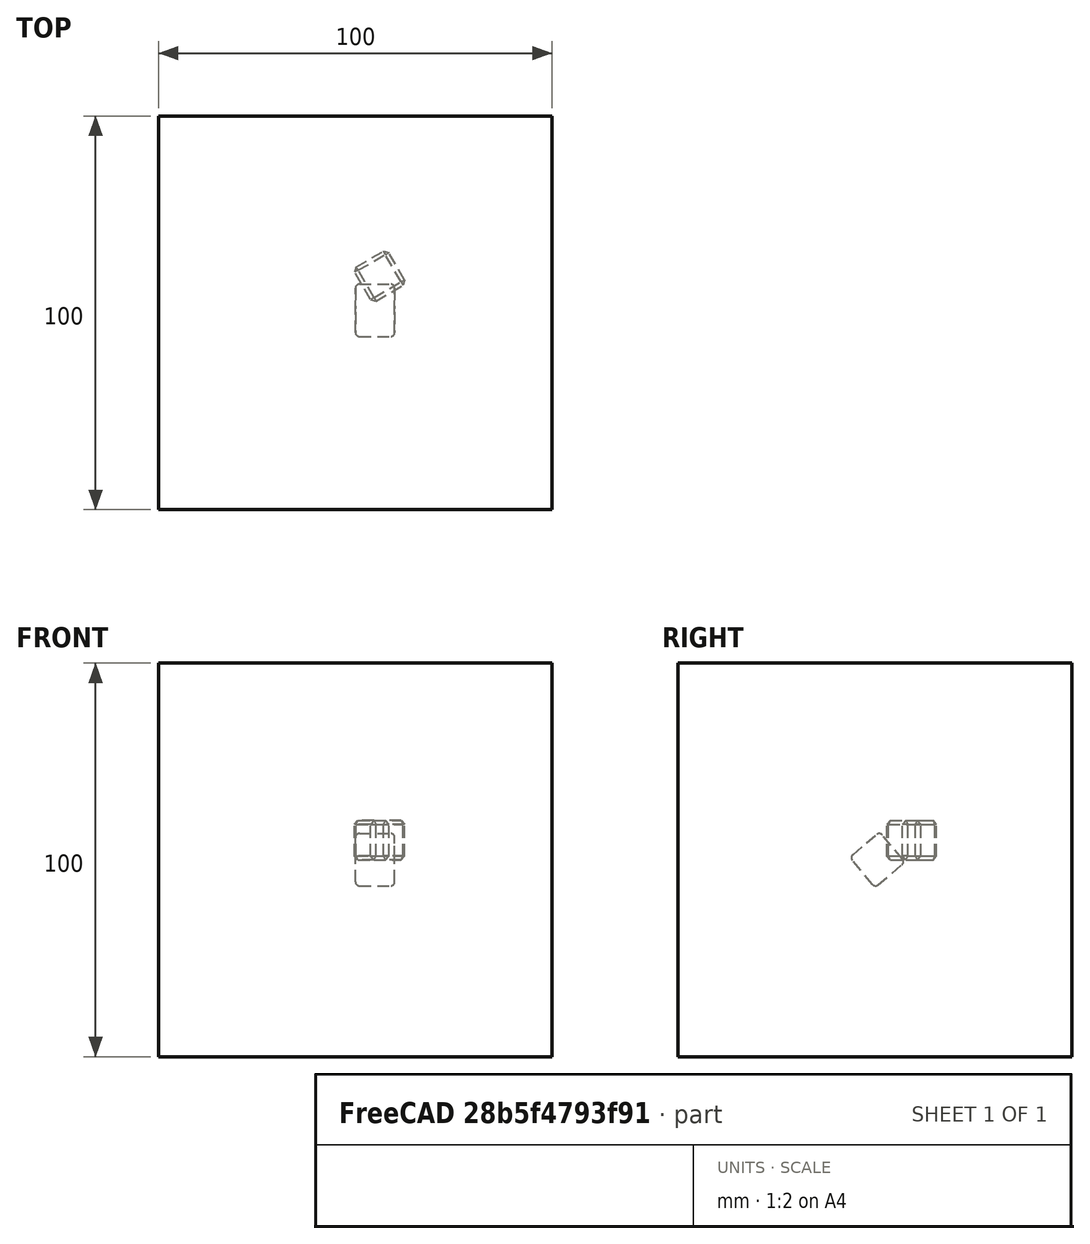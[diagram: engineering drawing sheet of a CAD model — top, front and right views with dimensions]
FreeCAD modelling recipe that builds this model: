
FCSTD DOCUMENT  (FreeCAD 1.0R39109 (Git))
Label: Chamfer_and_fillet
License: All rights reserved
objects: App::DocumentObjectGroupPython×1251, App::Part×3, Part::Box×2, Part::FeaturePython×1, Part::Chamfer×1, Part::Fillet×1
note: 5 computed .brp shape members not serialized (recipe doc carries the construction recipe); baked Part::Feature solids carry a one-line shape summary decoded from their .brp

FEATURE [App::DocumentObjectGroupPython] HALFPI  # scripted group (container) (typed FeaturePython)
  name = HALFPI
  value = pi/2.
FEATURE [App::DocumentObjectGroupPython] PI  # scripted group (container) (typed FeaturePython)
  name = PI
  value = 1.*pi
FEATURE [App::DocumentObjectGroupPython] TWOPI  # scripted group (container) (typed FeaturePython)
  name = TWOPI
  value = 2.*pi
FEATURE [App::DocumentObjectGroupPython] Constants  # scripted group (container) (typed FeaturePython)
  Group = -> [HALFPI,PI,TWOPI]
FEATURE [App::DocumentObjectGroupPython] Variables  # scripted group (container) (typed FeaturePython)
FEATURE [App::DocumentObjectGroupPython] Quantities  # scripted group (container) (typed FeaturePython)
FEATURE [App::DocumentObjectGroupPython] Isotopes  # scripted group (container) (typed FeaturePython)
FEATURE [App::DocumentObjectGroupPython] Elements  # scripted group (container) (typed FeaturePython)
FEATURE [App::DocumentObjectGroupPython] Matrix  # scripted group (container) (typed FeaturePython)
FEATURE [App::DocumentObjectGroupPython] Surfaces  # scripted group (container) (typed FeaturePython)
FEATURE [App::DocumentObjectGroupPython] Opticals  # scripted group (container) (typed FeaturePython)
  Group = -> [Matrix,Surfaces]
FEATURE [App::DocumentObjectGroupPython] G4Isotopes  # scripted group (container) (typed FeaturePython)
FEATURE [App::DocumentObjectGroupPython] H_element  # scripted group (container) (typed FeaturePython)
  Z = 1
  atom_value = 1.008
  formula = H
  name = H_element
FEATURE [App::DocumentObjectGroupPython] He_element  # scripted group (container) (typed FeaturePython)
  Z = 2
  atom_value = 4.0026
  formula = He
  name = He_element
FEATURE [App::DocumentObjectGroupPython] Li_element  # scripted group (container) (typed FeaturePython)
  Z = 3
  atom_value = 6.94
  formula = Li
  name = Li_element
FEATURE [App::DocumentObjectGroupPython] Be_element  # scripted group (container) (typed FeaturePython)
  Z = 4
  atom_value = 9.01218
  formula = Be
  name = Be_element
FEATURE [App::DocumentObjectGroupPython] B_element  # scripted group (container) (typed FeaturePython)
  Z = 5
  atom_value = 10.81
  formula = B
  name = B_element
FEATURE [App::DocumentObjectGroupPython] C_element  # scripted group (container) (typed FeaturePython)
  Z = 6
  atom_value = 12.011
  formula = C
  name = C_element
FEATURE [App::DocumentObjectGroupPython] N_element  # scripted group (container) (typed FeaturePython)
  Z = 7
  atom_value = 14.007
  formula = N
  name = N_element
FEATURE [App::DocumentObjectGroupPython] O_element  # scripted group (container) (typed FeaturePython)
  Z = 8
  atom_value = 15.999
  formula = O
  name = O_element
FEATURE [App::DocumentObjectGroupPython] F_element  # scripted group (container) (typed FeaturePython)
  Z = 9
  atom_value = 18.9984
  formula = F
  name = F_element
FEATURE [App::DocumentObjectGroupPython] Ne_element  # scripted group (container) (typed FeaturePython)
  Z = 10
  atom_value = 20.1797
  formula = Ne
  name = Ne_element
FEATURE [App::DocumentObjectGroupPython] Na_element  # scripted group (container) (typed FeaturePython)
  Z = 11
  atom_value = 22.9898
  formula = Na
  name = Na_element
FEATURE [App::DocumentObjectGroupPython] Mg_element  # scripted group (container) (typed FeaturePython)
  Z = 12
  atom_value = 24.305
  formula = Mg
  name = Mg_element
FEATURE [App::DocumentObjectGroupPython] Al_element  # scripted group (container) (typed FeaturePython)
  Z = 13
  atom_value = 26.9815
  formula = Al
  name = Al_element
FEATURE [App::DocumentObjectGroupPython] Si_element  # scripted group (container) (typed FeaturePython)
  Z = 14
  atom_value = 28.085
  formula = Si
  name = Si_element
FEATURE [App::DocumentObjectGroupPython] P_element  # scripted group (container) (typed FeaturePython)
  Z = 15
  atom_value = 30.9738
  formula = P
  name = P_element
FEATURE [App::DocumentObjectGroupPython] S_element  # scripted group (container) (typed FeaturePython)
  Z = 16
  atom_value = 32.06
  formula = S
  name = S_element
FEATURE [App::DocumentObjectGroupPython] Cl_element  # scripted group (container) (typed FeaturePython)
  Z = 17
  atom_value = 35.45
  formula = Cl
  name = Cl_element
FEATURE [App::DocumentObjectGroupPython] Ar_element  # scripted group (container) (typed FeaturePython)
  Z = 18
  atom_value = 39.95
  formula = Ar
  name = Ar_element
FEATURE [App::DocumentObjectGroupPython] K_element  # scripted group (container) (typed FeaturePython)
  Z = 19
  atom_value = 39.0983
  formula = K
  name = K_element
FEATURE [App::DocumentObjectGroupPython] Ca_element  # scripted group (container) (typed FeaturePython)
  Z = 20
  atom_value = 40.078
  formula = Ca
  name = Ca_element
FEATURE [App::DocumentObjectGroupPython] Sc_element  # scripted group (container) (typed FeaturePython)
  Z = 21
  atom_value = 44.9559
  formula = Sc
  name = Sc_element
FEATURE [App::DocumentObjectGroupPython] Ti_element  # scripted group (container) (typed FeaturePython)
  Z = 22
  atom_value = 47.867
  formula = Ti
  name = Ti_element
FEATURE [App::DocumentObjectGroupPython] V_element  # scripted group (container) (typed FeaturePython)
  Z = 23
  atom_value = 50.9415
  formula = V
  name = V_element
FEATURE [App::DocumentObjectGroupPython] Cr_element  # scripted group (container) (typed FeaturePython)
  Z = 24
  atom_value = 51.9961
  formula = Cr
  name = Cr_element
FEATURE [App::DocumentObjectGroupPython] Mn_element  # scripted group (container) (typed FeaturePython)
  Z = 25
  atom_value = 54.938
  formula = Mn
  name = Mn_element
FEATURE [App::DocumentObjectGroupPython] Fe_element  # scripted group (container) (typed FeaturePython)
  Z = 26
  atom_value = 55.845
  formula = Fe
  name = Fe_element
FEATURE [App::DocumentObjectGroupPython] Co_element  # scripted group (container) (typed FeaturePython)
  Z = 27
  atom_value = 58.9332
  formula = Co
  name = Co_element
FEATURE [App::DocumentObjectGroupPython] Ni_element  # scripted group (container) (typed FeaturePython)
  Z = 28
  atom_value = 58.6934
  formula = Ni
  name = Ni_element
FEATURE [App::DocumentObjectGroupPython] Cu_element  # scripted group (container) (typed FeaturePython)
  Z = 29
  atom_value = 63.546
  formula = Cu
  name = Cu_element
FEATURE [App::DocumentObjectGroupPython] Zn_element  # scripted group (container) (typed FeaturePython)
  Z = 30
  atom_value = 65.38
  formula = Zn
  name = Zn_element
FEATURE [App::DocumentObjectGroupPython] Ga_element  # scripted group (container) (typed FeaturePython)
  Z = 31
  atom_value = 69.723
  formula = Ga
  name = Ga_element
FEATURE [App::DocumentObjectGroupPython] Ge_element  # scripted group (container) (typed FeaturePython)
  Z = 32
  atom_value = 72.63
  formula = Ge
  name = Ge_element
FEATURE [App::DocumentObjectGroupPython] As_element  # scripted group (container) (typed FeaturePython)
  Z = 33
  atom_value = 74.9216
  formula = As
  name = As_element
FEATURE [App::DocumentObjectGroupPython] Se_element  # scripted group (container) (typed FeaturePython)
  Z = 34
  atom_value = 78.971
  formula = Se
  name = Se_element
FEATURE [App::DocumentObjectGroupPython] Br_element  # scripted group (container) (typed FeaturePython)
  Z = 35
  atom_value = 79.904
  formula = Br
  name = Br_element
FEATURE [App::DocumentObjectGroupPython] Kr_element  # scripted group (container) (typed FeaturePython)
  Z = 36
  atom_value = 83.798
  formula = Kr
  name = Kr_element
FEATURE [App::DocumentObjectGroupPython] Rb_element  # scripted group (container) (typed FeaturePython)
  Z = 37
  atom_value = 85.4678
  formula = Rb
  name = Rb_element
FEATURE [App::DocumentObjectGroupPython] Sr_element  # scripted group (container) (typed FeaturePython)
  Z = 38
  atom_value = 87.62
  formula = Sr
  name = Sr_element
FEATURE [App::DocumentObjectGroupPython] Y_element  # scripted group (container) (typed FeaturePython)
  Z = 39
  atom_value = 88.9058
  formula = Y
  name = Y_element
FEATURE [App::DocumentObjectGroupPython] Zr_element  # scripted group (container) (typed FeaturePython)
  Z = 40
  atom_value = 91.224
  formula = Zr
  name = Zr_element
FEATURE [App::DocumentObjectGroupPython] Nb_element  # scripted group (container) (typed FeaturePython)
  Z = 41
  atom_value = 92.9064
  formula = Nb
  name = Nb_element
FEATURE [App::DocumentObjectGroupPython] Mo_element  # scripted group (container) (typed FeaturePython)
  Z = 42
  atom_value = 95.95
  formula = Mo
  name = Mo_element
FEATURE [App::DocumentObjectGroupPython] Tc_element  # scripted group (container) (typed FeaturePython)
  Z = 43
  atom_value = 97
  formula = Tc
  name = Tc_element
FEATURE [App::DocumentObjectGroupPython] Ru_element  # scripted group (container) (typed FeaturePython)
  Z = 44
  atom_value = 101.07
  formula = Ru
  name = Ru_element
FEATURE [App::DocumentObjectGroupPython] Rh_element  # scripted group (container) (typed FeaturePython)
  Z = 45
  atom_value = 102.905
  formula = Rh
  name = Rh_element
FEATURE [App::DocumentObjectGroupPython] Pd_element  # scripted group (container) (typed FeaturePython)
  Z = 46
  atom_value = 106.42
  formula = Pd
  name = Pd_element
FEATURE [App::DocumentObjectGroupPython] Ag_element  # scripted group (container) (typed FeaturePython)
  Z = 47
  atom_value = 107.868
  formula = Ag
  name = Ag_element
FEATURE [App::DocumentObjectGroupPython] Cd_element  # scripted group (container) (typed FeaturePython)
  Z = 48
  atom_value = 112.414
  formula = Cd
  name = Cd_element
FEATURE [App::DocumentObjectGroupPython] In_element  # scripted group (container) (typed FeaturePython)
  Z = 49
  atom_value = 114.818
  formula = In
  name = In_element
FEATURE [App::DocumentObjectGroupPython] Sn_element  # scripted group (container) (typed FeaturePython)
  Z = 50
  atom_value = 118.71
  formula = Sn
  name = Sn_element
FEATURE [App::DocumentObjectGroupPython] Sb_element  # scripted group (container) (typed FeaturePython)
  Z = 51
  atom_value = 121.76
  formula = Sb
  name = Sb_element
FEATURE [App::DocumentObjectGroupPython] Te_element  # scripted group (container) (typed FeaturePython)
  Z = 52
  atom_value = 127.6
  formula = Te
  name = Te_element
FEATURE [App::DocumentObjectGroupPython] I_element  # scripted group (container) (typed FeaturePython)
  Z = 53
  atom_value = 126.904
  formula = I
  name = I_element
FEATURE [App::DocumentObjectGroupPython] Xe_element  # scripted group (container) (typed FeaturePython)
  Z = 54
  atom_value = 131.293
  formula = Xe
  name = Xe_element
FEATURE [App::DocumentObjectGroupPython] Cs_element  # scripted group (container) (typed FeaturePython)
  Z = 55
  atom_value = 132.905
  formula = Cs
  name = Cs_element
FEATURE [App::DocumentObjectGroupPython] Ba_element  # scripted group (container) (typed FeaturePython)
  Z = 56
  atom_value = 137.327
  formula = Ba
  name = Ba_element
FEATURE [App::DocumentObjectGroupPython] La_element  # scripted group (container) (typed FeaturePython)
  Z = 57
  atom_value = 138.905
  formula = La
  name = La_element
FEATURE [App::DocumentObjectGroupPython] Ce_element  # scripted group (container) (typed FeaturePython)
  Z = 58
  atom_value = 140.116
  formula = Ce
  name = Ce_element
FEATURE [App::DocumentObjectGroupPython] Pr_element  # scripted group (container) (typed FeaturePython)
  Z = 59
  atom_value = 140.908
  formula = Pr
  name = Pr_element
FEATURE [App::DocumentObjectGroupPython] Nd_element  # scripted group (container) (typed FeaturePython)
  Z = 60
  atom_value = 144.242
  formula = Nd
  name = Nd_element
FEATURE [App::DocumentObjectGroupPython] Pm_element  # scripted group (container) (typed FeaturePython)
  Z = 61
  atom_value = 145
  formula = Pm
  name = Pm_element
FEATURE [App::DocumentObjectGroupPython] Sm_element  # scripted group (container) (typed FeaturePython)
  Z = 62
  atom_value = 150.36
  formula = Sm
  name = Sm_element
FEATURE [App::DocumentObjectGroupPython] Eu_element  # scripted group (container) (typed FeaturePython)
  Z = 63
  atom_value = 151.964
  formula = Eu
  name = Eu_element
FEATURE [App::DocumentObjectGroupPython] Gd_element  # scripted group (container) (typed FeaturePython)
  Z = 64
  atom_value = 157.25
  formula = Gd
  name = Gd_element
FEATURE [App::DocumentObjectGroupPython] Tb_element  # scripted group (container) (typed FeaturePython)
  Z = 65
  atom_value = 158.925
  formula = Tb
  name = Tb_element
FEATURE [App::DocumentObjectGroupPython] Dy_element  # scripted group (container) (typed FeaturePython)
  Z = 66
  atom_value = 162.5
  formula = Dy
  name = Dy_element
FEATURE [App::DocumentObjectGroupPython] Ho_element  # scripted group (container) (typed FeaturePython)
  Z = 67
  atom_value = 164.93
  formula = Ho
  name = Ho_element
FEATURE [App::DocumentObjectGroupPython] Er_element  # scripted group (container) (typed FeaturePython)
  Z = 68
  atom_value = 167.259
  formula = Er
  name = Er_element
FEATURE [App::DocumentObjectGroupPython] Tm_element  # scripted group (container) (typed FeaturePython)
  Z = 69
  atom_value = 168.934
  formula = Tm
  name = Tm_element
FEATURE [App::DocumentObjectGroupPython] Yb_element  # scripted group (container) (typed FeaturePython)
  Z = 70
  atom_value = 173.045
  formula = Yb
  name = Yb_element
FEATURE [App::DocumentObjectGroupPython] Lu_element  # scripted group (container) (typed FeaturePython)
  Z = 71
  atom_value = 174.967
  formula = Lu
  name = Lu_element
FEATURE [App::DocumentObjectGroupPython] Hf_element  # scripted group (container) (typed FeaturePython)
  Z = 72
  atom_value = 178.49
  formula = Hf
  name = Hf_element
FEATURE [App::DocumentObjectGroupPython] Ta_element  # scripted group (container) (typed FeaturePython)
  Z = 73
  atom_value = 180.948
  formula = Ta
  name = Ta_element
FEATURE [App::DocumentObjectGroupPython] W_element  # scripted group (container) (typed FeaturePython)
  Z = 74
  atom_value = 183.84
  formula = W
  name = W_element
FEATURE [App::DocumentObjectGroupPython] Re_element  # scripted group (container) (typed FeaturePython)
  Z = 75
  atom_value = 186.207
  formula = Re
  name = Re_element
FEATURE [App::DocumentObjectGroupPython] Os_element  # scripted group (container) (typed FeaturePython)
  Z = 76
  atom_value = 190.23
  formula = Os
  name = Os_element
FEATURE [App::DocumentObjectGroupPython] Ir_element  # scripted group (container) (typed FeaturePython)
  Z = 77
  atom_value = 192.217
  formula = Ir
  name = Ir_element
FEATURE [App::DocumentObjectGroupPython] Pt_element  # scripted group (container) (typed FeaturePython)
  Z = 78
  atom_value = 195.084
  formula = Pt
  name = Pt_element
FEATURE [App::DocumentObjectGroupPython] Au_element  # scripted group (container) (typed FeaturePython)
  Z = 79
  atom_value = 196.967
  formula = Au
  name = Au_element
FEATURE [App::DocumentObjectGroupPython] Hg_element  # scripted group (container) (typed FeaturePython)
  Z = 80
  atom_value = 200.592
  formula = Hg
  name = Hg_element
FEATURE [App::DocumentObjectGroupPython] Tl_element  # scripted group (container) (typed FeaturePython)
  Z = 81
  atom_value = 204.38
  formula = Tl
  name = Tl_element
FEATURE [App::DocumentObjectGroupPython] Pb_element  # scripted group (container) (typed FeaturePython)
  Z = 82
  atom_value = 207.2
  formula = Pb
  name = Pb_element
FEATURE [App::DocumentObjectGroupPython] Bi_element  # scripted group (container) (typed FeaturePython)
  Z = 83
  atom_value = 208.98
  formula = Bi
  name = Bi_element
FEATURE [App::DocumentObjectGroupPython] Po_element  # scripted group (container) (typed FeaturePython)
  Z = 84
  atom_value = 209
  formula = Po
  name = Po_element
FEATURE [App::DocumentObjectGroupPython] At_element  # scripted group (container) (typed FeaturePython)
  Z = 85
  atom_value = 210
  formula = At
  name = At_element
FEATURE [App::DocumentObjectGroupPython] Rn_element  # scripted group (container) (typed FeaturePython)
  Z = 86
  atom_value = 222
  formula = Rn
  name = Rn_element
FEATURE [App::DocumentObjectGroupPython] Fr_element  # scripted group (container) (typed FeaturePython)
  Z = 87
  atom_value = 223
  formula = Fr
  name = Fr_element
FEATURE [App::DocumentObjectGroupPython] Ra_element  # scripted group (container) (typed FeaturePython)
  Z = 88
  atom_value = 226
  formula = Ra
  name = Ra_element
FEATURE [App::DocumentObjectGroupPython] Ac_element  # scripted group (container) (typed FeaturePython)
  Z = 89
  atom_value = 227
  formula = Ac
  name = Ac_element
FEATURE [App::DocumentObjectGroupPython] Th_element  # scripted group (container) (typed FeaturePython)
  Z = 90
  atom_value = 232.038
  formula = Th
  name = Th_element
FEATURE [App::DocumentObjectGroupPython] Pa_element  # scripted group (container) (typed FeaturePython)
  Z = 91
  atom_value = 231.036
  formula = Pa
  name = Pa_element
FEATURE [App::DocumentObjectGroupPython] U_element  # scripted group (container) (typed FeaturePython)
  Z = 92
  atom_value = 238.029
  formula = U
  name = U_element
FEATURE [App::DocumentObjectGroupPython] Np_element  # scripted group (container) (typed FeaturePython)
  Z = 93
  atom_value = 237
  formula = Np
  name = Np_element
FEATURE [App::DocumentObjectGroupPython] Pu_element  # scripted group (container) (typed FeaturePython)
  Z = 94
  atom_value = 244
  formula = Pu
  name = Pu_element
FEATURE [App::DocumentObjectGroupPython] Am_element  # scripted group (container) (typed FeaturePython)
  Z = 95
  atom_value = 243
  formula = Am
  name = Am_element
FEATURE [App::DocumentObjectGroupPython] Cm_element  # scripted group (container) (typed FeaturePython)
  Z = 96
  atom_value = 247
  formula = Cm
  name = Cm_element
FEATURE [App::DocumentObjectGroupPython] Bk_element  # scripted group (container) (typed FeaturePython)
  Z = 97
  atom_value = 247
  formula = Bk
  name = Bk_element
FEATURE [App::DocumentObjectGroupPython] Cf_element  # scripted group (container) (typed FeaturePython)
  Z = 98
  atom_value = 251
  formula = Cf
  name = Cf_element
FEATURE [App::DocumentObjectGroupPython] G4Elements  # scripted group (container) (typed FeaturePython)
  Group = -> [H_element,He_element,Li_element,Be_element,B_element,C_element,N_element,O_element,F_element,Ne_element,Na_element,Mg_element,Al_element,Si_element,P_element,S_element,Cl_element,Ar_element,K_element,Ca_element,Sc_element,Ti_element,V_element,Cr_element,Mn_element,Fe_element,Co_element,Ni_element,Cu_element,Zn_element,Ga_element,Ge_element,As_element,Se_element,Br_element,Kr_element,Rb_element,+61 more]
FEATURE [App::DocumentObjectGroupPython] H_element001  label="H_element : 0.101"  # scripted group (container) (typed FeaturePython)
  n = 0.101327
FEATURE [App::DocumentObjectGroupPython] C_element001  label="C_element : 0.775"  # scripted group (container) (typed FeaturePython)
  n = 0.7755
FEATURE [App::DocumentObjectGroupPython] N_element001  label="N_element : 0.035"  # scripted group (container) (typed FeaturePython)
  n = 0.035057
FEATURE [App::DocumentObjectGroupPython] O_element001  label="O_element : 0.052"  # scripted group (container) (typed FeaturePython)
  n = 0.0523159
FEATURE [App::DocumentObjectGroupPython] F_element001  label="F_element : 0.017"  # scripted group (container) (typed FeaturePython)
  n = 0.017422
FEATURE [App::DocumentObjectGroupPython] Ca_element001  label="Ca_element : 0.018"  # scripted group (container) (typed FeaturePython)
  n = 0.018378
FEATURE [App::DocumentObjectGroupPython] G4_A_150_TISSUE  label="G4_A-150_TISSUE"  # scripted group (container) (typed FeaturePython)
  Dunit = g/cm3
  Dvalue = 1.127
  Group = -> [H_element001,C_element001,N_element001,O_element001,F_element001,Ca_element001]
  conduct = 2
  density = 1
  expand = 3
  formula = G4_A-150_TISSUE
  name = G4_A-150_TISSUE
  specific = 4
FEATURE [App::DocumentObjectGroupPython] C_element002  label="C_element : 3"  # scripted group (container) (typed FeaturePython)
  n = 3
  ref = C_element
FEATURE [App::DocumentObjectGroupPython] H_element002  label="H_element : 6"  # scripted group (container) (typed FeaturePython)
  n = 6
  ref = H_element
FEATURE [App::DocumentObjectGroupPython] O_element002  label="O_element : 1"  # scripted group (container) (typed FeaturePython)
  n = 1
  ref = O_element
FEATURE [App::DocumentObjectGroupPython] G4_ACETONE  # scripted group (container) (typed FeaturePython)
  Dunit = g/cm3
  Dvalue = 0.7899
  Group = -> [C_element002,H_element002,O_element002]
  conduct = 2
  density = 1
  expand = 3
  formula = G4_ACETONE
  name = G4_ACETONE
  specific = 4
FEATURE [App::DocumentObjectGroupPython] C_element003  label="C_element : 2"  # scripted group (container) (typed FeaturePython)
  n = 2
  ref = C_element
FEATURE [App::DocumentObjectGroupPython] H_element003  label="H_element : 2"  # scripted group (container) (typed FeaturePython)
  n = 2
  ref = H_element
FEATURE [App::DocumentObjectGroupPython] G4_ACETYLENE  # scripted group (container) (typed FeaturePython)
  Dunit = g/cm3
  Dvalue = 0.0010967
  Group = -> [C_element003,H_element003]
  conduct = 2
  density = 1
  expand = 3
  formula = G4_ACETYLENE
  name = G4_ACETYLENE
  specific = 4
FEATURE [App::DocumentObjectGroupPython] C_element004  label="C_element : 5"  # scripted group (container) (typed FeaturePython)
  n = 5
  ref = C_element
FEATURE [App::DocumentObjectGroupPython] H_element004  label="H_element : 5"  # scripted group (container) (typed FeaturePython)
  n = 5
  ref = H_element
FEATURE [App::DocumentObjectGroupPython] N_element002  label="N_element : 5"  # scripted group (container) (typed FeaturePython)
  n = 5
  ref = N_element
FEATURE [App::DocumentObjectGroupPython] G4_ADENINE  # scripted group (container) (typed FeaturePython)
  Dunit = g/cm3
  Dvalue = 1.6
  Group = -> [C_element004,H_element004,N_element002]
  conduct = 2
  density = 1
  expand = 3
  formula = G4_ADENINE
  name = G4_ADENINE
  specific = 4
FEATURE [App::DocumentObjectGroupPython] H_element005  label="H_element : 0.114"  # scripted group (container) (typed FeaturePython)
  n = 0.114
FEATURE [App::DocumentObjectGroupPython] C_element005  label="C_element : 0.598"  # scripted group (container) (typed FeaturePython)
  n = 0.598
FEATURE [App::DocumentObjectGroupPython] N_element003  label="N_element : 0.007"  # scripted group (container) (typed FeaturePython)
  n = 0.007
FEATURE [App::DocumentObjectGroupPython] O_element003  label="O_element : 0.278"  # scripted group (container) (typed FeaturePython)
  n = 0.278
FEATURE [App::DocumentObjectGroupPython] Na_element001  label="Na_element : 0.001"  # scripted group (container) (typed FeaturePython)
  n = 0.001
FEATURE [App::DocumentObjectGroupPython] S_element001  label="S_element : 0.001"  # scripted group (container) (typed FeaturePython)
  n = 0.001
FEATURE [App::DocumentObjectGroupPython] Cl_element001  label="Cl_element : 0.001"  # scripted group (container) (typed FeaturePython)
  n = 0.001
FEATURE [App::DocumentObjectGroupPython] G4_ADIPOSE_TISSUE_ICRP  # scripted group (container) (typed FeaturePython)
  Dunit = g/cm3
  Dvalue = 0.95
  Group = -> [H_element005,C_element005,N_element003,O_element003,Na_element001,S_element001,Cl_element001]
  conduct = 2
  density = 1
  expand = 3
  formula = G4_ADIPOSE_TISSUE_ICRP
  name = G4_ADIPOSE_TISSUE_ICRP
  specific = 4
FEATURE [App::DocumentObjectGroupPython] C_element006  label="C_element : 0.000"  # scripted group (container) (typed FeaturePython)
  n = 0.000124
FEATURE [App::DocumentObjectGroupPython] N_element004  label="N_element : 0.755"  # scripted group (container) (typed FeaturePython)
  n = 0.755268
FEATURE [App::DocumentObjectGroupPython] O_element004  label="O_element : 0.232"  # scripted group (container) (typed FeaturePython)
  n = 0.231781
FEATURE [App::DocumentObjectGroupPython] Ar_element001  label="Ar_element : 0.013"  # scripted group (container) (typed FeaturePython)
  n = 0.012827
FEATURE [App::DocumentObjectGroupPython] G4_AIR  # scripted group (container) (typed FeaturePython)
  Dunit = g/cm3
  Dvalue = 0.00120479
  Group = -> [C_element006,N_element004,O_element004,Ar_element001]
  conduct = 2
  density = 1
  expand = 3
  formula = G4_AIR
  name = G4_AIR
  specific = 4
FEATURE [App::DocumentObjectGroupPython] C_element007  label="C_element : 006"  # scripted group (container) (typed FeaturePython)
  n = 3
  ref = C_element
FEATURE [App::DocumentObjectGroupPython] H_element006  label="H_element : 7"  # scripted group (container) (typed FeaturePython)
  n = 7
  ref = H_element
FEATURE [App::DocumentObjectGroupPython] N_element005  label="N_element : 1"  # scripted group (container) (typed FeaturePython)
  n = 1
  ref = N_element
FEATURE [App::DocumentObjectGroupPython] O_element005  label="O_element : 2"  # scripted group (container) (typed FeaturePython)
  n = 2
  ref = O_element
FEATURE [App::DocumentObjectGroupPython] G4_ALANINE  # scripted group (container) (typed FeaturePython)
  Dunit = g/cm3
  Dvalue = 1.42
  Group = -> [C_element007,H_element006,N_element005,O_element005]
  conduct = 2
  density = 1
  expand = 3
  formula = G4_ALANINE
  name = G4_ALANINE
  specific = 4
FEATURE [App::DocumentObjectGroupPython] Al_element001  label="Al_element : 2"  # scripted group (container) (typed FeaturePython)
  n = 2
  ref = Al_element
FEATURE [App::DocumentObjectGroupPython] O_element006  label="O_element : 3"  # scripted group (container) (typed FeaturePython)
  n = 3
  ref = O_element
FEATURE [App::DocumentObjectGroupPython] G4_ALUMINUM_OXIDE  # scripted group (container) (typed FeaturePython)
  Dunit = g/cm3
  Dvalue = 3.97
  Group = -> [Al_element001,O_element006]
  conduct = 2
  density = 1
  expand = 3
  formula = G4_ALUMINUM_OXIDE
  name = G4_ALUMINUM_OXIDE
  specific = 4
FEATURE [App::DocumentObjectGroupPython] H_element007  label="H_element : 0.106"  # scripted group (container) (typed FeaturePython)
  n = 0.10593
FEATURE [App::DocumentObjectGroupPython] C_element008  label="C_element : 0.789"  # scripted group (container) (typed FeaturePython)
  n = 0.788974
FEATURE [App::DocumentObjectGroupPython] O_element007  label="O_element : 0.105"  # scripted group (container) (typed FeaturePython)
  n = 0.105096
FEATURE [App::DocumentObjectGroupPython] G4_AMBER  # scripted group (container) (typed FeaturePython)
  Dunit = g/cm3
  Dvalue = 1.1
  Group = -> [H_element007,C_element008,O_element007]
  conduct = 2
  density = 1
  expand = 3
  formula = G4_AMBER
  name = G4_AMBER
  specific = 4
FEATURE [App::DocumentObjectGroupPython] N_element006  label="N_element : 006"  # scripted group (container) (typed FeaturePython)
  n = 1
  ref = N_element
FEATURE [App::DocumentObjectGroupPython] H_element008  label="H_element : 3"  # scripted group (container) (typed FeaturePython)
  n = 3
  ref = H_element
FEATURE [App::DocumentObjectGroupPython] G4_AMMONIA  # scripted group (container) (typed FeaturePython)
  Dunit = g/cm3
  Dvalue = 0.000826019
  Group = -> [N_element006,H_element008]
  conduct = 2
  density = 1
  expand = 3
  formula = G4_AMMONIA
  name = G4_AMMONIA
  specific = 4
FEATURE [App::DocumentObjectGroupPython] C_element009  label="C_element : 6"  # scripted group (container) (typed FeaturePython)
  n = 6
  ref = C_element
FEATURE [App::DocumentObjectGroupPython] H_element009  label="H_element : 008"  # scripted group (container) (typed FeaturePython)
  n = 7
  ref = H_element
FEATURE [App::DocumentObjectGroupPython] N_element007  label="N_element : 007"  # scripted group (container) (typed FeaturePython)
  n = 1
  ref = N_element
FEATURE [App::DocumentObjectGroupPython] G4_ANILINE  # scripted group (container) (typed FeaturePython)
  Dunit = g/cm3
  Dvalue = 1.0235
  Group = -> [C_element009,H_element009,N_element007]
  conduct = 2
  density = 1
  expand = 3
  formula = G4_ANILINE
  name = G4_ANILINE
  specific = 4
FEATURE [App::DocumentObjectGroupPython] C_element010  label="C_element : 14"  # scripted group (container) (typed FeaturePython)
  n = 14
  ref = C_element
FEATURE [App::DocumentObjectGroupPython] H_element010  label="H_element : 10"  # scripted group (container) (typed FeaturePython)
  n = 10
  ref = H_element
FEATURE [App::DocumentObjectGroupPython] G4_ANTHRACENE  # scripted group (container) (typed FeaturePython)
  Dunit = g/cm3
  Dvalue = 1.283
  Group = -> [C_element010,H_element010]
  conduct = 2
  density = 1
  expand = 3
  formula = G4_ANTHRACENE
  name = G4_ANTHRACENE
  specific = 4
FEATURE [App::DocumentObjectGroupPython] H_element011  label="H_element : 0.065"  # scripted group (container) (typed FeaturePython)
  n = 0.0654709
FEATURE [App::DocumentObjectGroupPython] C_element011  label="C_element : 0.537"  # scripted group (container) (typed FeaturePython)
  n = 0.536944
FEATURE [App::DocumentObjectGroupPython] N_element008  label="N_element : 0.021"  # scripted group (container) (typed FeaturePython)
  n = 0.0215
FEATURE [App::DocumentObjectGroupPython] O_element008  label="O_element : 0.032"  # scripted group (container) (typed FeaturePython)
  n = 0.032085
FEATURE [App::DocumentObjectGroupPython] F_element002  label="F_element : 0.167"  # scripted group (container) (typed FeaturePython)
  n = 0.167411
FEATURE [App::DocumentObjectGroupPython] Ca_element002  label="Ca_element : 0.177"  # scripted group (container) (typed FeaturePython)
  n = 0.176589
FEATURE [App::DocumentObjectGroupPython] G4_B_100_BONE  label="G4_B-100_BONE"  # scripted group (container) (typed FeaturePython)
  Dunit = g/cm3
  Dvalue = 1.45
  Group = -> [H_element011,C_element011,N_element008,O_element008,F_element002,Ca_element002]
  conduct = 2
  density = 1
  expand = 3
  formula = G4_B-100_BONE
  name = G4_B-100_BONE
  specific = 4
FEATURE [App::DocumentObjectGroupPython] H_element012  label="H_element : 0.057"  # scripted group (container) (typed FeaturePython)
  n = 0.057441
FEATURE [App::DocumentObjectGroupPython] C_element012  label="C_element : 0.790"  # scripted group (container) (typed FeaturePython)
  n = 0.774591
FEATURE [App::DocumentObjectGroupPython] O_element009  label="O_element : 0.168"  # scripted group (container) (typed FeaturePython)
  n = 0.167968
FEATURE [App::DocumentObjectGroupPython] G4_BAKELITE  # scripted group (container) (typed FeaturePython)
  Dunit = g/cm3
  Dvalue = 1.25
  Group = -> [H_element012,C_element012,O_element009]
  conduct = 2
  density = 1
  expand = 3
  formula = G4_BAKELITE
  name = G4_BAKELITE
  specific = 4
FEATURE [App::DocumentObjectGroupPython] Ba_element001  label="Ba_element : 1"  # scripted group (container) (typed FeaturePython)
  n = 1
  ref = Ba_element
FEATURE [App::DocumentObjectGroupPython] F_element003  label="F_element : 2"  # scripted group (container) (typed FeaturePython)
  n = 2
  ref = F_element
FEATURE [App::DocumentObjectGroupPython] G4_BARIUM_FLUORIDE  # scripted group (container) (typed FeaturePython)
  Dunit = g/cm3
  Dvalue = 4.89
  Group = -> [Ba_element001,F_element003]
  conduct = 2
  density = 1
  expand = 3
  formula = G4_BARIUM_FLUORIDE
  name = G4_BARIUM_FLUORIDE
  specific = 4
FEATURE [App::DocumentObjectGroupPython] Ba_element002  label="Ba_element : 002"  # scripted group (container) (typed FeaturePython)
  n = 1
  ref = Ba_element
FEATURE [App::DocumentObjectGroupPython] S_element002  label="S_element : 1"  # scripted group (container) (typed FeaturePython)
  n = 1
  ref = S_element
FEATURE [App::DocumentObjectGroupPython] O_element010  label="O_element : 4"  # scripted group (container) (typed FeaturePython)
  n = 4
  ref = O_element
FEATURE [App::DocumentObjectGroupPython] G4_BARIUM_SULFATE  # scripted group (container) (typed FeaturePython)
  Dunit = g/cm3
  Dvalue = 4.5
  Group = -> [Ba_element002,S_element002,O_element010]
  conduct = 2
  density = 1
  expand = 3
  formula = G4_BARIUM_SULFATE
  name = G4_BARIUM_SULFATE
  specific = 4
FEATURE [App::DocumentObjectGroupPython] C_element013  label="C_element : 007"  # scripted group (container) (typed FeaturePython)
  n = 6
  ref = C_element
FEATURE [App::DocumentObjectGroupPython] H_element013  label="H_element : 009"  # scripted group (container) (typed FeaturePython)
  n = 6
  ref = H_element
FEATURE [App::DocumentObjectGroupPython] G4_BENZENE  # scripted group (container) (typed FeaturePython)
  Dunit = g/cm3
  Dvalue = 0.87865
  Group = -> [C_element013,H_element013]
  conduct = 2
  density = 1
  expand = 3
  formula = G4_BENZENE
  name = G4_BENZENE
  specific = 4
FEATURE [App::DocumentObjectGroupPython] Be_element001  label="Be_element : 1"  # scripted group (container) (typed FeaturePython)
  n = 1
  ref = Be_element
FEATURE [App::DocumentObjectGroupPython] O_element011  label="O_element : 005"  # scripted group (container) (typed FeaturePython)
  n = 1
  ref = O_element
FEATURE [App::DocumentObjectGroupPython] G4_BERYLLIUM_OXIDE  # scripted group (container) (typed FeaturePython)
  Dunit = g/cm3
  Dvalue = 3.01
  Group = -> [Be_element001,O_element011]
  conduct = 2
  density = 1
  expand = 3
  formula = G4_BERYLLIUM_OXIDE
  name = G4_BERYLLIUM_OXIDE
  specific = 4
FEATURE [App::DocumentObjectGroupPython] Bi_element001  label="Bi_element : 4"  # scripted group (container) (typed FeaturePython)
  n = 4
  ref = Bi_element
FEATURE [App::DocumentObjectGroupPython] Ge_element001  label="Ge_element : 3"  # scripted group (container) (typed FeaturePython)
  n = 3
  ref = Ge_element
FEATURE [App::DocumentObjectGroupPython] O_element012  label="O_element : 12"  # scripted group (container) (typed FeaturePython)
  n = 12
  ref = O_element
FEATURE [App::DocumentObjectGroupPython] G4_BGO  # scripted group (container) (typed FeaturePython)
  Dunit = g/cm3
  Dvalue = 7.13
  Group = -> [Bi_element001,Ge_element001,O_element012]
  conduct = 2
  density = 1
  expand = 3
  formula = G4_BGO
  name = G4_BGO
  specific = 4
FEATURE [App::DocumentObjectGroupPython] H_element014  label="H_element : 0.102"  # scripted group (container) (typed FeaturePython)
  n = 0.102
FEATURE [App::DocumentObjectGroupPython] C_element014  label="C_element : 0.110"  # scripted group (container) (typed FeaturePython)
  n = 0.11
FEATURE [App::DocumentObjectGroupPython] N_element009  label="N_element : 0.033"  # scripted group (container) (typed FeaturePython)
  n = 0.033
FEATURE [App::DocumentObjectGroupPython] O_element013  label="O_element : 0.745"  # scripted group (container) (typed FeaturePython)
  n = 0.745
FEATURE [App::DocumentObjectGroupPython] Na_element002  label="Na_element : 0.002"  # scripted group (container) (typed FeaturePython)
  n = 0.001
FEATURE [App::DocumentObjectGroupPython] P_element001  label="P_element : 0.001"  # scripted group (container) (typed FeaturePython)
  n = 0.001
FEATURE [App::DocumentObjectGroupPython] S_element003  label="S_element : 0.002"  # scripted group (container) (typed FeaturePython)
  n = 0.002
FEATURE [App::DocumentObjectGroupPython] Cl_element002  label="Cl_element : 0.003"  # scripted group (container) (typed FeaturePython)
  n = 0.003
FEATURE [App::DocumentObjectGroupPython] K_element001  label="K_element : 0.002"  # scripted group (container) (typed FeaturePython)
  n = 0.002
FEATURE [App::DocumentObjectGroupPython] Fe_element001  label="Fe_element : 0.001"  # scripted group (container) (typed FeaturePython)
  n = 0.001
FEATURE [App::DocumentObjectGroupPython] G4_BLOOD_ICRP  # scripted group (container) (typed FeaturePython)
  Dunit = g/cm3
  Dvalue = 1.06
  Group = -> [H_element014,C_element014,N_element009,O_element013,Na_element002,P_element001,S_element003,Cl_element002,K_element001,Fe_element001]
  conduct = 2
  density = 1
  expand = 3
  formula = G4_BLOOD_ICRP
  name = G4_BLOOD_ICRP
  specific = 4
FEATURE [App::DocumentObjectGroupPython] H_element015  label="H_element : 0.064"  # scripted group (container) (typed FeaturePython)
  n = 0.064
FEATURE [App::DocumentObjectGroupPython] C_element015  label="C_element : 0.278"  # scripted group (container) (typed FeaturePython)
  n = 0.278
FEATURE [App::DocumentObjectGroupPython] N_element010  label="N_element : 0.027"  # scripted group (container) (typed FeaturePython)
  n = 0.027
FEATURE [App::DocumentObjectGroupPython] O_element014  label="O_element : 0.410"  # scripted group (container) (typed FeaturePython)
  n = 0.41
FEATURE [App::DocumentObjectGroupPython] Mg_element001  label="Mg_element : 0.002"  # scripted group (container) (typed FeaturePython)
  n = 0.002
FEATURE [App::DocumentObjectGroupPython] P_element002  label="P_element : 0.070"  # scripted group (container) (typed FeaturePython)
  n = 0.07
FEATURE [App::DocumentObjectGroupPython] S_element004  label="S_element : 0.003"  # scripted group (container) (typed FeaturePython)
  n = 0.002
FEATURE [App::DocumentObjectGroupPython] Ca_element003  label="Ca_element : 0.147"  # scripted group (container) (typed FeaturePython)
  n = 0.147
FEATURE [App::DocumentObjectGroupPython] G4_BONE_COMPACT_ICRU  # scripted group (container) (typed FeaturePython)
  Dunit = g/cm3
  Dvalue = 1.85
  Group = -> [H_element015,C_element015,N_element010,O_element014,Mg_element001,P_element002,S_element004,Ca_element003]
  conduct = 2
  density = 1
  expand = 3
  formula = G4_BONE_COMPACT_ICRU
  name = G4_BONE_COMPACT_ICRU
  specific = 4
FEATURE [App::DocumentObjectGroupPython] H_element016  label="H_element : 0.034"  # scripted group (container) (typed FeaturePython)
  n = 0.034
FEATURE [App::DocumentObjectGroupPython] C_element016  label="C_element : 0.155"  # scripted group (container) (typed FeaturePython)
  n = 0.155
FEATURE [App::DocumentObjectGroupPython] N_element011  label="N_element : 0.042"  # scripted group (container) (typed FeaturePython)
  n = 0.042
FEATURE [App::DocumentObjectGroupPython] O_element015  label="O_element : 0.435"  # scripted group (container) (typed FeaturePython)
  n = 0.435
FEATURE [App::DocumentObjectGroupPython] Na_element003  label="Na_element : 0.003"  # scripted group (container) (typed FeaturePython)
  n = 0.001
FEATURE [App::DocumentObjectGroupPython] Mg_element002  label="Mg_element : 0.003"  # scripted group (container) (typed FeaturePython)
  n = 0.002
FEATURE [App::DocumentObjectGroupPython] P_element003  label="P_element : 0.103"  # scripted group (container) (typed FeaturePython)
  n = 0.103
FEATURE [App::DocumentObjectGroupPython] S_element005  label="S_element : 0.004"  # scripted group (container) (typed FeaturePython)
  n = 0.003
FEATURE [App::DocumentObjectGroupPython] Ca_element004  label="Ca_element : 0.225"  # scripted group (container) (typed FeaturePython)
  n = 0.225
FEATURE [App::DocumentObjectGroupPython] G4_BONE_CORTICAL_ICRP  # scripted group (container) (typed FeaturePython)
  Dunit = g/cm3
  Dvalue = 1.92
  Group = -> [H_element016,C_element016,N_element011,O_element015,Na_element003,Mg_element002,P_element003,S_element005,Ca_element004]
  conduct = 2
  density = 1
  expand = 3
  formula = G4_BONE_CORTICAL_ICRP
  name = G4_BONE_CORTICAL_ICRP
  specific = 4
FEATURE [App::DocumentObjectGroupPython] B_element001  label="B_element : 4"  # scripted group (container) (typed FeaturePython)
  n = 4
  ref = B_element
FEATURE [App::DocumentObjectGroupPython] C_element017  label="C_element : 1"  # scripted group (container) (typed FeaturePython)
  n = 1
  ref = C_element
FEATURE [App::DocumentObjectGroupPython] G4_BORON_CARBIDE  # scripted group (container) (typed FeaturePython)
  Dunit = g/cm3
  Dvalue = 2.52
  Group = -> [B_element001,C_element017]
  conduct = 2
  density = 1
  expand = 3
  formula = G4_BORON_CARBIDE
  name = G4_BORON_CARBIDE
  specific = 4
FEATURE [App::DocumentObjectGroupPython] B_element002  label="B_element : 2"  # scripted group (container) (typed FeaturePython)
  n = 2
  ref = B_element
FEATURE [App::DocumentObjectGroupPython] O_element016  label="O_element : 006"  # scripted group (container) (typed FeaturePython)
  n = 3
  ref = O_element
FEATURE [App::DocumentObjectGroupPython] G4_BORON_OXIDE  # scripted group (container) (typed FeaturePython)
  Dunit = g/cm3
  Dvalue = 1.812
  Group = -> [B_element002,O_element016]
  conduct = 2
  density = 1
  expand = 3
  formula = G4_BORON_OXIDE
  name = G4_BORON_OXIDE
  specific = 4
FEATURE [App::DocumentObjectGroupPython] H_element017  label="H_element : 0.107"  # scripted group (container) (typed FeaturePython)
  n = 0.107
FEATURE [App::DocumentObjectGroupPython] C_element018  label="C_element : 0.145"  # scripted group (container) (typed FeaturePython)
  n = 0.145
FEATURE [App::DocumentObjectGroupPython] N_element012  label="N_element : 0.022"  # scripted group (container) (typed FeaturePython)
  n = 0.022
FEATURE [App::DocumentObjectGroupPython] O_element017  label="O_element : 0.712"  # scripted group (container) (typed FeaturePython)
  n = 0.712
FEATURE [App::DocumentObjectGroupPython] Na_element004  label="Na_element : 0.004"  # scripted group (container) (typed FeaturePython)
  n = 0.002
FEATURE [App::DocumentObjectGroupPython] P_element004  label="P_element : 0.004"  # scripted group (container) (typed FeaturePython)
  n = 0.004
FEATURE [App::DocumentObjectGroupPython] S_element006  label="S_element : 0.005"  # scripted group (container) (typed FeaturePython)
  n = 0.002
FEATURE [App::DocumentObjectGroupPython] Cl_element003  label="Cl_element : 0.004"  # scripted group (container) (typed FeaturePython)
  n = 0.003
FEATURE [App::DocumentObjectGroupPython] K_element002  label="K_element : 0.003"  # scripted group (container) (typed FeaturePython)
  n = 0.003
FEATURE [App::DocumentObjectGroupPython] G4_BRAIN_ICRP  # scripted group (container) (typed FeaturePython)
  Dunit = g/cm3
  Dvalue = 1.04
  Group = -> [H_element017,C_element018,N_element012,O_element017,Na_element004,P_element004,S_element006,Cl_element003,K_element002]
  conduct = 2
  density = 1
  expand = 3
  formula = G4_BRAIN_ICRP
  name = G4_BRAIN_ICRP
  specific = 4
FEATURE [App::DocumentObjectGroupPython] C_element019  label="C_element : 4"  # scripted group (container) (typed FeaturePython)
  n = 4
  ref = C_element
FEATURE [App::DocumentObjectGroupPython] H_element018  label="H_element : 010"  # scripted group (container) (typed FeaturePython)
  n = 10
  ref = H_element
FEATURE [App::DocumentObjectGroupPython] G4_BUTANE  # scripted group (container) (typed FeaturePython)
  Dunit = g/cm3
  Dvalue = 0.00249343
  Group = -> [C_element019,H_element018]
  conduct = 2
  density = 1
  expand = 3
  formula = G4_BUTANE
  name = G4_BUTANE
  specific = 4
FEATURE [App::DocumentObjectGroupPython] C_element020  label="C_element : 008"  # scripted group (container) (typed FeaturePython)
  n = 4
  ref = C_element
FEATURE [App::DocumentObjectGroupPython] H_element019  label="H_element : 011"  # scripted group (container) (typed FeaturePython)
  n = 10
  ref = H_element
FEATURE [App::DocumentObjectGroupPython] O_element018  label="O_element : 007"  # scripted group (container) (typed FeaturePython)
  n = 1
  ref = O_element
FEATURE [App::DocumentObjectGroupPython] G4_N_BUTYL_ALCOHOL  label="G4_N-BUTYL_ALCOHOL"  # scripted group (container) (typed FeaturePython)
  Dunit = g/cm3
  Dvalue = 0.8098
  Group = -> [C_element020,H_element019,O_element018]
  conduct = 2
  density = 1
  expand = 3
  formula = G4_N-BUTYL_ALCOHOL
  name = G4_N-BUTYL_ALCOHOL
  specific = 4
FEATURE [App::DocumentObjectGroupPython] H_element020  label="H_element : 0.025"  # scripted group (container) (typed FeaturePython)
  n = 0.02468
FEATURE [App::DocumentObjectGroupPython] C_element021  label="C_element : 0.502"  # scripted group (container) (typed FeaturePython)
  n = 0.501611
FEATURE [App::DocumentObjectGroupPython] O_element019  label="O_element : 0.005"  # scripted group (container) (typed FeaturePython)
  n = 0.004527
FEATURE [App::DocumentObjectGroupPython] F_element004  label="F_element : 0.465"  # scripted group (container) (typed FeaturePython)
  n = 0.465209
FEATURE [App::DocumentObjectGroupPython] Si_element001  label="Si_element : 0.004"  # scripted group (container) (typed FeaturePython)
  n = 0.003973
FEATURE [App::DocumentObjectGroupPython] G4_C_552  label="G4_C-552"  # scripted group (container) (typed FeaturePython)
  Dunit = g/cm3
  Dvalue = 1.76
  Group = -> [H_element020,C_element021,O_element019,F_element004,Si_element001]
  conduct = 2
  density = 1
  expand = 3
  formula = G4_C-552
  name = G4_C-552
  specific = 4
FEATURE [App::DocumentObjectGroupPython] Cd_element001  label="Cd_element : 1"  # scripted group (container) (typed FeaturePython)
  n = 1
  ref = Cd_element
FEATURE [App::DocumentObjectGroupPython] Te_element001  label="Te_element : 1"  # scripted group (container) (typed FeaturePython)
  n = 1
  ref = Te_element
FEATURE [App::DocumentObjectGroupPython] G4_CADMIUM_TELLURIDE  # scripted group (container) (typed FeaturePython)
  Dunit = g/cm3
  Dvalue = 6.2
  Group = -> [Cd_element001,Te_element001]
  conduct = 2
  density = 1
  expand = 3
  formula = G4_CADMIUM_TELLURIDE
  name = G4_CADMIUM_TELLURIDE
  specific = 4
FEATURE [App::DocumentObjectGroupPython] Cd_element002  label="Cd_element : 002"  # scripted group (container) (typed FeaturePython)
  n = 1
  ref = Cd_element
FEATURE [App::DocumentObjectGroupPython] W_element001  label="W_element : 1"  # scripted group (container) (typed FeaturePython)
  n = 1
  ref = W_element
FEATURE [App::DocumentObjectGroupPython] O_element020  label="O_element : 008"  # scripted group (container) (typed FeaturePython)
  n = 4
  ref = O_element
FEATURE [App::DocumentObjectGroupPython] G4_CADMIUM_TUNGSTATE  # scripted group (container) (typed FeaturePython)
  Dunit = g/cm3
  Dvalue = 7.9
  Group = -> [Cd_element002,W_element001,O_element020]
  conduct = 2
  density = 1
  expand = 3
  formula = G4_CADMIUM_TUNGSTATE
  name = G4_CADMIUM_TUNGSTATE
  specific = 4
FEATURE [App::DocumentObjectGroupPython] Ca_element005  label="Ca_element : 1"  # scripted group (container) (typed FeaturePython)
  n = 1
  ref = Ca_element
FEATURE [App::DocumentObjectGroupPython] C_element022  label="C_element : 009"  # scripted group (container) (typed FeaturePython)
  n = 1
  ref = C_element
FEATURE [App::DocumentObjectGroupPython] O_element021  label="O_element : 009"  # scripted group (container) (typed FeaturePython)
  n = 3
  ref = O_element
FEATURE [App::DocumentObjectGroupPython] G4_CALCIUM_CARBONATE  # scripted group (container) (typed FeaturePython)
  Dunit = g/cm3
  Dvalue = 2.8
  Group = -> [Ca_element005,C_element022,O_element021]
  conduct = 2
  density = 1
  expand = 3
  formula = G4_CALCIUM_CARBONATE
  name = G4_CALCIUM_CARBONATE
  specific = 4
FEATURE [App::DocumentObjectGroupPython] Ca_element006  label="Ca_element : 002"  # scripted group (container) (typed FeaturePython)
  n = 1
  ref = Ca_element
FEATURE [App::DocumentObjectGroupPython] F_element005  label="F_element : 003"  # scripted group (container) (typed FeaturePython)
  n = 2
  ref = F_element
FEATURE [App::DocumentObjectGroupPython] G4_CALCIUM_FLUORIDE  # scripted group (container) (typed FeaturePython)
  Dunit = g/cm3
  Dvalue = 3.18
  Group = -> [Ca_element006,F_element005]
  conduct = 2
  density = 1
  expand = 3
  formula = G4_CALCIUM_FLUORIDE
  name = G4_CALCIUM_FLUORIDE
  specific = 4
FEATURE [App::DocumentObjectGroupPython] Ca_element007  label="Ca_element : 003"  # scripted group (container) (typed FeaturePython)
  n = 1
  ref = Ca_element
FEATURE [App::DocumentObjectGroupPython] O_element022  label="O_element : 010"  # scripted group (container) (typed FeaturePython)
  n = 1
  ref = O_element
FEATURE [App::DocumentObjectGroupPython] G4_CALCIUM_OXIDE  # scripted group (container) (typed FeaturePython)
  Dunit = g/cm3
  Dvalue = 3.3
  Group = -> [Ca_element007,O_element022]
  conduct = 2
  density = 1
  expand = 3
  formula = G4_CALCIUM_OXIDE
  name = G4_CALCIUM_OXIDE
  specific = 4
FEATURE [App::DocumentObjectGroupPython] Ca_element008  label="Ca_element : 004"  # scripted group (container) (typed FeaturePython)
  n = 1
  ref = Ca_element
FEATURE [App::DocumentObjectGroupPython] S_element007  label="S_element : 002"  # scripted group (container) (typed FeaturePython)
  n = 1
  ref = S_element
FEATURE [App::DocumentObjectGroupPython] O_element023  label="O_element : 011"  # scripted group (container) (typed FeaturePython)
  n = 4
  ref = O_element
FEATURE [App::DocumentObjectGroupPython] G4_CALCIUM_SULFATE  # scripted group (container) (typed FeaturePython)
  Dunit = g/cm3
  Dvalue = 2.96
  Group = -> [Ca_element008,S_element007,O_element023]
  conduct = 2
  density = 1
  expand = 3
  formula = G4_CALCIUM_SULFATE
  name = G4_CALCIUM_SULFATE
  specific = 4
FEATURE [App::DocumentObjectGroupPython] Ca_element009  label="Ca_element : 005"  # scripted group (container) (typed FeaturePython)
  n = 1
  ref = Ca_element
FEATURE [App::DocumentObjectGroupPython] W_element002  label="W_element : 002"  # scripted group (container) (typed FeaturePython)
  n = 1
  ref = W_element
FEATURE [App::DocumentObjectGroupPython] O_element024  label="O_element : 012"  # scripted group (container) (typed FeaturePython)
  n = 4
  ref = O_element
FEATURE [App::DocumentObjectGroupPython] G4_CALCIUM_TUNGSTATE  # scripted group (container) (typed FeaturePython)
  Dunit = g/cm3
  Dvalue = 6.062
  Group = -> [Ca_element009,W_element002,O_element024]
  conduct = 2
  density = 1
  expand = 3
  formula = G4_CALCIUM_TUNGSTATE
  name = G4_CALCIUM_TUNGSTATE
  specific = 4
FEATURE [App::DocumentObjectGroupPython] C_element023  label="C_element : 010"  # scripted group (container) (typed FeaturePython)
  n = 1
  ref = C_element
FEATURE [App::DocumentObjectGroupPython] O_element025  label="O_element : 013"  # scripted group (container) (typed FeaturePython)
  n = 2
  ref = O_element
FEATURE [App::DocumentObjectGroupPython] G4_CARBON_DIOXIDE  # scripted group (container) (typed FeaturePython)
  Dunit = g/cm3
  Dvalue = 0.00184212
  Group = -> [C_element023,O_element025]
  conduct = 2
  density = 1
  expand = 3
  formula = G4_CARBON_DIOXIDE
  name = G4_CARBON_DIOXIDE
  specific = 4
FEATURE [App::DocumentObjectGroupPython] C_element024  label="C_element : 011"  # scripted group (container) (typed FeaturePython)
  n = 1
  ref = C_element
FEATURE [App::DocumentObjectGroupPython] Cl_element004  label="Cl_element : 4"  # scripted group (container) (typed FeaturePython)
  n = 4
  ref = Cl_element
FEATURE [App::DocumentObjectGroupPython] G4_CARBON_TETRACHLORIDE  # scripted group (container) (typed FeaturePython)
  Dunit = g/cm3
  Dvalue = 1.594
  Group = -> [C_element024,Cl_element004]
  conduct = 2
  density = 1
  expand = 3
  formula = G4_CARBON_TETRACHLORIDE
  name = G4_CARBON_TETRACHLORIDE
  specific = 4
FEATURE [App::DocumentObjectGroupPython] C_element025  label="C_element : 012"  # scripted group (container) (typed FeaturePython)
  n = 6
  ref = C_element
FEATURE [App::DocumentObjectGroupPython] H_element021  label="H_element : 012"  # scripted group (container) (typed FeaturePython)
  n = 10
  ref = H_element
FEATURE [App::DocumentObjectGroupPython] O_element026  label="O_element : 5"  # scripted group (container) (typed FeaturePython)
  n = 5
  ref = O_element
FEATURE [App::DocumentObjectGroupPython] G4_CELLULOSE_CELLOPHANE  # scripted group (container) (typed FeaturePython)
  Dunit = g/cm3
  Dvalue = 1.42
  Group = -> [C_element025,H_element021,O_element026]
  conduct = 2
  density = 1
  expand = 3
  formula = G4_CELLULOSE_CELLOPHANE
  name = G4_CELLULOSE_CELLOPHANE
  specific = 4
FEATURE [App::DocumentObjectGroupPython] H_element022  label="H_element : 0.067"  # scripted group (container) (typed FeaturePython)
  n = 0.067125
FEATURE [App::DocumentObjectGroupPython] C_element026  label="C_element : 0.545"  # scripted group (container) (typed FeaturePython)
  n = 0.545403
FEATURE [App::DocumentObjectGroupPython] O_element027  label="O_element : 0.387"  # scripted group (container) (typed FeaturePython)
  n = 0.387472
FEATURE [App::DocumentObjectGroupPython] G4_CELLULOSE_BUTYRATE  # scripted group (container) (typed FeaturePython)
  Dunit = g/cm3
  Dvalue = 1.2
  Group = -> [H_element022,C_element026,O_element027]
  conduct = 2
  density = 1
  expand = 3
  formula = G4_CELLULOSE_BUTYRATE
  name = G4_CELLULOSE_BUTYRATE
  specific = 4
FEATURE [App::DocumentObjectGroupPython] H_element023  label="H_element : 0.029"  # scripted group (container) (typed FeaturePython)
  n = 0.029216
FEATURE [App::DocumentObjectGroupPython] C_element027  label="C_element : 0.271"  # scripted group (container) (typed FeaturePython)
  n = 0.271296
FEATURE [App::DocumentObjectGroupPython] N_element013  label="N_element : 0.121"  # scripted group (container) (typed FeaturePython)
  n = 0.121276
FEATURE [App::DocumentObjectGroupPython] O_element028  label="O_element : 0.578"  # scripted group (container) (typed FeaturePython)
  n = 0.578212
FEATURE [App::DocumentObjectGroupPython] G4_CELLULOSE_NITRATE  # scripted group (container) (typed FeaturePython)
  Dunit = g/cm3
  Dvalue = 1.49
  Group = -> [H_element023,C_element027,N_element013,O_element028]
  conduct = 2
  density = 1
  expand = 3
  formula = G4_CELLULOSE_NITRATE
  name = G4_CELLULOSE_NITRATE
  specific = 4
FEATURE [App::DocumentObjectGroupPython] H_element024  label="H_element : 0.108"  # scripted group (container) (typed FeaturePython)
  n = 0.107596
FEATURE [App::DocumentObjectGroupPython] N_element014  label="N_element : 0.001"  # scripted group (container) (typed FeaturePython)
  n = 0.0008
FEATURE [App::DocumentObjectGroupPython] O_element029  label="O_element : 0.875"  # scripted group (container) (typed FeaturePython)
  n = 0.874976
FEATURE [App::DocumentObjectGroupPython] S_element008  label="S_element : 0.015"  # scripted group (container) (typed FeaturePython)
  n = 0.014627
FEATURE [App::DocumentObjectGroupPython] Ce_element001  label="Ce_element : 0.002"  # scripted group (container) (typed FeaturePython)
  n = 0.002001
FEATURE [App::DocumentObjectGroupPython] G4_CERIC_SULFATE  # scripted group (container) (typed FeaturePython)
  Dunit = g/cm3
  Dvalue = 1.03
  Group = -> [H_element024,N_element014,O_element029,S_element008,Ce_element001]
  conduct = 2
  density = 1
  expand = 3
  formula = G4_CERIC_SULFATE
  name = G4_CERIC_SULFATE
  specific = 4
FEATURE [App::DocumentObjectGroupPython] Cs_element001  label="Cs_element : 1"  # scripted group (container) (typed FeaturePython)
  n = 1
  ref = Cs_element
FEATURE [App::DocumentObjectGroupPython] F_element006  label="F_element : 1"  # scripted group (container) (typed FeaturePython)
  n = 1
  ref = F_element
FEATURE [App::DocumentObjectGroupPython] G4_CESIUM_FLUORIDE  # scripted group (container) (typed FeaturePython)
  Dunit = g/cm3
  Dvalue = 4.115
  Group = -> [Cs_element001,F_element006]
  conduct = 2
  density = 1
  expand = 3
  formula = G4_CESIUM_FLUORIDE
  name = G4_CESIUM_FLUORIDE
  specific = 4
FEATURE [App::DocumentObjectGroupPython] Cs_element002  label="Cs_element : 002"  # scripted group (container) (typed FeaturePython)
  n = 1
  ref = Cs_element
FEATURE [App::DocumentObjectGroupPython] I_element001  label="I_element : 1"  # scripted group (container) (typed FeaturePython)
  n = 1
  ref = I_element
FEATURE [App::DocumentObjectGroupPython] G4_CESIUM_IODIDE  # scripted group (container) (typed FeaturePython)
  Dunit = g/cm3
  Dvalue = 4.51
  Group = -> [Cs_element002,I_element001]
  conduct = 2
  density = 1
  expand = 3
  formula = G4_CESIUM_IODIDE
  name = G4_CESIUM_IODIDE
  specific = 4
FEATURE [App::DocumentObjectGroupPython] C_element028  label="C_element : 013"  # scripted group (container) (typed FeaturePython)
  n = 6
  ref = C_element
FEATURE [App::DocumentObjectGroupPython] H_element025  label="H_element : 013"  # scripted group (container) (typed FeaturePython)
  n = 5
  ref = H_element
FEATURE [App::DocumentObjectGroupPython] Cl_element005  label="Cl_element : 1"  # scripted group (container) (typed FeaturePython)
  n = 1
  ref = Cl_element
FEATURE [App::DocumentObjectGroupPython] G4_CHLOROBENZENE  # scripted group (container) (typed FeaturePython)
  Dunit = g/cm3
  Dvalue = 1.1058
  Group = -> [C_element028,H_element025,Cl_element005]
  conduct = 2
  density = 1
  expand = 3
  formula = G4_CHLOROBENZENE
  name = G4_CHLOROBENZENE
  specific = 4
FEATURE [App::DocumentObjectGroupPython] C_element029  label="C_element : 014"  # scripted group (container) (typed FeaturePython)
  n = 1
  ref = C_element
FEATURE [App::DocumentObjectGroupPython] H_element026  label="H_element : 1"  # scripted group (container) (typed FeaturePython)
  n = 1
  ref = H_element
FEATURE [App::DocumentObjectGroupPython] Cl_element006  label="Cl_element : 3"  # scripted group (container) (typed FeaturePython)
  n = 3
  ref = Cl_element
FEATURE [App::DocumentObjectGroupPython] G4_CHLOROFORM  # scripted group (container) (typed FeaturePython)
  Dunit = g/cm3
  Dvalue = 1.4832
  Group = -> [C_element029,H_element026,Cl_element006]
  conduct = 2
  density = 1
  expand = 3
  formula = G4_CHLOROFORM
  name = G4_CHLOROFORM
  specific = 4
FEATURE [App::DocumentObjectGroupPython] H_element027  label="H_element : 0.010"  # scripted group (container) (typed FeaturePython)
  n = 0.01
FEATURE [App::DocumentObjectGroupPython] C_element030  label="C_element : 0.001"  # scripted group (container) (typed FeaturePython)
  n = 0.001
FEATURE [App::DocumentObjectGroupPython] O_element030  label="O_element : 0.529"  # scripted group (container) (typed FeaturePython)
  n = 0.529107
FEATURE [App::DocumentObjectGroupPython] Na_element005  label="Na_element : 0.016"  # scripted group (container) (typed FeaturePython)
  n = 0.016
FEATURE [App::DocumentObjectGroupPython] Mg_element003  label="Mg_element : 0.004"  # scripted group (container) (typed FeaturePython)
  n = 0.002
FEATURE [App::DocumentObjectGroupPython] Al_element002  label="Al_element : 0.034"  # scripted group (container) (typed FeaturePython)
  n = 0.033872
FEATURE [App::DocumentObjectGroupPython] Si_element002  label="Si_element : 0.337"  # scripted group (container) (typed FeaturePython)
  n = 0.337021
FEATURE [App::DocumentObjectGroupPython] K_element003  label="K_element : 0.013"  # scripted group (container) (typed FeaturePython)
  n = 0.013
FEATURE [App::DocumentObjectGroupPython] Ca_element010  label="Ca_element : 0.044"  # scripted group (container) (typed FeaturePython)
  n = 0.044
FEATURE [App::DocumentObjectGroupPython] Fe_element002  label="Fe_element : 0.014"  # scripted group (container) (typed FeaturePython)
  n = 0.014
FEATURE [App::DocumentObjectGroupPython] G4_CONCRETE  # scripted group (container) (typed FeaturePython)
  Dunit = g/cm3
  Dvalue = 2.3
  Group = -> [H_element027,C_element030,O_element030,Na_element005,Mg_element003,Al_element002,Si_element002,K_element003,Ca_element010,Fe_element002]
  conduct = 2
  density = 1
  expand = 3
  formula = G4_CONCRETE
  name = G4_CONCRETE
  specific = 4
FEATURE [App::DocumentObjectGroupPython] C_element031  label="C_element : 015"  # scripted group (container) (typed FeaturePython)
  n = 6
  ref = C_element
FEATURE [App::DocumentObjectGroupPython] H_element028  label="H_element : 12"  # scripted group (container) (typed FeaturePython)
  n = 12
  ref = H_element
FEATURE [App::DocumentObjectGroupPython] G4_CYCLOHEXANE  # scripted group (container) (typed FeaturePython)
  Dunit = g/cm3
  Dvalue = 0.779
  Group = -> [C_element031,H_element028]
  conduct = 2
  density = 1
  expand = 3
  formula = G4_CYCLOHEXANE
  name = G4_CYCLOHEXANE
  specific = 4
FEATURE [App::DocumentObjectGroupPython] C_element032  label="C_element : 016"  # scripted group (container) (typed FeaturePython)
  n = 6
  ref = C_element
FEATURE [App::DocumentObjectGroupPython] H_element029  label="H_element : 4"  # scripted group (container) (typed FeaturePython)
  n = 4
  ref = H_element
FEATURE [App::DocumentObjectGroupPython] Cl_element007  label="Cl_element : 2"  # scripted group (container) (typed FeaturePython)
  n = 2
  ref = Cl_element
FEATURE [App::DocumentObjectGroupPython] G4_1_2_DICHLOROBENZENE  label="G4_1.2-DICHLOROBENZENE"  # scripted group (container) (typed FeaturePython)
  Dunit = g/cm3
  Dvalue = 1.3048
  Group = -> [C_element032,H_element029,Cl_element007]
  conduct = 2
  density = 1
  expand = 3
  formula = G4_1.2-DICHLOROBENZENE
  name = G4_1.2-DICHLOROBENZENE
  specific = 4
FEATURE [App::DocumentObjectGroupPython] C_element033  label="C_element : 017"  # scripted group (container) (typed FeaturePython)
  n = 4
  ref = C_element
FEATURE [App::DocumentObjectGroupPython] H_element030  label="H_element : 8"  # scripted group (container) (typed FeaturePython)
  n = 8
  ref = H_element
FEATURE [App::DocumentObjectGroupPython] O_element031  label="O_element : 014"  # scripted group (container) (typed FeaturePython)
  n = 1
  ref = O_element
FEATURE [App::DocumentObjectGroupPython] Cl_element008  label="Cl_element : 005"  # scripted group (container) (typed FeaturePython)
  n = 2
  ref = Cl_element
FEATURE [App::DocumentObjectGroupPython] G4_DICHLORODIETHYL_ETHER  # scripted group (container) (typed FeaturePython)
  Dunit = g/cm3
  Dvalue = 1.2199
  Group = -> [C_element033,H_element030,O_element031,Cl_element008]
  conduct = 2
  density = 1
  expand = 3
  formula = G4_DICHLORODIETHYL_ETHER
  name = G4_DICHLORODIETHYL_ETHER
  specific = 4
FEATURE [App::DocumentObjectGroupPython] C_element034  label="C_element : 018"  # scripted group (container) (typed FeaturePython)
  n = 2
  ref = C_element
FEATURE [App::DocumentObjectGroupPython] H_element031  label="H_element : 014"  # scripted group (container) (typed FeaturePython)
  n = 4
  ref = H_element
FEATURE [App::DocumentObjectGroupPython] Cl_element009  label="Cl_element : 006"  # scripted group (container) (typed FeaturePython)
  n = 2
  ref = Cl_element
FEATURE [App::DocumentObjectGroupPython] G4_1_2_DICHLOROETHANE  label="G4_1.2-DICHLOROETHANE"  # scripted group (container) (typed FeaturePython)
  Dunit = g/cm3
  Dvalue = 1.2351
  Group = -> [C_element034,H_element031,Cl_element009]
  conduct = 2
  density = 1
  expand = 3
  formula = G4_1.2-DICHLOROETHANE
  name = G4_1.2-DICHLOROETHANE
  specific = 4
FEATURE [App::DocumentObjectGroupPython] C_element035  label="C_element : 019"  # scripted group (container) (typed FeaturePython)
  n = 4
  ref = C_element
FEATURE [App::DocumentObjectGroupPython] H_element032  label="H_element : 015"  # scripted group (container) (typed FeaturePython)
  n = 10
  ref = H_element
FEATURE [App::DocumentObjectGroupPython] O_element032  label="O_element : 015"  # scripted group (container) (typed FeaturePython)
  n = 1
  ref = O_element
FEATURE [App::DocumentObjectGroupPython] G4_DIETHYL_ETHER  # scripted group (container) (typed FeaturePython)
  Dunit = g/cm3
  Dvalue = 0.71378
  Group = -> [C_element035,H_element032,O_element032]
  conduct = 2
  density = 1
  expand = 3
  formula = G4_DIETHYL_ETHER
  name = G4_DIETHYL_ETHER
  specific = 4
FEATURE [App::DocumentObjectGroupPython] C_element036  label="C_element : 020"  # scripted group (container) (typed FeaturePython)
  n = 3
  ref = C_element
FEATURE [App::DocumentObjectGroupPython] H_element033  label="H_element : 016"  # scripted group (container) (typed FeaturePython)
  n = 7
  ref = H_element
FEATURE [App::DocumentObjectGroupPython] N_element015  label="N_element : 008"  # scripted group (container) (typed FeaturePython)
  n = 1
  ref = N_element
FEATURE [App::DocumentObjectGroupPython] O_element033  label="O_element : 016"  # scripted group (container) (typed FeaturePython)
  n = 1
  ref = O_element
FEATURE [App::DocumentObjectGroupPython] G4_N_N_DIMETHYL_FORMAMIDE  label="G4_N.N-DIMETHYL_FORMAMIDE"  # scripted group (container) (typed FeaturePython)
  Dunit = g/cm3
  Dvalue = 0.9487
  Group = -> [C_element036,H_element033,N_element015,O_element033]
  conduct = 2
  density = 1
  expand = 3
  formula = G4_N.N-DIMETHYL_FORMAMIDE
  name = G4_N.N-DIMETHYL_FORMAMIDE
  specific = 4
FEATURE [App::DocumentObjectGroupPython] C_element037  label="C_element : 021"  # scripted group (container) (typed FeaturePython)
  n = 2
  ref = C_element
FEATURE [App::DocumentObjectGroupPython] H_element034  label="H_element : 017"  # scripted group (container) (typed FeaturePython)
  n = 6
  ref = H_element
FEATURE [App::DocumentObjectGroupPython] O_element034  label="O_element : 017"  # scripted group (container) (typed FeaturePython)
  n = 1
  ref = O_element
FEATURE [App::DocumentObjectGroupPython] S_element009  label="S_element : 003"  # scripted group (container) (typed FeaturePython)
  n = 1
  ref = S_element
FEATURE [App::DocumentObjectGroupPython] G4_DIMETHYL_SULFOXIDE  # scripted group (container) (typed FeaturePython)
  Dunit = g/cm3
  Dvalue = 1.1014
  Group = -> [C_element037,H_element034,O_element034,S_element009]
  conduct = 2
  density = 1
  expand = 3
  formula = G4_DIMETHYL_SULFOXIDE
  name = G4_DIMETHYL_SULFOXIDE
  specific = 4
FEATURE [App::DocumentObjectGroupPython] C_element038  label="C_element : 022"  # scripted group (container) (typed FeaturePython)
  n = 2
  ref = C_element
FEATURE [App::DocumentObjectGroupPython] H_element035  label="H_element : 018"  # scripted group (container) (typed FeaturePython)
  n = 6
  ref = H_element
FEATURE [App::DocumentObjectGroupPython] G4_ETHANE  # scripted group (container) (typed FeaturePython)
  Dunit = g/cm3
  Dvalue = 0.00125324
  Group = -> [C_element038,H_element035]
  conduct = 2
  density = 1
  expand = 3
  formula = G4_ETHANE
  name = G4_ETHANE
  specific = 4
FEATURE [App::DocumentObjectGroupPython] C_element039  label="C_element : 023"  # scripted group (container) (typed FeaturePython)
  n = 2
  ref = C_element
FEATURE [App::DocumentObjectGroupPython] H_element036  label="H_element : 019"  # scripted group (container) (typed FeaturePython)
  n = 6
  ref = H_element
FEATURE [App::DocumentObjectGroupPython] O_element035  label="O_element : 018"  # scripted group (container) (typed FeaturePython)
  n = 1
  ref = O_element
FEATURE [App::DocumentObjectGroupPython] G4_ETHYL_ALCOHOL  # scripted group (container) (typed FeaturePython)
  Dunit = g/cm3
  Dvalue = 0.7893
  Group = -> [C_element039,H_element036,O_element035]
  conduct = 2
  density = 1
  expand = 3
  formula = G4_ETHYL_ALCOHOL
  name = G4_ETHYL_ALCOHOL
  specific = 4
FEATURE [App::DocumentObjectGroupPython] H_element037  label="H_element : 0.090"  # scripted group (container) (typed FeaturePython)
  n = 0.090027
FEATURE [App::DocumentObjectGroupPython] C_element040  label="C_element : 0.585"  # scripted group (container) (typed FeaturePython)
  n = 0.585182
FEATURE [App::DocumentObjectGroupPython] O_element036  label="O_element : 0.325"  # scripted group (container) (typed FeaturePython)
  n = 0.324791
FEATURE [App::DocumentObjectGroupPython] G4_ETHYL_CELLULOSE  # scripted group (container) (typed FeaturePython)
  Dunit = g/cm3
  Dvalue = 1.13
  Group = -> [H_element037,C_element040,O_element036]
  conduct = 2
  density = 1
  expand = 3
  formula = G4_ETHYL_CELLULOSE
  name = G4_ETHYL_CELLULOSE
  specific = 4
FEATURE [App::DocumentObjectGroupPython] C_element041  label="C_element : 024"  # scripted group (container) (typed FeaturePython)
  n = 2
  ref = C_element
FEATURE [App::DocumentObjectGroupPython] H_element038  label="H_element : 020"  # scripted group (container) (typed FeaturePython)
  n = 4
  ref = H_element
FEATURE [App::DocumentObjectGroupPython] G4_ETHYLENE  # scripted group (container) (typed FeaturePython)
  Dunit = g/cm3
  Dvalue = 0.00117497
  Group = -> [C_element041,H_element038]
  conduct = 2
  density = 1
  expand = 3
  formula = G4_ETHYLENE
  name = G4_ETHYLENE
  specific = 4
FEATURE [App::DocumentObjectGroupPython] H_element039  label="H_element : 0.096"  # scripted group (container) (typed FeaturePython)
  n = 0.096
FEATURE [App::DocumentObjectGroupPython] C_element042  label="C_element : 0.195"  # scripted group (container) (typed FeaturePython)
  n = 0.195
FEATURE [App::DocumentObjectGroupPython] N_element016  label="N_element : 0.057"  # scripted group (container) (typed FeaturePython)
  n = 0.057
FEATURE [App::DocumentObjectGroupPython] O_element037  label="O_element : 0.646"  # scripted group (container) (typed FeaturePython)
  n = 0.646
FEATURE [App::DocumentObjectGroupPython] Na_element006  label="Na_element : 0.017"  # scripted group (container) (typed FeaturePython)
  n = 0.001
FEATURE [App::DocumentObjectGroupPython] P_element005  label="P_element : 0.104"  # scripted group (container) (typed FeaturePython)
  n = 0.001
FEATURE [App::DocumentObjectGroupPython] S_element010  label="S_element : 0.016"  # scripted group (container) (typed FeaturePython)
  n = 0.003
FEATURE [App::DocumentObjectGroupPython] Cl_element010  label="Cl_element : 0.005"  # scripted group (container) (typed FeaturePython)
  n = 0.001
FEATURE [App::DocumentObjectGroupPython] G4_EYE_LENS_ICRP  # scripted group (container) (typed FeaturePython)
  Dunit = g/cm3
  Dvalue = 1.07
  Group = -> [H_element039,C_element042,N_element016,O_element037,Na_element006,P_element005,S_element010,Cl_element010]
  conduct = 2
  density = 1
  expand = 3
  formula = G4_EYE_LENS_ICRP
  name = G4_EYE_LENS_ICRP
  specific = 4
FEATURE [App::DocumentObjectGroupPython] Fe_element003  label="Fe_element : 2"  # scripted group (container) (typed FeaturePython)
  n = 2
  ref = Fe_element
FEATURE [App::DocumentObjectGroupPython] O_element038  label="O_element : 019"  # scripted group (container) (typed FeaturePython)
  n = 3
  ref = O_element
FEATURE [App::DocumentObjectGroupPython] G4_FERRIC_OXIDE  # scripted group (container) (typed FeaturePython)
  Dunit = g/cm3
  Dvalue = 5.2
  Group = -> [Fe_element003,O_element038]
  conduct = 2
  density = 1
  expand = 3
  formula = G4_FERRIC_OXIDE
  name = G4_FERRIC_OXIDE
  specific = 4
FEATURE [App::DocumentObjectGroupPython] Fe_element004  label="Fe_element : 1"  # scripted group (container) (typed FeaturePython)
  n = 1
  ref = Fe_element
FEATURE [App::DocumentObjectGroupPython] B_element003  label="B_element : 1"  # scripted group (container) (typed FeaturePython)
  n = 1
  ref = B_element
FEATURE [App::DocumentObjectGroupPython] G4_FERROBORIDE  # scripted group (container) (typed FeaturePython)
  Dunit = g/cm3
  Dvalue = 7.15
  Group = -> [Fe_element004,B_element003]
  conduct = 2
  density = 1
  expand = 3
  formula = G4_FERROBORIDE
  name = G4_FERROBORIDE
  specific = 4
FEATURE [App::DocumentObjectGroupPython] Fe_element005  label="Fe_element : 003"  # scripted group (container) (typed FeaturePython)
  n = 1
  ref = Fe_element
FEATURE [App::DocumentObjectGroupPython] O_element039  label="O_element : 020"  # scripted group (container) (typed FeaturePython)
  n = 1
  ref = O_element
FEATURE [App::DocumentObjectGroupPython] G4_FERROUS_OXIDE  # scripted group (container) (typed FeaturePython)
  Dunit = g/cm3
  Dvalue = 5.7
  Group = -> [Fe_element005,O_element039]
  conduct = 2
  density = 1
  expand = 3
  formula = G4_FERROUS_OXIDE
  name = G4_FERROUS_OXIDE
  specific = 4
FEATURE [App::DocumentObjectGroupPython] H_element040  label="H_element : 0.115"  # scripted group (container) (typed FeaturePython)
  n = 0.108259
FEATURE [App::DocumentObjectGroupPython] N_element017  label="N_element : 0.000"  # scripted group (container) (typed FeaturePython)
  n = 2.7e-05
FEATURE [App::DocumentObjectGroupPython] O_element040  label="O_element : 0.879"  # scripted group (container) (typed FeaturePython)
  n = 0.878636
FEATURE [App::DocumentObjectGroupPython] Na_element007  label="Na_element : 0.000"  # scripted group (container) (typed FeaturePython)
  n = 2.2e-05
FEATURE [App::DocumentObjectGroupPython] S_element011  label="S_element : 0.013"  # scripted group (container) (typed FeaturePython)
  n = 0.012968
FEATURE [App::DocumentObjectGroupPython] Cl_element011  label="Cl_element : 0.000"  # scripted group (container) (typed FeaturePython)
  n = 3.4e-05
FEATURE [App::DocumentObjectGroupPython] Fe_element006  label="Fe_element : 0.000"  # scripted group (container) (typed FeaturePython)
  n = 5.4e-05
FEATURE [App::DocumentObjectGroupPython] G4_FERROUS_SULFATE  # scripted group (container) (typed FeaturePython)
  Dunit = g/cm3
  Dvalue = 1.024
  Group = -> [H_element040,N_element017,O_element040,Na_element007,S_element011,Cl_element011,Fe_element006]
  conduct = 2
  density = 1
  expand = 3
  formula = G4_FERROUS_SULFATE
  name = G4_FERROUS_SULFATE
  specific = 4
FEATURE [App::DocumentObjectGroupPython] C_element043  label="C_element : 0.099"  # scripted group (container) (typed FeaturePython)
  n = 0.099335
FEATURE [App::DocumentObjectGroupPython] F_element007  label="F_element : 0.314"  # scripted group (container) (typed FeaturePython)
  n = 0.314247
FEATURE [App::DocumentObjectGroupPython] Cl_element012  label="Cl_element : 0.586"  # scripted group (container) (typed FeaturePython)
  n = 0.586418
FEATURE [App::DocumentObjectGroupPython] G4_FREON_12  label="G4_FREON-12"  # scripted group (container) (typed FeaturePython)
  Dunit = g/cm3
  Dvalue = 1.12
  Group = -> [C_element043,F_element007,Cl_element012]
  conduct = 2
  density = 1
  expand = 3
  formula = G4_FREON-12
  name = G4_FREON-12
  specific = 4
FEATURE [App::DocumentObjectGroupPython] C_element044  label="C_element : 0.057"  # scripted group (container) (typed FeaturePython)
  n = 0.057245
FEATURE [App::DocumentObjectGroupPython] F_element008  label="F_element : 0.181"  # scripted group (container) (typed FeaturePython)
  n = 0.181096
FEATURE [App::DocumentObjectGroupPython] Br_element001  label="Br_element : 0.762"  # scripted group (container) (typed FeaturePython)
  n = 0.761659
FEATURE [App::DocumentObjectGroupPython] G4_FREON_12B2  label="G4_FREON-12B2"  # scripted group (container) (typed FeaturePython)
  Dunit = g/cm3
  Dvalue = 1.8
  Group = -> [C_element044,F_element008,Br_element001]
  conduct = 2
  density = 1
  expand = 3
  formula = G4_FREON-12B2
  name = G4_FREON-12B2
  specific = 4
FEATURE [App::DocumentObjectGroupPython] C_element045  label="C_element : 0.115"  # scripted group (container) (typed FeaturePython)
  n = 0.114983
FEATURE [App::DocumentObjectGroupPython] F_element009  label="F_element : 0.546"  # scripted group (container) (typed FeaturePython)
  n = 0.545621
FEATURE [App::DocumentObjectGroupPython] Cl_element013  label="Cl_element : 0.339"  # scripted group (container) (typed FeaturePython)
  n = 0.339396
FEATURE [App::DocumentObjectGroupPython] G4_FREON_13  label="G4_FREON-13"  # scripted group (container) (typed FeaturePython)
  Dunit = g/cm3
  Dvalue = 0.95
  Group = -> [C_element045,F_element009,Cl_element013]
  conduct = 2
  density = 1
  expand = 3
  formula = G4_FREON-13
  name = G4_FREON-13
  specific = 4
FEATURE [App::DocumentObjectGroupPython] C_element046  label="C_element : 025"  # scripted group (container) (typed FeaturePython)
  n = 1
  ref = C_element
FEATURE [App::DocumentObjectGroupPython] F_element010  label="F_element : 3"  # scripted group (container) (typed FeaturePython)
  n = 3
  ref = F_element
FEATURE [App::DocumentObjectGroupPython] Br_element002  label="Br_element : 1"  # scripted group (container) (typed FeaturePython)
  n = 1
  ref = Br_element
FEATURE [App::DocumentObjectGroupPython] G4_FREON_13B1  label="G4_FREON-13B1"  # scripted group (container) (typed FeaturePython)
  Dunit = g/cm3
  Dvalue = 1.5
  Group = -> [C_element046,F_element010,Br_element002]
  conduct = 2
  density = 1
  expand = 3
  formula = G4_FREON-13B1
  name = G4_FREON-13B1
  specific = 4
FEATURE [App::DocumentObjectGroupPython] C_element047  label="C_element : 0.061"  # scripted group (container) (typed FeaturePython)
  n = 0.061309
FEATURE [App::DocumentObjectGroupPython] F_element011  label="F_element : 0.291"  # scripted group (container) (typed FeaturePython)
  n = 0.290924
FEATURE [App::DocumentObjectGroupPython] I_element002  label="I_element : 0.648"  # scripted group (container) (typed FeaturePython)
  n = 0.647767
FEATURE [App::DocumentObjectGroupPython] G4_FREON_13I1  label="G4_FREON-13I1"  # scripted group (container) (typed FeaturePython)
  Dunit = g/cm3
  Dvalue = 1.8
  Group = -> [C_element047,F_element011,I_element002]
  conduct = 2
  density = 1
  expand = 3
  formula = G4_FREON-13I1
  name = G4_FREON-13I1
  specific = 4
FEATURE [App::DocumentObjectGroupPython] Gd_element001  label="Gd_element : 2"  # scripted group (container) (typed FeaturePython)
  n = 2
  ref = Gd_element
FEATURE [App::DocumentObjectGroupPython] O_element041  label="O_element : 021"  # scripted group (container) (typed FeaturePython)
  n = 2
  ref = O_element
FEATURE [App::DocumentObjectGroupPython] S_element012  label="S_element : 004"  # scripted group (container) (typed FeaturePython)
  n = 1
  ref = S_element
FEATURE [App::DocumentObjectGroupPython] G4_GADOLINIUM_OXYSULFIDE  # scripted group (container) (typed FeaturePython)
  Dunit = g/cm3
  Dvalue = 7.44
  Group = -> [Gd_element001,O_element041,S_element012]
  conduct = 2
  density = 1
  expand = 3
  formula = G4_GADOLINIUM_OXYSULFIDE
  name = G4_GADOLINIUM_OXYSULFIDE
  specific = 4
FEATURE [App::DocumentObjectGroupPython] Ga_element001  label="Ga_element : 1"  # scripted group (container) (typed FeaturePython)
  n = 1
  ref = Ga_element
FEATURE [App::DocumentObjectGroupPython] As_element001  label="As_element : 1"  # scripted group (container) (typed FeaturePython)
  n = 1
  ref = As_element
FEATURE [App::DocumentObjectGroupPython] G4_GALLIUM_ARSENIDE  # scripted group (container) (typed FeaturePython)
  Dunit = g/cm3
  Dvalue = 5.31
  Group = -> [Ga_element001,As_element001]
  conduct = 2
  density = 1
  expand = 3
  formula = G4_GALLIUM_ARSENIDE
  name = G4_GALLIUM_ARSENIDE
  specific = 4
FEATURE [App::DocumentObjectGroupPython] H_element041  label="H_element : 0.081"  # scripted group (container) (typed FeaturePython)
  n = 0.08118
FEATURE [App::DocumentObjectGroupPython] C_element048  label="C_element : 0.416"  # scripted group (container) (typed FeaturePython)
  n = 0.41606
FEATURE [App::DocumentObjectGroupPython] N_element018  label="N_element : 0.111"  # scripted group (container) (typed FeaturePython)
  n = 0.11124
FEATURE [App::DocumentObjectGroupPython] O_element042  label="O_element : 0.381"  # scripted group (container) (typed FeaturePython)
  n = 0.38064
FEATURE [App::DocumentObjectGroupPython] S_element013  label="S_element : 0.011"  # scripted group (container) (typed FeaturePython)
  n = 0.01088
FEATURE [App::DocumentObjectGroupPython] G4_GEL_PHOTO_EMULSION  # scripted group (container) (typed FeaturePython)
  Dunit = g/cm3
  Dvalue = 1.2914
  Group = -> [H_element041,C_element048,N_element018,O_element042,S_element013]
  conduct = 2
  density = 1
  expand = 3
  formula = G4_GEL_PHOTO_EMULSION
  name = G4_GEL_PHOTO_EMULSION
  specific = 4
FEATURE [App::DocumentObjectGroupPython] B_element004  label="B_element : 0.040"  # scripted group (container) (typed FeaturePython)
  n = 0.0400639
FEATURE [App::DocumentObjectGroupPython] O_element043  label="O_element : 0.540"  # scripted group (container) (typed FeaturePython)
  n = 0.539561
FEATURE [App::DocumentObjectGroupPython] Na_element008  label="Na_element : 0.028"  # scripted group (container) (typed FeaturePython)
  n = 0.0281909
FEATURE [App::DocumentObjectGroupPython] Al_element003  label="Al_element : 0.012"  # scripted group (container) (typed FeaturePython)
  n = 0.011644
FEATURE [App::DocumentObjectGroupPython] Si_element003  label="Si_element : 0.377"  # scripted group (container) (typed FeaturePython)
  n = 0.377219
FEATURE [App::DocumentObjectGroupPython] K_element004  label="K_element : 0.014"  # scripted group (container) (typed FeaturePython)
  n = 0.00332099
FEATURE [App::DocumentObjectGroupPython] G4_Pyrex_Glass  # scripted group (container) (typed FeaturePython)
  Dunit = g/cm3
  Dvalue = 2.23
  Group = -> [B_element004,O_element043,Na_element008,Al_element003,Si_element003,K_element004]
  conduct = 2
  density = 1
  expand = 3
  formula = G4_Pyrex_Glass
  name = G4_Pyrex_Glass
  specific = 4
FEATURE [App::DocumentObjectGroupPython] O_element044  label="O_element : 0.156"  # scripted group (container) (typed FeaturePython)
  n = 0.156453
FEATURE [App::DocumentObjectGroupPython] Si_element004  label="Si_element : 0.081"  # scripted group (container) (typed FeaturePython)
  n = 0.080866
FEATURE [App::DocumentObjectGroupPython] Ti_element001  label="Ti_element : 0.008"  # scripted group (container) (typed FeaturePython)
  n = 0.008092
FEATURE [App::DocumentObjectGroupPython] As_element002  label="As_element : 0.003"  # scripted group (container) (typed FeaturePython)
  n = 0.002651
FEATURE [App::DocumentObjectGroupPython] Pb_element001  label="Pb_element : 0.752"  # scripted group (container) (typed FeaturePython)
  n = 0.751938
FEATURE [App::DocumentObjectGroupPython] G4_GLASS_LEAD  # scripted group (container) (typed FeaturePython)
  Dunit = g/cm3
  Dvalue = 6.22
  Group = -> [O_element044,Si_element004,Ti_element001,As_element002,Pb_element001]
  conduct = 2
  density = 1
  expand = 3
  formula = G4_GLASS_LEAD
  name = G4_GLASS_LEAD
  specific = 4
FEATURE [App::DocumentObjectGroupPython] O_element045  label="O_element : 0.460"  # scripted group (container) (typed FeaturePython)
  n = 0.4598
FEATURE [App::DocumentObjectGroupPython] Na_element009  label="Na_element : 0.096"  # scripted group (container) (typed FeaturePython)
  n = 0.0964411
FEATURE [App::DocumentObjectGroupPython] Si_element005  label="Si_element : 0.378"  # scripted group (container) (typed FeaturePython)
  n = 0.336553
FEATURE [App::DocumentObjectGroupPython] Ca_element011  label="Ca_element : 0.107"  # scripted group (container) (typed FeaturePython)
  n = 0.107205
FEATURE [App::DocumentObjectGroupPython] G4_GLASS_PLATE  # scripted group (container) (typed FeaturePython)
  Dunit = g/cm3
  Dvalue = 2.4
  Group = -> [O_element045,Na_element009,Si_element005,Ca_element011]
  conduct = 2
  density = 1
  expand = 3
  formula = G4_GLASS_PLATE
  name = G4_GLASS_PLATE
  specific = 4
FEATURE [App::DocumentObjectGroupPython] C_element049  label="C_element : 026"  # scripted group (container) (typed FeaturePython)
  n = 5
  ref = C_element
FEATURE [App::DocumentObjectGroupPython] H_element042  label="H_element : 021"  # scripted group (container) (typed FeaturePython)
  n = 10
  ref = H_element
FEATURE [App::DocumentObjectGroupPython] N_element019  label="N_element : 2"  # scripted group (container) (typed FeaturePython)
  n = 2
  ref = N_element
FEATURE [App::DocumentObjectGroupPython] O_element046  label="O_element : 022"  # scripted group (container) (typed FeaturePython)
  n = 3
  ref = O_element
FEATURE [App::DocumentObjectGroupPython] G4_GLUTAMINE  # scripted group (container) (typed FeaturePython)
  Dunit = g/cm3
  Dvalue = 1.46
  Group = -> [C_element049,H_element042,N_element019,O_element046]
  conduct = 2
  density = 1
  expand = 3
  formula = G4_GLUTAMINE
  name = G4_GLUTAMINE
  specific = 4
FEATURE [App::DocumentObjectGroupPython] C_element050  label="C_element : 027"  # scripted group (container) (typed FeaturePython)
  n = 3
  ref = C_element
FEATURE [App::DocumentObjectGroupPython] H_element043  label="H_element : 022"  # scripted group (container) (typed FeaturePython)
  n = 8
  ref = H_element
FEATURE [App::DocumentObjectGroupPython] O_element047  label="O_element : 023"  # scripted group (container) (typed FeaturePython)
  n = 3
  ref = O_element
FEATURE [App::DocumentObjectGroupPython] G4_GLYCEROL  # scripted group (container) (typed FeaturePython)
  Dunit = g/cm3
  Dvalue = 1.2613
  Group = -> [C_element050,H_element043,O_element047]
  conduct = 2
  density = 1
  expand = 3
  formula = G4_GLYCEROL
  name = G4_GLYCEROL
  specific = 4
FEATURE [App::DocumentObjectGroupPython] C_element051  label="C_element : 028"  # scripted group (container) (typed FeaturePython)
  n = 5
  ref = C_element
FEATURE [App::DocumentObjectGroupPython] H_element044  label="H_element : 023"  # scripted group (container) (typed FeaturePython)
  n = 5
  ref = H_element
FEATURE [App::DocumentObjectGroupPython] N_element020  label="N_element : 009"  # scripted group (container) (typed FeaturePython)
  n = 5
  ref = N_element
FEATURE [App::DocumentObjectGroupPython] O_element048  label="O_element : 024"  # scripted group (container) (typed FeaturePython)
  n = 1
  ref = O_element
FEATURE [App::DocumentObjectGroupPython] G4_GUANINE  # scripted group (container) (typed FeaturePython)
  Dunit = g/cm3
  Dvalue = 2.2
  Group = -> [C_element051,H_element044,N_element020,O_element048]
  conduct = 2
  density = 1
  expand = 3
  formula = G4_GUANINE
  name = G4_GUANINE
  specific = 4
FEATURE [App::DocumentObjectGroupPython] Ca_element012  label="Ca_element : 006"  # scripted group (container) (typed FeaturePython)
  n = 1
  ref = Ca_element
FEATURE [App::DocumentObjectGroupPython] S_element014  label="S_element : 005"  # scripted group (container) (typed FeaturePython)
  n = 1
  ref = S_element
FEATURE [App::DocumentObjectGroupPython] O_element049  label="O_element : 6"  # scripted group (container) (typed FeaturePython)
  n = 6
  ref = O_element
FEATURE [App::DocumentObjectGroupPython] H_element045  label="H_element : 024"  # scripted group (container) (typed FeaturePython)
  n = 4
  ref = H_element
FEATURE [App::DocumentObjectGroupPython] G4_GYPSUM  # scripted group (container) (typed FeaturePython)
  Dunit = g/cm3
  Dvalue = 2.32
  Group = -> [Ca_element012,S_element014,O_element049,H_element045]
  conduct = 2
  density = 1
  expand = 3
  formula = G4_GYPSUM
  name = G4_GYPSUM
  specific = 4
FEATURE [App::DocumentObjectGroupPython] C_element052  label="C_element : 7"  # scripted group (container) (typed FeaturePython)
  n = 7
  ref = C_element
FEATURE [App::DocumentObjectGroupPython] H_element046  label="H_element : 16"  # scripted group (container) (typed FeaturePython)
  n = 16
  ref = H_element
FEATURE [App::DocumentObjectGroupPython] G4_N_HEPTANE  label="G4_N-HEPTANE"  # scripted group (container) (typed FeaturePython)
  Dunit = g/cm3
  Dvalue = 0.68376
  Group = -> [C_element052,H_element046]
  conduct = 2
  density = 1
  expand = 3
  formula = G4_N-HEPTANE
  name = G4_N-HEPTANE
  specific = 4
FEATURE [App::DocumentObjectGroupPython] C_element053  label="C_element : 029"  # scripted group (container) (typed FeaturePython)
  n = 6
  ref = C_element
FEATURE [App::DocumentObjectGroupPython] H_element047  label="H_element : 14"  # scripted group (container) (typed FeaturePython)
  n = 14
  ref = H_element
FEATURE [App::DocumentObjectGroupPython] G4_N_HEXANE  label="G4_N-HEXANE"  # scripted group (container) (typed FeaturePython)
  Dunit = g/cm3
  Dvalue = 0.6603
  Group = -> [C_element053,H_element047]
  conduct = 2
  density = 1
  expand = 3
  formula = G4_N-HEXANE
  name = G4_N-HEXANE
  specific = 4
FEATURE [App::DocumentObjectGroupPython] C_element054  label="C_element : 22"  # scripted group (container) (typed FeaturePython)
  n = 22
  ref = C_element
FEATURE [App::DocumentObjectGroupPython] H_element048  label="H_element : 025"  # scripted group (container) (typed FeaturePython)
  n = 10
  ref = H_element
FEATURE [App::DocumentObjectGroupPython] N_element021  label="N_element : 010"  # scripted group (container) (typed FeaturePython)
  n = 2
  ref = N_element
FEATURE [App::DocumentObjectGroupPython] O_element050  label="O_element : 025"  # scripted group (container) (typed FeaturePython)
  n = 5
  ref = O_element
FEATURE [App::DocumentObjectGroupPython] G4_KAPTON  # scripted group (container) (typed FeaturePython)
  Dunit = g/cm3
  Dvalue = 1.42
  Group = -> [C_element054,H_element048,N_element021,O_element050]
  conduct = 2
  density = 1
  expand = 3
  formula = G4_KAPTON
  name = G4_KAPTON
  specific = 4
FEATURE [App::DocumentObjectGroupPython] La_element001  label="La_element : 1"  # scripted group (container) (typed FeaturePython)
  n = 1
  ref = La_element
FEATURE [App::DocumentObjectGroupPython] Br_element003  label="Br_element : 002"  # scripted group (container) (typed FeaturePython)
  n = 1
  ref = Br_element
FEATURE [App::DocumentObjectGroupPython] O_element051  label="O_element : 026"  # scripted group (container) (typed FeaturePython)
  n = 1
  ref = O_element
FEATURE [App::DocumentObjectGroupPython] G4_LANTHANUM_OXYBROMIDE  # scripted group (container) (typed FeaturePython)
  Dunit = g/cm3
  Dvalue = 6.28
  Group = -> [La_element001,Br_element003,O_element051]
  conduct = 2
  density = 1
  expand = 3
  formula = G4_LANTHANUM_OXYBROMIDE
  name = G4_LANTHANUM_OXYBROMIDE
  specific = 4
FEATURE [App::DocumentObjectGroupPython] La_element002  label="La_element : 2"  # scripted group (container) (typed FeaturePython)
  n = 2
  ref = La_element
FEATURE [App::DocumentObjectGroupPython] O_element052  label="O_element : 027"  # scripted group (container) (typed FeaturePython)
  n = 2
  ref = O_element
FEATURE [App::DocumentObjectGroupPython] S_element015  label="S_element : 006"  # scripted group (container) (typed FeaturePython)
  n = 1
  ref = S_element
FEATURE [App::DocumentObjectGroupPython] G4_LANTHANUM_OXYSULFIDE  # scripted group (container) (typed FeaturePython)
  Dunit = g/cm3
  Dvalue = 5.86
  Group = -> [La_element002,O_element052,S_element015]
  conduct = 2
  density = 1
  expand = 3
  formula = G4_LANTHANUM_OXYSULFIDE
  name = G4_LANTHANUM_OXYSULFIDE
  specific = 4
FEATURE [App::DocumentObjectGroupPython] O_element053  label="O_element : 0.072"  # scripted group (container) (typed FeaturePython)
  n = 0.071682
FEATURE [App::DocumentObjectGroupPython] Pb_element002  label="Pb_element : 0.928"  # scripted group (container) (typed FeaturePython)
  n = 0.928318
FEATURE [App::DocumentObjectGroupPython] G4_LEAD_OXIDE  # scripted group (container) (typed FeaturePython)
  Dunit = g/cm3
  Dvalue = 9.53
  Group = -> [O_element053,Pb_element002]
  conduct = 2
  density = 1
  expand = 3
  formula = G4_LEAD_OXIDE
  name = G4_LEAD_OXIDE
  specific = 4
FEATURE [App::DocumentObjectGroupPython] Li_element001  label="Li_element : 1"  # scripted group (container) (typed FeaturePython)
  n = 1
  ref = Li_element
FEATURE [App::DocumentObjectGroupPython] N_element022  label="N_element : 011"  # scripted group (container) (typed FeaturePython)
  n = 1
  ref = N_element
FEATURE [App::DocumentObjectGroupPython] H_element049  label="H_element : 026"  # scripted group (container) (typed FeaturePython)
  n = 2
  ref = H_element
FEATURE [App::DocumentObjectGroupPython] G4_LITHIUM_AMIDE  # scripted group (container) (typed FeaturePython)
  Dunit = g/cm3
  Dvalue = 1.178
  Group = -> [Li_element001,N_element022,H_element049]
  conduct = 2
  density = 1
  expand = 3
  formula = G4_LITHIUM_AMIDE
  name = G4_LITHIUM_AMIDE
  specific = 4
FEATURE [App::DocumentObjectGroupPython] Li_element002  label="Li_element : 2"  # scripted group (container) (typed FeaturePython)
  n = 2
  ref = Li_element
FEATURE [App::DocumentObjectGroupPython] C_element055  label="C_element : 030"  # scripted group (container) (typed FeaturePython)
  n = 1
  ref = C_element
FEATURE [App::DocumentObjectGroupPython] O_element054  label="O_element : 028"  # scripted group (container) (typed FeaturePython)
  n = 3
  ref = O_element
FEATURE [App::DocumentObjectGroupPython] G4_LITHIUM_CARBONATE  # scripted group (container) (typed FeaturePython)
  Dunit = g/cm3
  Dvalue = 2.11
  Group = -> [Li_element002,C_element055,O_element054]
  conduct = 2
  density = 1
  expand = 3
  formula = G4_LITHIUM_CARBONATE
  name = G4_LITHIUM_CARBONATE
  specific = 4
FEATURE [App::DocumentObjectGroupPython] Li_element003  label="Li_element : 003"  # scripted group (container) (typed FeaturePython)
  n = 1
  ref = Li_element
FEATURE [App::DocumentObjectGroupPython] F_element012  label="F_element : 004"  # scripted group (container) (typed FeaturePython)
  n = 1
  ref = F_element
FEATURE [App::DocumentObjectGroupPython] G4_LITHIUM_FLUORIDE  # scripted group (container) (typed FeaturePython)
  Dunit = g/cm3
  Dvalue = 2.635
  Group = -> [Li_element003,F_element012]
  conduct = 2
  density = 1
  expand = 3
  formula = G4_LITHIUM_FLUORIDE
  name = G4_LITHIUM_FLUORIDE
  specific = 4
FEATURE [App::DocumentObjectGroupPython] Li_element004  label="Li_element : 004"  # scripted group (container) (typed FeaturePython)
  n = 1
  ref = Li_element
FEATURE [App::DocumentObjectGroupPython] H_element050  label="H_element : 027"  # scripted group (container) (typed FeaturePython)
  n = 1
  ref = H_element
FEATURE [App::DocumentObjectGroupPython] G4_LITHIUM_HYDRIDE  # scripted group (container) (typed FeaturePython)
  Dunit = g/cm3
  Dvalue = 0.82
  Group = -> [Li_element004,H_element050]
  conduct = 2
  density = 1
  expand = 3
  formula = G4_LITHIUM_HYDRIDE
  name = G4_LITHIUM_HYDRIDE
  specific = 4
FEATURE [App::DocumentObjectGroupPython] Li_element005  label="Li_element : 005"  # scripted group (container) (typed FeaturePython)
  n = 1
  ref = Li_element
FEATURE [App::DocumentObjectGroupPython] I_element003  label="I_element : 002"  # scripted group (container) (typed FeaturePython)
  n = 1
  ref = I_element
FEATURE [App::DocumentObjectGroupPython] G4_LITHIUM_IODIDE  # scripted group (container) (typed FeaturePython)
  Dunit = g/cm3
  Dvalue = 3.494
  Group = -> [Li_element005,I_element003]
  conduct = 2
  density = 1
  expand = 3
  formula = G4_LITHIUM_IODIDE
  name = G4_LITHIUM_IODIDE
  specific = 4
FEATURE [App::DocumentObjectGroupPython] Li_element006  label="Li_element : 006"  # scripted group (container) (typed FeaturePython)
  n = 2
  ref = Li_element
FEATURE [App::DocumentObjectGroupPython] O_element055  label="O_element : 029"  # scripted group (container) (typed FeaturePython)
  n = 1
  ref = O_element
FEATURE [App::DocumentObjectGroupPython] G4_LITHIUM_OXIDE  # scripted group (container) (typed FeaturePython)
  Dunit = g/cm3
  Dvalue = 2.013
  Group = -> [Li_element006,O_element055]
  conduct = 2
  density = 1
  expand = 3
  formula = G4_LITHIUM_OXIDE
  name = G4_LITHIUM_OXIDE
  specific = 4
FEATURE [App::DocumentObjectGroupPython] Li_element007  label="Li_element : 007"  # scripted group (container) (typed FeaturePython)
  n = 2
  ref = Li_element
FEATURE [App::DocumentObjectGroupPython] B_element005  label="B_element : 005"  # scripted group (container) (typed FeaturePython)
  n = 4
  ref = B_element
FEATURE [App::DocumentObjectGroupPython] O_element056  label="O_element : 7"  # scripted group (container) (typed FeaturePython)
  n = 7
  ref = O_element
FEATURE [App::DocumentObjectGroupPython] G4_LITHIUM_TETRABORATE  # scripted group (container) (typed FeaturePython)
  Dunit = g/cm3
  Dvalue = 2.44
  Group = -> [Li_element007,B_element005,O_element056]
  conduct = 2
  density = 1
  expand = 3
  formula = G4_LITHIUM_TETRABORATE
  name = G4_LITHIUM_TETRABORATE
  specific = 4
FEATURE [App::DocumentObjectGroupPython] H_element051  label="H_element : 0.105"  # scripted group (container) (typed FeaturePython)
  n = 0.105
FEATURE [App::DocumentObjectGroupPython] C_element056  label="C_element : 0.083"  # scripted group (container) (typed FeaturePython)
  n = 0.083
FEATURE [App::DocumentObjectGroupPython] N_element023  label="N_element : 0.023"  # scripted group (container) (typed FeaturePython)
  n = 0.023
FEATURE [App::DocumentObjectGroupPython] O_element057  label="O_element : 0.779"  # scripted group (container) (typed FeaturePython)
  n = 0.779
FEATURE [App::DocumentObjectGroupPython] Na_element010  label="Na_element : 0.097"  # scripted group (container) (typed FeaturePython)
  n = 0.002
FEATURE [App::DocumentObjectGroupPython] P_element006  label="P_element : 0.105"  # scripted group (container) (typed FeaturePython)
  n = 0.001
FEATURE [App::DocumentObjectGroupPython] S_element016  label="S_element : 0.017"  # scripted group (container) (typed FeaturePython)
  n = 0.002
FEATURE [App::DocumentObjectGroupPython] Cl_element014  label="Cl_element : 0.587"  # scripted group (container) (typed FeaturePython)
  n = 0.003
FEATURE [App::DocumentObjectGroupPython] K_element005  label="K_element : 0.015"  # scripted group (container) (typed FeaturePython)
  n = 0.002
FEATURE [App::DocumentObjectGroupPython] G4_LUNG_ICRP  # scripted group (container) (typed FeaturePython)
  Dunit = g/cm3
  Dvalue = 1.04
  Group = -> [H_element051,C_element056,N_element023,O_element057,Na_element010,P_element006,S_element016,Cl_element014,K_element005]
  conduct = 2
  density = 1
  expand = 3
  formula = G4_LUNG_ICRP
  name = G4_LUNG_ICRP
  specific = 4
FEATURE [App::DocumentObjectGroupPython] H_element052  label="H_element : 0.116"  # scripted group (container) (typed FeaturePython)
  n = 0.114318
FEATURE [App::DocumentObjectGroupPython] C_element057  label="C_element : 0.656"  # scripted group (container) (typed FeaturePython)
  n = 0.655824
FEATURE [App::DocumentObjectGroupPython] O_element058  label="O_element : 0.092"  # scripted group (container) (typed FeaturePython)
  n = 0.0921831
FEATURE [App::DocumentObjectGroupPython] Mg_element004  label="Mg_element : 0.135"  # scripted group (container) (typed FeaturePython)
  n = 0.134792
FEATURE [App::DocumentObjectGroupPython] Ca_element013  label="Ca_element : 0.003"  # scripted group (container) (typed FeaturePython)
  n = 0.002883
FEATURE [App::DocumentObjectGroupPython] G4_M3_WAX  # scripted group (container) (typed FeaturePython)
  Dunit = g/cm3
  Dvalue = 1.05
  Group = -> [H_element052,C_element057,O_element058,Mg_element004,Ca_element013]
  conduct = 2
  density = 1
  expand = 3
  formula = G4_M3_WAX
  name = G4_M3_WAX
  specific = 4
FEATURE [App::DocumentObjectGroupPython] Mg_element005  label="Mg_element : 1"  # scripted group (container) (typed FeaturePython)
  n = 1
  ref = Mg_element
FEATURE [App::DocumentObjectGroupPython] C_element058  label="C_element : 031"  # scripted group (container) (typed FeaturePython)
  n = 1
  ref = C_element
FEATURE [App::DocumentObjectGroupPython] O_element059  label="O_element : 030"  # scripted group (container) (typed FeaturePython)
  n = 3
  ref = O_element
FEATURE [App::DocumentObjectGroupPython] G4_MAGNESIUM_CARBONATE  # scripted group (container) (typed FeaturePython)
  Dunit = g/cm3
  Dvalue = 2.958
  Group = -> [Mg_element005,C_element058,O_element059]
  conduct = 2
  density = 1
  expand = 3
  formula = G4_MAGNESIUM_CARBONATE
  name = G4_MAGNESIUM_CARBONATE
  specific = 4
FEATURE [App::DocumentObjectGroupPython] Mg_element006  label="Mg_element : 002"  # scripted group (container) (typed FeaturePython)
  n = 1
  ref = Mg_element
FEATURE [App::DocumentObjectGroupPython] F_element013  label="F_element : 005"  # scripted group (container) (typed FeaturePython)
  n = 2
  ref = F_element
FEATURE [App::DocumentObjectGroupPython] G4_MAGNESIUM_FLUORIDE  # scripted group (container) (typed FeaturePython)
  Dunit = g/cm3
  Dvalue = 3
  Group = -> [Mg_element006,F_element013]
  conduct = 2
  density = 1
  expand = 3
  formula = G4_MAGNESIUM_FLUORIDE
  name = G4_MAGNESIUM_FLUORIDE
  specific = 4
FEATURE [App::DocumentObjectGroupPython] Mg_element007  label="Mg_element : 003"  # scripted group (container) (typed FeaturePython)
  n = 1
  ref = Mg_element
FEATURE [App::DocumentObjectGroupPython] O_element060  label="O_element : 031"  # scripted group (container) (typed FeaturePython)
  n = 1
  ref = O_element
FEATURE [App::DocumentObjectGroupPython] G4_MAGNESIUM_OXIDE  # scripted group (container) (typed FeaturePython)
  Dunit = g/cm3
  Dvalue = 3.58
  Group = -> [Mg_element007,O_element060]
  conduct = 2
  density = 1
  expand = 3
  formula = G4_MAGNESIUM_OXIDE
  name = G4_MAGNESIUM_OXIDE
  specific = 4
FEATURE [App::DocumentObjectGroupPython] Mg_element008  label="Mg_element : 004"  # scripted group (container) (typed FeaturePython)
  n = 1
  ref = Mg_element
FEATURE [App::DocumentObjectGroupPython] B_element006  label="B_element : 006"  # scripted group (container) (typed FeaturePython)
  n = 4
  ref = B_element
FEATURE [App::DocumentObjectGroupPython] O_element061  label="O_element : 032"  # scripted group (container) (typed FeaturePython)
  n = 7
  ref = O_element
FEATURE [App::DocumentObjectGroupPython] G4_MAGNESIUM_TETRABORATE  # scripted group (container) (typed FeaturePython)
  Dunit = g/cm3
  Dvalue = 2.53
  Group = -> [Mg_element008,B_element006,O_element061]
  conduct = 2
  density = 1
  expand = 3
  formula = G4_MAGNESIUM_TETRABORATE
  name = G4_MAGNESIUM_TETRABORATE
  specific = 4
FEATURE [App::DocumentObjectGroupPython] Hg_element001  label="Hg_element : 1"  # scripted group (container) (typed FeaturePython)
  n = 1
  ref = Hg_element
FEATURE [App::DocumentObjectGroupPython] I_element004  label="I_element : 2"  # scripted group (container) (typed FeaturePython)
  n = 2
  ref = I_element
FEATURE [App::DocumentObjectGroupPython] G4_MERCURIC_IODIDE  # scripted group (container) (typed FeaturePython)
  Dunit = g/cm3
  Dvalue = 6.36
  Group = -> [Hg_element001,I_element004]
  conduct = 2
  density = 1
  expand = 3
  formula = G4_MERCURIC_IODIDE
  name = G4_MERCURIC_IODIDE
  specific = 4
FEATURE [App::DocumentObjectGroupPython] C_element059  label="C_element : 032"  # scripted group (container) (typed FeaturePython)
  n = 1
  ref = C_element
FEATURE [App::DocumentObjectGroupPython] H_element053  label="H_element : 028"  # scripted group (container) (typed FeaturePython)
  n = 4
  ref = H_element
FEATURE [App::DocumentObjectGroupPython] G4_METHANE  # scripted group (container) (typed FeaturePython)
  Dunit = g/cm3
  Dvalue = 0.000667151
  Group = -> [C_element059,H_element053]
  conduct = 2
  density = 1
  expand = 3
  formula = G4_METHANE
  name = G4_METHANE
  specific = 4
FEATURE [App::DocumentObjectGroupPython] C_element060  label="C_element : 033"  # scripted group (container) (typed FeaturePython)
  n = 1
  ref = C_element
FEATURE [App::DocumentObjectGroupPython] H_element054  label="H_element : 029"  # scripted group (container) (typed FeaturePython)
  n = 4
  ref = H_element
FEATURE [App::DocumentObjectGroupPython] O_element062  label="O_element : 033"  # scripted group (container) (typed FeaturePython)
  n = 1
  ref = O_element
FEATURE [App::DocumentObjectGroupPython] G4_METHANOL  # scripted group (container) (typed FeaturePython)
  Dunit = g/cm3
  Dvalue = 0.7914
  Group = -> [C_element060,H_element054,O_element062]
  conduct = 2
  density = 1
  expand = 3
  formula = G4_METHANOL
  name = G4_METHANOL
  specific = 4
FEATURE [App::DocumentObjectGroupPython] H_element055  label="H_element : 0.134"  # scripted group (container) (typed FeaturePython)
  n = 0.13404
FEATURE [App::DocumentObjectGroupPython] C_element061  label="C_element : 0.778"  # scripted group (container) (typed FeaturePython)
  n = 0.77796
FEATURE [App::DocumentObjectGroupPython] O_element063  label="O_element : 0.035"  # scripted group (container) (typed FeaturePython)
  n = 0.03502
FEATURE [App::DocumentObjectGroupPython] Mg_element009  label="Mg_element : 0.039"  # scripted group (container) (typed FeaturePython)
  n = 0.038594
FEATURE [App::DocumentObjectGroupPython] Ti_element002  label="Ti_element : 0.014"  # scripted group (container) (typed FeaturePython)
  n = 0.014386
FEATURE [App::DocumentObjectGroupPython] G4_MIX_D_WAX  # scripted group (container) (typed FeaturePython)
  Dunit = g/cm3
  Dvalue = 0.99
  Group = -> [H_element055,C_element061,O_element063,Mg_element009,Ti_element002]
  conduct = 2
  density = 1
  expand = 3
  formula = G4_MIX_D_WAX
  name = G4_MIX_D_WAX
  specific = 4
FEATURE [App::DocumentObjectGroupPython] H_element056  label="H_element : 0.135"  # scripted group (container) (typed FeaturePython)
  n = 0.081192
FEATURE [App::DocumentObjectGroupPython] C_element062  label="C_element : 0.583"  # scripted group (container) (typed FeaturePython)
  n = 0.583442
FEATURE [App::DocumentObjectGroupPython] N_element024  label="N_element : 0.018"  # scripted group (container) (typed FeaturePython)
  n = 0.017798
FEATURE [App::DocumentObjectGroupPython] O_element064  label="O_element : 0.186"  # scripted group (container) (typed FeaturePython)
  n = 0.186381
FEATURE [App::DocumentObjectGroupPython] Mg_element010  label="Mg_element : 0.130"  # scripted group (container) (typed FeaturePython)
  n = 0.130287
FEATURE [App::DocumentObjectGroupPython] Cl_element015  label="Cl_element : 0.588"  # scripted group (container) (typed FeaturePython)
  n = 0.0009
FEATURE [App::DocumentObjectGroupPython] G4_MS20_TISSUE  # scripted group (container) (typed FeaturePython)
  Dunit = g/cm3
  Dvalue = 1
  Group = -> [H_element056,C_element062,N_element024,O_element064,Mg_element010,Cl_element015]
  conduct = 2
  density = 1
  expand = 3
  formula = G4_MS20_TISSUE
  name = G4_MS20_TISSUE
  specific = 4
FEATURE [App::DocumentObjectGroupPython] H_element057  label="H_element : 0.136"  # scripted group (container) (typed FeaturePython)
  n = 0.102
FEATURE [App::DocumentObjectGroupPython] C_element063  label="C_element : 0.143"  # scripted group (container) (typed FeaturePython)
  n = 0.143
FEATURE [App::DocumentObjectGroupPython] N_element025  label="N_element : 0.034"  # scripted group (container) (typed FeaturePython)
  n = 0.034
FEATURE [App::DocumentObjectGroupPython] O_element065  label="O_element : 0.710"  # scripted group (container) (typed FeaturePython)
  n = 0.71
FEATURE [App::DocumentObjectGroupPython] Na_element011  label="Na_element : 0.098"  # scripted group (container) (typed FeaturePython)
  n = 0.001
FEATURE [App::DocumentObjectGroupPython] P_element007  label="P_element : 0.002"  # scripted group (container) (typed FeaturePython)
  n = 0.002
FEATURE [App::DocumentObjectGroupPython] S_element017  label="S_element : 0.018"  # scripted group (container) (typed FeaturePython)
  n = 0.003
FEATURE [App::DocumentObjectGroupPython] Cl_element016  label="Cl_element : 0.589"  # scripted group (container) (typed FeaturePython)
  n = 0.001
FEATURE [App::DocumentObjectGroupPython] K_element006  label="K_element : 0.004"  # scripted group (container) (typed FeaturePython)
  n = 0.004
FEATURE [App::DocumentObjectGroupPython] G4_MUSCLE_SKELETAL_ICRP  # scripted group (container) (typed FeaturePython)
  Dunit = g/cm3
  Dvalue = 1.05
  Group = -> [H_element057,C_element063,N_element025,O_element065,Na_element011,P_element007,S_element017,Cl_element016,K_element006]
  conduct = 2
  density = 1
  expand = 3
  formula = G4_MUSCLE_SKELETAL_ICRP
  name = G4_MUSCLE_SKELETAL_ICRP
  specific = 4
FEATURE [App::DocumentObjectGroupPython] H_element058  label="H_element : 0.137"  # scripted group (container) (typed FeaturePython)
  n = 0.102102
FEATURE [App::DocumentObjectGroupPython] C_element064  label="C_element : 0.123"  # scripted group (container) (typed FeaturePython)
  n = 0.123123
FEATURE [App::DocumentObjectGroupPython] N_element026  label="N_element : 0.756"  # scripted group (container) (typed FeaturePython)
  n = 0.035035
FEATURE [App::DocumentObjectGroupPython] O_element066  label="O_element : 0.730"  # scripted group (container) (typed FeaturePython)
  n = 0.72973
FEATURE [App::DocumentObjectGroupPython] Na_element012  label="Na_element : 0.099"  # scripted group (container) (typed FeaturePython)
  n = 0.001001
FEATURE [App::DocumentObjectGroupPython] P_element008  label="P_element : 0.106"  # scripted group (container) (typed FeaturePython)
  n = 0.002002
FEATURE [App::DocumentObjectGroupPython] S_element018  label="S_element : 0.019"  # scripted group (container) (typed FeaturePython)
  n = 0.004004
FEATURE [App::DocumentObjectGroupPython] K_element007  label="K_element : 0.016"  # scripted group (container) (typed FeaturePython)
  n = 0.003003
FEATURE [App::DocumentObjectGroupPython] G4_MUSCLE_STRIATED_ICRU  # scripted group (container) (typed FeaturePython)
  Dunit = g/cm3
  Dvalue = 1.04
  Group = -> [H_element058,C_element064,N_element026,O_element066,Na_element012,P_element008,S_element018,K_element007]
  conduct = 2
  density = 1
  expand = 3
  formula = G4_MUSCLE_STRIATED_ICRU
  name = G4_MUSCLE_STRIATED_ICRU
  specific = 4
FEATURE [App::DocumentObjectGroupPython] H_element059  label="H_element : 0.098"  # scripted group (container) (typed FeaturePython)
  n = 0.0982341
FEATURE [App::DocumentObjectGroupPython] C_element065  label="C_element : 0.156"  # scripted group (container) (typed FeaturePython)
  n = 0.156214
FEATURE [App::DocumentObjectGroupPython] N_element027  label="N_element : 0.757"  # scripted group (container) (typed FeaturePython)
  n = 0.035451
FEATURE [App::DocumentObjectGroupPython] O_element067  label="O_element : 0.880"  # scripted group (container) (typed FeaturePython)
  n = 0.710101
FEATURE [App::DocumentObjectGroupPython] G4_MUSCLE_WITH_SUCROSE  # scripted group (container) (typed FeaturePython)
  Dunit = g/cm3
  Dvalue = 1.11
  Group = -> [H_element059,C_element065,N_element027,O_element067]
  conduct = 2
  density = 1
  expand = 3
  formula = G4_MUSCLE_WITH_SUCROSE
  name = G4_MUSCLE_WITH_SUCROSE
  specific = 4
FEATURE [App::DocumentObjectGroupPython] H_element060  label="H_element : 0.138"  # scripted group (container) (typed FeaturePython)
  n = 0.101969
FEATURE [App::DocumentObjectGroupPython] C_element066  label="C_element : 0.120"  # scripted group (container) (typed FeaturePython)
  n = 0.120058
FEATURE [App::DocumentObjectGroupPython] N_element028  label="N_element : 0.758"  # scripted group (container) (typed FeaturePython)
  n = 0.035451
FEATURE [App::DocumentObjectGroupPython] O_element068  label="O_element : 0.743"  # scripted group (container) (typed FeaturePython)
  n = 0.742522
FEATURE [App::DocumentObjectGroupPython] G4_MUSCLE_WITHOUT_SUCROSE  # scripted group (container) (typed FeaturePython)
  Dunit = g/cm3
  Dvalue = 1.07
  Group = -> [H_element060,C_element066,N_element028,O_element068]
  conduct = 2
  density = 1
  expand = 3
  formula = G4_MUSCLE_WITHOUT_SUCROSE
  name = G4_MUSCLE_WITHOUT_SUCROSE
  specific = 4
FEATURE [App::DocumentObjectGroupPython] C_element067  label="C_element : 10"  # scripted group (container) (typed FeaturePython)
  n = 10
  ref = C_element
FEATURE [App::DocumentObjectGroupPython] H_element061  label="H_element : 030"  # scripted group (container) (typed FeaturePython)
  n = 8
  ref = H_element
FEATURE [App::DocumentObjectGroupPython] G4_NAPHTHALENE  # scripted group (container) (typed FeaturePython)
  Dunit = g/cm3
  Dvalue = 1.145
  Group = -> [C_element067,H_element061]
  conduct = 2
  density = 1
  expand = 3
  formula = G4_NAPHTHALENE
  name = G4_NAPHTHALENE
  specific = 4
FEATURE [App::DocumentObjectGroupPython] C_element068  label="C_element : 034"  # scripted group (container) (typed FeaturePython)
  n = 6
  ref = C_element
FEATURE [App::DocumentObjectGroupPython] H_element062  label="H_element : 031"  # scripted group (container) (typed FeaturePython)
  n = 5
  ref = H_element
FEATURE [App::DocumentObjectGroupPython] N_element029  label="N_element : 012"  # scripted group (container) (typed FeaturePython)
  n = 1
  ref = N_element
FEATURE [App::DocumentObjectGroupPython] O_element069  label="O_element : 034"  # scripted group (container) (typed FeaturePython)
  n = 2
  ref = O_element
FEATURE [App::DocumentObjectGroupPython] G4_NITROBENZENE  # scripted group (container) (typed FeaturePython)
  Dunit = g/cm3
  Dvalue = 1.19867
  Group = -> [C_element068,H_element062,N_element029,O_element069]
  conduct = 2
  density = 1
  expand = 3
  formula = G4_NITROBENZENE
  name = G4_NITROBENZENE
  specific = 4
FEATURE [App::DocumentObjectGroupPython] N_element030  label="N_element : 013"  # scripted group (container) (typed FeaturePython)
  n = 2
  ref = N_element
FEATURE [App::DocumentObjectGroupPython] O_element070  label="O_element : 035"  # scripted group (container) (typed FeaturePython)
  n = 1
  ref = O_element
FEATURE [App::DocumentObjectGroupPython] G4_NITROUS_OXIDE  # scripted group (container) (typed FeaturePython)
  Dunit = g/cm3
  Dvalue = 0.00183094
  Group = -> [N_element030,O_element070]
  conduct = 2
  density = 1
  expand = 3
  formula = G4_NITROUS_OXIDE
  name = G4_NITROUS_OXIDE
  specific = 4
FEATURE [App::DocumentObjectGroupPython] H_element063  label="H_element : 0.104"  # scripted group (container) (typed FeaturePython)
  n = 0.103509
FEATURE [App::DocumentObjectGroupPython] C_element069  label="C_element : 0.648"  # scripted group (container) (typed FeaturePython)
  n = 0.648416
FEATURE [App::DocumentObjectGroupPython] N_element031  label="N_element : 0.100"  # scripted group (container) (typed FeaturePython)
  n = 0.0995361
FEATURE [App::DocumentObjectGroupPython] O_element071  label="O_element : 0.149"  # scripted group (container) (typed FeaturePython)
  n = 0.148539
FEATURE [App::DocumentObjectGroupPython] G4_NYLON_8062  label="G4_NYLON-8062"  # scripted group (container) (typed FeaturePython)
  Dunit = g/cm3
  Dvalue = 1.08
  Group = -> [H_element063,C_element069,N_element031,O_element071]
  conduct = 2
  density = 1
  expand = 3
  formula = G4_NYLON-8062
  name = G4_NYLON-8062
  specific = 4
FEATURE [App::DocumentObjectGroupPython] C_element070  label="C_element : 035"  # scripted group (container) (typed FeaturePython)
  n = 6
  ref = C_element
FEATURE [App::DocumentObjectGroupPython] H_element064  label="H_element : 11"  # scripted group (container) (typed FeaturePython)
  n = 11
  ref = H_element
FEATURE [App::DocumentObjectGroupPython] N_element032  label="N_element : 014"  # scripted group (container) (typed FeaturePython)
  n = 1
  ref = N_element
FEATURE [App::DocumentObjectGroupPython] O_element072  label="O_element : 036"  # scripted group (container) (typed FeaturePython)
  n = 1
  ref = O_element
FEATURE [App::DocumentObjectGroupPython] G4_NYLON_6_6  label="G4_NYLON-6-6"  # scripted group (container) (typed FeaturePython)
  Dunit = g/cm3
  Dvalue = 1.14
  Group = -> [C_element070,H_element064,N_element032,O_element072]
  conduct = 2
  density = 1
  expand = 3
  formula = G4_NYLON-6-6
  name = G4_NYLON-6-6
  specific = 4
FEATURE [App::DocumentObjectGroupPython] H_element065  label="H_element : 0.139"  # scripted group (container) (typed FeaturePython)
  n = 0.107062
FEATURE [App::DocumentObjectGroupPython] C_element071  label="C_element : 0.680"  # scripted group (container) (typed FeaturePython)
  n = 0.680449
FEATURE [App::DocumentObjectGroupPython] N_element033  label="N_element : 0.099"  # scripted group (container) (typed FeaturePython)
  n = 0.099189
FEATURE [App::DocumentObjectGroupPython] O_element073  label="O_element : 0.113"  # scripted group (container) (typed FeaturePython)
  n = 0.1133
FEATURE [App::DocumentObjectGroupPython] G4_NYLON_6_10  label="G4_NYLON-6-10"  # scripted group (container) (typed FeaturePython)
  Dunit = g/cm3
  Dvalue = 1.14
  Group = -> [H_element065,C_element071,N_element033,O_element073]
  conduct = 2
  density = 1
  expand = 3
  formula = G4_NYLON-6-10
  name = G4_NYLON-6-10
  specific = 4
FEATURE [App::DocumentObjectGroupPython] H_element066  label="H_element : 0.140"  # scripted group (container) (typed FeaturePython)
  n = 0.115476
FEATURE [App::DocumentObjectGroupPython] C_element072  label="C_element : 0.721"  # scripted group (container) (typed FeaturePython)
  n = 0.720818
FEATURE [App::DocumentObjectGroupPython] N_element034  label="N_element : 0.076"  # scripted group (container) (typed FeaturePython)
  n = 0.0764169
FEATURE [App::DocumentObjectGroupPython] O_element074  label="O_element : 0.087"  # scripted group (container) (typed FeaturePython)
  n = 0.0872889
FEATURE [App::DocumentObjectGroupPython] G4_NYLON_11_RILSAN  label="G4_NYLON-11_RILSAN"  # scripted group (container) (typed FeaturePython)
  Dunit = g/cm3
  Dvalue = 1.425
  Group = -> [H_element066,C_element072,N_element034,O_element074]
  conduct = 2
  density = 1
  expand = 3
  formula = G4_NYLON-11_RILSAN
  name = G4_NYLON-11_RILSAN
  specific = 4
FEATURE [App::DocumentObjectGroupPython] C_element073  label="C_element : 8"  # scripted group (container) (typed FeaturePython)
  n = 8
  ref = C_element
FEATURE [App::DocumentObjectGroupPython] H_element067  label="H_element : 18"  # scripted group (container) (typed FeaturePython)
  n = 18
  ref = H_element
FEATURE [App::DocumentObjectGroupPython] G4_OCTANE  # scripted group (container) (typed FeaturePython)
  Dunit = g/cm3
  Dvalue = 0.7026
  Group = -> [C_element073,H_element067]
  conduct = 2
  density = 1
  expand = 3
  formula = G4_OCTANE
  name = G4_OCTANE
  specific = 4
FEATURE [App::DocumentObjectGroupPython] C_element074  label="C_element : 25"  # scripted group (container) (typed FeaturePython)
  n = 25
  ref = C_element
FEATURE [App::DocumentObjectGroupPython] H_element068  label="H_element : 52"  # scripted group (container) (typed FeaturePython)
  n = 52
  ref = H_element
FEATURE [App::DocumentObjectGroupPython] G4_PARAFFIN  # scripted group (container) (typed FeaturePython)
  Dunit = g/cm3
  Dvalue = 0.93
  Group = -> [C_element074,H_element068]
  conduct = 2
  density = 1
  expand = 3
  formula = G4_PARAFFIN
  name = G4_PARAFFIN
  specific = 4
FEATURE [App::DocumentObjectGroupPython] C_element075  label="C_element : 036"  # scripted group (container) (typed FeaturePython)
  n = 5
  ref = C_element
FEATURE [App::DocumentObjectGroupPython] H_element069  label="H_element : 032"  # scripted group (container) (typed FeaturePython)
  n = 12
  ref = H_element
FEATURE [App::DocumentObjectGroupPython] G4_N_PENTANE  label="G4_N-PENTANE"  # scripted group (container) (typed FeaturePython)
  Dunit = g/cm3
  Dvalue = 0.6262
  Group = -> [C_element075,H_element069]
  conduct = 2
  density = 1
  expand = 3
  formula = G4_N-PENTANE
  name = G4_N-PENTANE
  specific = 4
FEATURE [App::DocumentObjectGroupPython] H_element070  label="H_element : 0.014"  # scripted group (container) (typed FeaturePython)
  n = 0.0141
FEATURE [App::DocumentObjectGroupPython] C_element076  label="C_element : 0.072"  # scripted group (container) (typed FeaturePython)
  n = 0.072261
FEATURE [App::DocumentObjectGroupPython] N_element035  label="N_element : 0.019"  # scripted group (container) (typed FeaturePython)
  n = 0.01932
FEATURE [App::DocumentObjectGroupPython] O_element075  label="O_element : 0.066"  # scripted group (container) (typed FeaturePython)
  n = 0.066101
FEATURE [App::DocumentObjectGroupPython] S_element019  label="S_element : 0.020"  # scripted group (container) (typed FeaturePython)
  n = 0.00189
FEATURE [App::DocumentObjectGroupPython] Br_element004  label="Br_element : 0.349"  # scripted group (container) (typed FeaturePython)
  n = 0.349103
FEATURE [App::DocumentObjectGroupPython] Ag_element001  label="Ag_element : 0.474"  # scripted group (container) (typed FeaturePython)
  n = 0.474105
FEATURE [App::DocumentObjectGroupPython] I_element005  label="I_element : 0.003"  # scripted group (container) (typed FeaturePython)
  n = 0.00312
FEATURE [App::DocumentObjectGroupPython] G4_PHOTO_EMULSION  # scripted group (container) (typed FeaturePython)
  Dunit = g/cm3
  Dvalue = 3.815
  Group = -> [H_element070,C_element076,N_element035,O_element075,S_element019,Br_element004,Ag_element001,I_element005]
  conduct = 2
  density = 1
  expand = 3
  formula = G4_PHOTO_EMULSION
  name = G4_PHOTO_EMULSION
  specific = 4
FEATURE [App::DocumentObjectGroupPython] C_element077  label="C_element : 9"  # scripted group (container) (typed FeaturePython)
  n = 9
  ref = C_element
FEATURE [App::DocumentObjectGroupPython] H_element071  label="H_element : 033"  # scripted group (container) (typed FeaturePython)
  n = 10
  ref = H_element
FEATURE [App::DocumentObjectGroupPython] G4_PLASTIC_SC_VINYLTOLUENE  # scripted group (container) (typed FeaturePython)
  Dunit = g/cm3
  Dvalue = 1.032
  Group = -> [C_element077,H_element071]
  conduct = 2
  density = 1
  expand = 3
  formula = G4_PLASTIC_SC_VINYLTOLUENE
  name = G4_PLASTIC_SC_VINYLTOLUENE
  specific = 4
FEATURE [App::DocumentObjectGroupPython] Pu_element001  label="Pu_element : 1"  # scripted group (container) (typed FeaturePython)
  n = 1
  ref = Pu_element
FEATURE [App::DocumentObjectGroupPython] O_element076  label="O_element : 037"  # scripted group (container) (typed FeaturePython)
  n = 2
  ref = O_element
FEATURE [App::DocumentObjectGroupPython] G4_PLUTONIUM_DIOXIDE  # scripted group (container) (typed FeaturePython)
  Dunit = g/cm3
  Dvalue = 11.46
  Group = -> [Pu_element001,O_element076]
  conduct = 2
  density = 1
  expand = 3
  formula = G4_PLUTONIUM_DIOXIDE
  name = G4_PLUTONIUM_DIOXIDE
  specific = 4
FEATURE [App::DocumentObjectGroupPython] C_element078  label="C_element : 037"  # scripted group (container) (typed FeaturePython)
  n = 3
  ref = C_element
FEATURE [App::DocumentObjectGroupPython] H_element072  label="H_element : 034"  # scripted group (container) (typed FeaturePython)
  n = 3
  ref = H_element
FEATURE [App::DocumentObjectGroupPython] N_element036  label="N_element : 015"  # scripted group (container) (typed FeaturePython)
  n = 1
  ref = N_element
FEATURE [App::DocumentObjectGroupPython] G4_POLYACRYLONITRILE  # scripted group (container) (typed FeaturePython)
  Dunit = g/cm3
  Dvalue = 1.17
  Group = -> [C_element078,H_element072,N_element036]
  conduct = 2
  density = 1
  expand = 3
  formula = G4_POLYACRYLONITRILE
  name = G4_POLYACRYLONITRILE
  specific = 4
FEATURE [App::DocumentObjectGroupPython] C_element079  label="C_element : 16"  # scripted group (container) (typed FeaturePython)
  n = 16
  ref = C_element
FEATURE [App::DocumentObjectGroupPython] H_element073  label="H_element : 035"  # scripted group (container) (typed FeaturePython)
  n = 14
  ref = H_element
FEATURE [App::DocumentObjectGroupPython] O_element077  label="O_element : 038"  # scripted group (container) (typed FeaturePython)
  n = 3
  ref = O_element
FEATURE [App::DocumentObjectGroupPython] G4_POLYCARBONATE  # scripted group (container) (typed FeaturePython)
  Dunit = g/cm3
  Dvalue = 1.2
  Group = -> [C_element079,H_element073,O_element077]
  conduct = 2
  density = 1
  expand = 3
  formula = G4_POLYCARBONATE
  name = G4_POLYCARBONATE
  specific = 4
FEATURE [App::DocumentObjectGroupPython] C_element080  label="C_element : 038"  # scripted group (container) (typed FeaturePython)
  n = 8
  ref = C_element
FEATURE [App::DocumentObjectGroupPython] H_element074  label="H_element : 036"  # scripted group (container) (typed FeaturePython)
  n = 7
  ref = H_element
FEATURE [App::DocumentObjectGroupPython] Cl_element017  label="Cl_element : 007"  # scripted group (container) (typed FeaturePython)
  n = 1
  ref = Cl_element
FEATURE [App::DocumentObjectGroupPython] G4_POLYCHLOROSTYRENE  # scripted group (container) (typed FeaturePython)
  Dunit = g/cm3
  Dvalue = 1.3
  Group = -> [C_element080,H_element074,Cl_element017]
  conduct = 2
  density = 1
  expand = 3
  formula = G4_POLYCHLOROSTYRENE
  name = G4_POLYCHLOROSTYRENE
  specific = 4
FEATURE [App::DocumentObjectGroupPython] C_element081  label="C_element : 039"  # scripted group (container) (typed FeaturePython)
  n = 1
  ref = C_element
FEATURE [App::DocumentObjectGroupPython] H_element075  label="H_element : 037"  # scripted group (container) (typed FeaturePython)
  n = 2
  ref = H_element
FEATURE [App::DocumentObjectGroupPython] G4_POLYETHYLENE  # scripted group (container) (typed FeaturePython)
  Dunit = g/cm3
  Dvalue = 0.94
  Group = -> [C_element081,H_element075]
  conduct = 2
  density = 1
  expand = 3
  formula = G4_POLYETHYLENE
  name = G4_POLYETHYLENE
  specific = 4
FEATURE [App::DocumentObjectGroupPython] C_element082  label="C_element : 040"  # scripted group (container) (typed FeaturePython)
  n = 10
  ref = C_element
FEATURE [App::DocumentObjectGroupPython] H_element076  label="H_element : 038"  # scripted group (container) (typed FeaturePython)
  n = 8
  ref = H_element
FEATURE [App::DocumentObjectGroupPython] O_element078  label="O_element : 039"  # scripted group (container) (typed FeaturePython)
  n = 4
  ref = O_element
FEATURE [App::DocumentObjectGroupPython] G4_MYLAR  # scripted group (container) (typed FeaturePython)
  Dunit = g/cm3
  Dvalue = 1.4
  Group = -> [C_element082,H_element076,O_element078]
  conduct = 2
  density = 1
  expand = 3
  formula = G4_MYLAR
  name = G4_MYLAR
  specific = 4
FEATURE [App::DocumentObjectGroupPython] C_element083  label="C_element : 041"  # scripted group (container) (typed FeaturePython)
  n = 5
  ref = C_element
FEATURE [App::DocumentObjectGroupPython] H_element077  label="H_element : 039"  # scripted group (container) (typed FeaturePython)
  n = 8
  ref = H_element
FEATURE [App::DocumentObjectGroupPython] O_element079  label="O_element : 040"  # scripted group (container) (typed FeaturePython)
  n = 2
  ref = O_element
FEATURE [App::DocumentObjectGroupPython] G4_PLEXIGLASS  # scripted group (container) (typed FeaturePython)
  Dunit = g/cm3
  Dvalue = 1.19
  Group = -> [C_element083,H_element077,O_element079]
  conduct = 2
  density = 1
  expand = 3
  formula = G4_PLEXIGLASS
  name = G4_PLEXIGLASS
  specific = 4
FEATURE [App::DocumentObjectGroupPython] C_element084  label="C_element : 042"  # scripted group (container) (typed FeaturePython)
  n = 1
  ref = C_element
FEATURE [App::DocumentObjectGroupPython] H_element078  label="H_element : 040"  # scripted group (container) (typed FeaturePython)
  n = 2
  ref = H_element
FEATURE [App::DocumentObjectGroupPython] O_element080  label="O_element : 041"  # scripted group (container) (typed FeaturePython)
  n = 1
  ref = O_element
FEATURE [App::DocumentObjectGroupPython] G4_POLYOXYMETHYLENE  # scripted group (container) (typed FeaturePython)
  Dunit = g/cm3
  Dvalue = 1.425
  Group = -> [C_element084,H_element078,O_element080]
  conduct = 2
  density = 1
  expand = 3
  formula = G4_POLYOXYMETHYLENE
  name = G4_POLYOXYMETHYLENE
  specific = 4
FEATURE [App::DocumentObjectGroupPython] C_element085  label="C_element : 043"  # scripted group (container) (typed FeaturePython)
  n = 2
  ref = C_element
FEATURE [App::DocumentObjectGroupPython] H_element079  label="H_element : 041"  # scripted group (container) (typed FeaturePython)
  n = 4
  ref = H_element
FEATURE [App::DocumentObjectGroupPython] G4_POLYPROPYLENE  # scripted group (container) (typed FeaturePython)
  Dunit = g/cm3
  Dvalue = 0.9
  Group = -> [C_element085,H_element079]
  conduct = 2
  density = 1
  expand = 3
  formula = G4_POLYPROPYLENE
  name = G4_POLYPROPYLENE
  specific = 4
FEATURE [App::DocumentObjectGroupPython] C_element086  label="C_element : 044"  # scripted group (container) (typed FeaturePython)
  n = 8
  ref = C_element
FEATURE [App::DocumentObjectGroupPython] H_element080  label="H_element : 042"  # scripted group (container) (typed FeaturePython)
  n = 8
  ref = H_element
FEATURE [App::DocumentObjectGroupPython] G4_POLYSTYRENE  # scripted group (container) (typed FeaturePython)
  Dunit = g/cm3
  Dvalue = 1.06
  Group = -> [C_element086,H_element080]
  conduct = 2
  density = 1
  expand = 3
  formula = G4_POLYSTYRENE
  name = G4_POLYSTYRENE
  specific = 4
FEATURE [App::DocumentObjectGroupPython] C_element087  label="C_element : 045"  # scripted group (container) (typed FeaturePython)
  n = 2
  ref = C_element
FEATURE [App::DocumentObjectGroupPython] F_element014  label="F_element : 4"  # scripted group (container) (typed FeaturePython)
  n = 4
  ref = F_element
FEATURE [App::DocumentObjectGroupPython] G4_TEFLON  # scripted group (container) (typed FeaturePython)
  Dunit = g/cm3
  Dvalue = 2.2
  Group = -> [C_element087,F_element014]
  conduct = 2
  density = 1
  expand = 3
  formula = G4_TEFLON
  name = G4_TEFLON
  specific = 4
FEATURE [App::DocumentObjectGroupPython] C_element088  label="C_element : 046"  # scripted group (container) (typed FeaturePython)
  n = 2
  ref = C_element
FEATURE [App::DocumentObjectGroupPython] F_element015  label="F_element : 006"  # scripted group (container) (typed FeaturePython)
  n = 3
  ref = F_element
FEATURE [App::DocumentObjectGroupPython] Cl_element018  label="Cl_element : 008"  # scripted group (container) (typed FeaturePython)
  n = 1
  ref = Cl_element
FEATURE [App::DocumentObjectGroupPython] G4_POLYTRIFLUOROCHLOROETHYLENE  # scripted group (container) (typed FeaturePython)
  Dunit = g/cm3
  Dvalue = 2.1
  Group = -> [C_element088,F_element015,Cl_element018]
  conduct = 2
  density = 1
  expand = 3
  formula = G4_POLYTRIFLUOROCHLOROETHYLENE
  name = G4_POLYTRIFLUOROCHLOROETHYLENE
  specific = 4
FEATURE [App::DocumentObjectGroupPython] C_element089  label="C_element : 047"  # scripted group (container) (typed FeaturePython)
  n = 4
  ref = C_element
FEATURE [App::DocumentObjectGroupPython] H_element081  label="H_element : 043"  # scripted group (container) (typed FeaturePython)
  n = 6
  ref = H_element
FEATURE [App::DocumentObjectGroupPython] O_element081  label="O_element : 042"  # scripted group (container) (typed FeaturePython)
  n = 2
  ref = O_element
FEATURE [App::DocumentObjectGroupPython] G4_POLYVINYL_ACETATE  # scripted group (container) (typed FeaturePython)
  Dunit = g/cm3
  Dvalue = 1.19
  Group = -> [C_element089,H_element081,O_element081]
  conduct = 2
  density = 1
  expand = 3
  formula = G4_POLYVINYL_ACETATE
  name = G4_POLYVINYL_ACETATE
  specific = 4
FEATURE [App::DocumentObjectGroupPython] C_element090  label="C_element : 048"  # scripted group (container) (typed FeaturePython)
  n = 2
  ref = C_element
FEATURE [App::DocumentObjectGroupPython] H_element082  label="H_element : 044"  # scripted group (container) (typed FeaturePython)
  n = 4
  ref = H_element
FEATURE [App::DocumentObjectGroupPython] O_element082  label="O_element : 043"  # scripted group (container) (typed FeaturePython)
  n = 1
  ref = O_element
FEATURE [App::DocumentObjectGroupPython] G4_POLYVINYL_ALCOHOL  # scripted group (container) (typed FeaturePython)
  Dunit = g/cm3
  Dvalue = 1.3
  Group = -> [C_element090,H_element082,O_element082]
  conduct = 2
  density = 1
  expand = 3
  formula = G4_POLYVINYL_ALCOHOL
  name = G4_POLYVINYL_ALCOHOL
  specific = 4
FEATURE [App::DocumentObjectGroupPython] C_element091  label="C_element : 049"  # scripted group (container) (typed FeaturePython)
  n = 8
  ref = C_element
FEATURE [App::DocumentObjectGroupPython] H_element083  label="H_element : 045"  # scripted group (container) (typed FeaturePython)
  n = 14
  ref = H_element
FEATURE [App::DocumentObjectGroupPython] O_element083  label="O_element : 044"  # scripted group (container) (typed FeaturePython)
  n = 2
  ref = O_element
FEATURE [App::DocumentObjectGroupPython] G4_POLYVINYL_BUTYRAL  # scripted group (container) (typed FeaturePython)
  Dunit = g/cm3
  Dvalue = 1.12
  Group = -> [C_element091,H_element083,O_element083]
  conduct = 2
  density = 1
  expand = 3
  formula = G4_POLYVINYL_BUTYRAL
  name = G4_POLYVINYL_BUTYRAL
  specific = 4
FEATURE [App::DocumentObjectGroupPython] C_element092  label="C_element : 050"  # scripted group (container) (typed FeaturePython)
  n = 2
  ref = C_element
FEATURE [App::DocumentObjectGroupPython] H_element084  label="H_element : 046"  # scripted group (container) (typed FeaturePython)
  n = 3
  ref = H_element
FEATURE [App::DocumentObjectGroupPython] Cl_element019  label="Cl_element : 009"  # scripted group (container) (typed FeaturePython)
  n = 1
  ref = Cl_element
FEATURE [App::DocumentObjectGroupPython] G4_POLYVINYL_CHLORIDE  # scripted group (container) (typed FeaturePython)
  Dunit = g/cm3
  Dvalue = 1.3
  Group = -> [C_element092,H_element084,Cl_element019]
  conduct = 2
  density = 1
  expand = 3
  formula = G4_POLYVINYL_CHLORIDE
  name = G4_POLYVINYL_CHLORIDE
  specific = 4
FEATURE [App::DocumentObjectGroupPython] C_element093  label="C_element : 051"  # scripted group (container) (typed FeaturePython)
  n = 2
  ref = C_element
FEATURE [App::DocumentObjectGroupPython] H_element085  label="H_element : 047"  # scripted group (container) (typed FeaturePython)
  n = 2
  ref = H_element
FEATURE [App::DocumentObjectGroupPython] Cl_element020  label="Cl_element : 010"  # scripted group (container) (typed FeaturePython)
  n = 2
  ref = Cl_element
FEATURE [App::DocumentObjectGroupPython] G4_POLYVINYLIDENE_CHLORIDE  # scripted group (container) (typed FeaturePython)
  Dunit = g/cm3
  Dvalue = 1.7
  Group = -> [C_element093,H_element085,Cl_element020]
  conduct = 2
  density = 1
  expand = 3
  formula = G4_POLYVINYLIDENE_CHLORIDE
  name = G4_POLYVINYLIDENE_CHLORIDE
  specific = 4
FEATURE [App::DocumentObjectGroupPython] C_element094  label="C_element : 052"  # scripted group (container) (typed FeaturePython)
  n = 2
  ref = C_element
FEATURE [App::DocumentObjectGroupPython] H_element086  label="H_element : 048"  # scripted group (container) (typed FeaturePython)
  n = 2
  ref = H_element
FEATURE [App::DocumentObjectGroupPython] F_element016  label="F_element : 007"  # scripted group (container) (typed FeaturePython)
  n = 2
  ref = F_element
FEATURE [App::DocumentObjectGroupPython] G4_POLYVINYLIDENE_FLUORIDE  # scripted group (container) (typed FeaturePython)
  Dunit = g/cm3
  Dvalue = 1.76
  Group = -> [C_element094,H_element086,F_element016]
  conduct = 2
  density = 1
  expand = 3
  formula = G4_POLYVINYLIDENE_FLUORIDE
  name = G4_POLYVINYLIDENE_FLUORIDE
  specific = 4
FEATURE [App::DocumentObjectGroupPython] C_element095  label="C_element : 053"  # scripted group (container) (typed FeaturePython)
  n = 6
  ref = C_element
FEATURE [App::DocumentObjectGroupPython] H_element087  label="H_element : 9"  # scripted group (container) (typed FeaturePython)
  n = 9
  ref = H_element
FEATURE [App::DocumentObjectGroupPython] N_element037  label="N_element : 016"  # scripted group (container) (typed FeaturePython)
  n = 1
  ref = N_element
FEATURE [App::DocumentObjectGroupPython] O_element084  label="O_element : 045"  # scripted group (container) (typed FeaturePython)
  n = 1
  ref = O_element
FEATURE [App::DocumentObjectGroupPython] G4_POLYVINYL_PYRROLIDONE  # scripted group (container) (typed FeaturePython)
  Dunit = g/cm3
  Dvalue = 1.25
  Group = -> [C_element095,H_element087,N_element037,O_element084]
  conduct = 2
  density = 1
  expand = 3
  formula = G4_POLYVINYL_PYRROLIDONE
  name = G4_POLYVINYL_PYRROLIDONE
  specific = 4
FEATURE [App::DocumentObjectGroupPython] K_element008  label="K_element : 1"  # scripted group (container) (typed FeaturePython)
  n = 1
  ref = K_element
FEATURE [App::DocumentObjectGroupPython] I_element006  label="I_element : 003"  # scripted group (container) (typed FeaturePython)
  n = 1
  ref = I_element
FEATURE [App::DocumentObjectGroupPython] G4_POTASSIUM_IODIDE  # scripted group (container) (typed FeaturePython)
  Dunit = g/cm3
  Dvalue = 3.13
  Group = -> [K_element008,I_element006]
  conduct = 2
  density = 1
  expand = 3
  formula = G4_POTASSIUM_IODIDE
  name = G4_POTASSIUM_IODIDE
  specific = 4
FEATURE [App::DocumentObjectGroupPython] K_element009  label="K_element : 2"  # scripted group (container) (typed FeaturePython)
  n = 2
  ref = K_element
FEATURE [App::DocumentObjectGroupPython] O_element085  label="O_element : 046"  # scripted group (container) (typed FeaturePython)
  n = 1
  ref = O_element
FEATURE [App::DocumentObjectGroupPython] G4_POTASSIUM_OXIDE  # scripted group (container) (typed FeaturePython)
  Dunit = g/cm3
  Dvalue = 2.32
  Group = -> [K_element009,O_element085]
  conduct = 2
  density = 1
  expand = 3
  formula = G4_POTASSIUM_OXIDE
  name = G4_POTASSIUM_OXIDE
  specific = 4
FEATURE [App::DocumentObjectGroupPython] C_element096  label="C_element : 054"  # scripted group (container) (typed FeaturePython)
  n = 3
  ref = C_element
FEATURE [App::DocumentObjectGroupPython] H_element088  label="H_element : 049"  # scripted group (container) (typed FeaturePython)
  n = 8
  ref = H_element
FEATURE [App::DocumentObjectGroupPython] G4_PROPANE  # scripted group (container) (typed FeaturePython)
  Dunit = g/cm3
  Dvalue = 0.00187939
  Group = -> [C_element096,H_element088]
  conduct = 2
  density = 1
  expand = 3
  formula = G4_PROPANE
  name = G4_PROPANE
  specific = 4
FEATURE [App::DocumentObjectGroupPython] C_element097  label="C_element : 055"  # scripted group (container) (typed FeaturePython)
  n = 3
  ref = C_element
FEATURE [App::DocumentObjectGroupPython] H_element089  label="H_element : 050"  # scripted group (container) (typed FeaturePython)
  n = 8
  ref = H_element
FEATURE [App::DocumentObjectGroupPython] G4_lPROPANE  # scripted group (container) (typed FeaturePython)
  Dunit = g/cm3
  Dvalue = 0.43
  Group = -> [C_element097,H_element089]
  conduct = 2
  density = 1
  expand = 3
  formula = G4_lPROPANE
  name = G4_lPROPANE
  specific = 4
FEATURE [App::DocumentObjectGroupPython] C_element098  label="C_element : 056"  # scripted group (container) (typed FeaturePython)
  n = 3
  ref = C_element
FEATURE [App::DocumentObjectGroupPython] H_element090  label="H_element : 051"  # scripted group (container) (typed FeaturePython)
  n = 8
  ref = H_element
FEATURE [App::DocumentObjectGroupPython] O_element086  label="O_element : 047"  # scripted group (container) (typed FeaturePython)
  n = 1
  ref = O_element
FEATURE [App::DocumentObjectGroupPython] G4_N_PROPYL_ALCOHOL  label="G4_N-PROPYL_ALCOHOL"  # scripted group (container) (typed FeaturePython)
  Dunit = g/cm3
  Dvalue = 0.8035
  Group = -> [C_element098,H_element090,O_element086]
  conduct = 2
  density = 1
  expand = 3
  formula = G4_N-PROPYL_ALCOHOL
  name = G4_N-PROPYL_ALCOHOL
  specific = 4
FEATURE [App::DocumentObjectGroupPython] C_element099  label="C_element : 057"  # scripted group (container) (typed FeaturePython)
  n = 5
  ref = C_element
FEATURE [App::DocumentObjectGroupPython] H_element091  label="H_element : 052"  # scripted group (container) (typed FeaturePython)
  n = 5
  ref = H_element
FEATURE [App::DocumentObjectGroupPython] N_element038  label="N_element : 017"  # scripted group (container) (typed FeaturePython)
  n = 1
  ref = N_element
FEATURE [App::DocumentObjectGroupPython] G4_PYRIDINE  # scripted group (container) (typed FeaturePython)
  Dunit = g/cm3
  Dvalue = 0.9819
  Group = -> [C_element099,H_element091,N_element038]
  conduct = 2
  density = 1
  expand = 3
  formula = G4_PYRIDINE
  name = G4_PYRIDINE
  specific = 4
FEATURE [App::DocumentObjectGroupPython] H_element092  label="H_element : 0.144"  # scripted group (container) (typed FeaturePython)
  n = 0.143711
FEATURE [App::DocumentObjectGroupPython] C_element100  label="C_element : 0.856"  # scripted group (container) (typed FeaturePython)
  n = 0.856289
FEATURE [App::DocumentObjectGroupPython] G4_RUBBER_BUTYL  # scripted group (container) (typed FeaturePython)
  Dunit = g/cm3
  Dvalue = 0.92
  Group = -> [H_element092,C_element100]
  conduct = 2
  density = 1
  expand = 3
  formula = G4_RUBBER_BUTYL
  name = G4_RUBBER_BUTYL
  specific = 4
FEATURE [App::DocumentObjectGroupPython] H_element093  label="H_element : 0.118"  # scripted group (container) (typed FeaturePython)
  n = 0.118371
FEATURE [App::DocumentObjectGroupPython] C_element101  label="C_element : 0.882"  # scripted group (container) (typed FeaturePython)
  n = 0.881629
FEATURE [App::DocumentObjectGroupPython] G4_RUBBER_NATURAL  # scripted group (container) (typed FeaturePython)
  Dunit = g/cm3
  Dvalue = 0.92
  Group = -> [H_element093,C_element101]
  conduct = 2
  density = 1
  expand = 3
  formula = G4_RUBBER_NATURAL
  name = G4_RUBBER_NATURAL
  specific = 4
FEATURE [App::DocumentObjectGroupPython] H_element094  label="H_element : 0.145"  # scripted group (container) (typed FeaturePython)
  n = 0.05692
FEATURE [App::DocumentObjectGroupPython] C_element102  label="C_element : 0.543"  # scripted group (container) (typed FeaturePython)
  n = 0.542646
FEATURE [App::DocumentObjectGroupPython] Cl_element021  label="Cl_element : 0.400"  # scripted group (container) (typed FeaturePython)
  n = 0.400434
FEATURE [App::DocumentObjectGroupPython] G4_RUBBER_NEOPRENE  # scripted group (container) (typed FeaturePython)
  Dunit = g/cm3
  Dvalue = 1.23
  Group = -> [H_element094,C_element102,Cl_element021]
  conduct = 2
  density = 1
  expand = 3
  formula = G4_RUBBER_NEOPRENE
  name = G4_RUBBER_NEOPRENE
  specific = 4
FEATURE [App::DocumentObjectGroupPython] Si_element006  label="Si_element : 1"  # scripted group (container) (typed FeaturePython)
  n = 1
  ref = Si_element
FEATURE [App::DocumentObjectGroupPython] O_element087  label="O_element : 048"  # scripted group (container) (typed FeaturePython)
  n = 2
  ref = O_element
FEATURE [App::DocumentObjectGroupPython] G4_SILICON_DIOXIDE  # scripted group (container) (typed FeaturePython)
  Dunit = g/cm3
  Dvalue = 2.32
  Group = -> [Si_element006,O_element087]
  conduct = 2
  density = 1
  expand = 3
  formula = G4_SILICON_DIOXIDE
  name = G4_SILICON_DIOXIDE
  specific = 4
FEATURE [App::DocumentObjectGroupPython] Ag_element002  label="Ag_element : 1"  # scripted group (container) (typed FeaturePython)
  n = 1
  ref = Ag_element
FEATURE [App::DocumentObjectGroupPython] Br_element005  label="Br_element : 003"  # scripted group (container) (typed FeaturePython)
  n = 1
  ref = Br_element
FEATURE [App::DocumentObjectGroupPython] G4_SILVER_BROMIDE  # scripted group (container) (typed FeaturePython)
  Dunit = g/cm3
  Dvalue = 6.473
  Group = -> [Ag_element002,Br_element005]
  conduct = 2
  density = 1
  expand = 3
  formula = G4_SILVER_BROMIDE
  name = G4_SILVER_BROMIDE
  specific = 4
FEATURE [App::DocumentObjectGroupPython] Ag_element003  label="Ag_element : 002"  # scripted group (container) (typed FeaturePython)
  n = 1
  ref = Ag_element
FEATURE [App::DocumentObjectGroupPython] Cl_element022  label="Cl_element : 011"  # scripted group (container) (typed FeaturePython)
  n = 1
  ref = Cl_element
FEATURE [App::DocumentObjectGroupPython] G4_SILVER_CHLORIDE  # scripted group (container) (typed FeaturePython)
  Dunit = g/cm3
  Dvalue = 5.56
  Group = -> [Ag_element003,Cl_element022]
  conduct = 2
  density = 1
  expand = 3
  formula = G4_SILVER_CHLORIDE
  name = G4_SILVER_CHLORIDE
  specific = 4
FEATURE [App::DocumentObjectGroupPython] Br_element006  label="Br_element : 0.423"  # scripted group (container) (typed FeaturePython)
  n = 0.422895
FEATURE [App::DocumentObjectGroupPython] Ag_element004  label="Ag_element : 0.574"  # scripted group (container) (typed FeaturePython)
  n = 0.573748
FEATURE [App::DocumentObjectGroupPython] I_element007  label="I_element : 0.649"  # scripted group (container) (typed FeaturePython)
  n = 0.003357
FEATURE [App::DocumentObjectGroupPython] G4_SILVER_HALIDES  # scripted group (container) (typed FeaturePython)
  Dunit = g/cm3
  Dvalue = 6.47
  Group = -> [Br_element006,Ag_element004,I_element007]
  conduct = 2
  density = 1
  expand = 3
  formula = G4_SILVER_HALIDES
  name = G4_SILVER_HALIDES
  specific = 4
FEATURE [App::DocumentObjectGroupPython] Ag_element005  label="Ag_element : 003"  # scripted group (container) (typed FeaturePython)
  n = 1
  ref = Ag_element
FEATURE [App::DocumentObjectGroupPython] I_element008  label="I_element : 004"  # scripted group (container) (typed FeaturePython)
  n = 1
  ref = I_element
FEATURE [App::DocumentObjectGroupPython] G4_SILVER_IODIDE  # scripted group (container) (typed FeaturePython)
  Dunit = g/cm3
  Dvalue = 6.01
  Group = -> [Ag_element005,I_element008]
  conduct = 2
  density = 1
  expand = 3
  formula = G4_SILVER_IODIDE
  name = G4_SILVER_IODIDE
  specific = 4
FEATURE [App::DocumentObjectGroupPython] H_element095  label="H_element : 0.100"  # scripted group (container) (typed FeaturePython)
  n = 0.1
FEATURE [App::DocumentObjectGroupPython] C_element103  label="C_element : 0.204"  # scripted group (container) (typed FeaturePython)
  n = 0.204
FEATURE [App::DocumentObjectGroupPython] N_element039  label="N_element : 0.759"  # scripted group (container) (typed FeaturePython)
  n = 0.042
FEATURE [App::DocumentObjectGroupPython] O_element088  label="O_element : 0.645"  # scripted group (container) (typed FeaturePython)
  n = 0.645
FEATURE [App::DocumentObjectGroupPython] Na_element013  label="Na_element : 0.100"  # scripted group (container) (typed FeaturePython)
  n = 0.002
FEATURE [App::DocumentObjectGroupPython] P_element009  label="P_element : 0.107"  # scripted group (container) (typed FeaturePython)
  n = 0.001
FEATURE [App::DocumentObjectGroupPython] S_element020  label="S_element : 0.021"  # scripted group (container) (typed FeaturePython)
  n = 0.002
FEATURE [App::DocumentObjectGroupPython] Cl_element023  label="Cl_element : 0.590"  # scripted group (container) (typed FeaturePython)
  n = 0.003
FEATURE [App::DocumentObjectGroupPython] K_element010  label="K_element : 0.001"  # scripted group (container) (typed FeaturePython)
  n = 0.001
FEATURE [App::DocumentObjectGroupPython] G4_SKIN_ICRP  # scripted group (container) (typed FeaturePython)
  Dunit = g/cm3
  Dvalue = 1.09
  Group = -> [H_element095,C_element103,N_element039,O_element088,Na_element013,P_element009,S_element020,Cl_element023,K_element010]
  conduct = 2
  density = 1
  expand = 3
  formula = G4_SKIN_ICRP
  name = G4_SKIN_ICRP
  specific = 4
FEATURE [App::DocumentObjectGroupPython] Na_element014  label="Na_element : 2"  # scripted group (container) (typed FeaturePython)
  n = 2
  ref = Na_element
FEATURE [App::DocumentObjectGroupPython] C_element104  label="C_element : 058"  # scripted group (container) (typed FeaturePython)
  n = 1
  ref = C_element
FEATURE [App::DocumentObjectGroupPython] O_element089  label="O_element : 049"  # scripted group (container) (typed FeaturePython)
  n = 3
  ref = O_element
FEATURE [App::DocumentObjectGroupPython] G4_SODIUM_CARBONATE  # scripted group (container) (typed FeaturePython)
  Dunit = g/cm3
  Dvalue = 2.532
  Group = -> [Na_element014,C_element104,O_element089]
  conduct = 2
  density = 1
  expand = 3
  formula = G4_SODIUM_CARBONATE
  name = G4_SODIUM_CARBONATE
  specific = 4
FEATURE [App::DocumentObjectGroupPython] Na_element015  label="Na_element : 1"  # scripted group (container) (typed FeaturePython)
  n = 1
  ref = Na_element
FEATURE [App::DocumentObjectGroupPython] I_element009  label="I_element : 005"  # scripted group (container) (typed FeaturePython)
  n = 1
  ref = I_element
FEATURE [App::DocumentObjectGroupPython] G4_SODIUM_IODIDE  # scripted group (container) (typed FeaturePython)
  Dunit = g/cm3
  Dvalue = 3.667
  Group = -> [Na_element015,I_element009]
  conduct = 2
  density = 1
  expand = 3
  formula = G4_SODIUM_IODIDE
  name = G4_SODIUM_IODIDE
  specific = 4
FEATURE [App::DocumentObjectGroupPython] Na_element016  label="Na_element : 003"  # scripted group (container) (typed FeaturePython)
  n = 2
  ref = Na_element
FEATURE [App::DocumentObjectGroupPython] O_element090  label="O_element : 050"  # scripted group (container) (typed FeaturePython)
  n = 1
  ref = O_element
FEATURE [App::DocumentObjectGroupPython] G4_SODIUM_MONOXIDE  # scripted group (container) (typed FeaturePython)
  Dunit = g/cm3
  Dvalue = 2.27
  Group = -> [Na_element016,O_element090]
  conduct = 2
  density = 1
  expand = 3
  formula = G4_SODIUM_MONOXIDE
  name = G4_SODIUM_MONOXIDE
  specific = 4
FEATURE [App::DocumentObjectGroupPython] Na_element017  label="Na_element : 004"  # scripted group (container) (typed FeaturePython)
  n = 1
  ref = Na_element
FEATURE [App::DocumentObjectGroupPython] N_element040  label="N_element : 018"  # scripted group (container) (typed FeaturePython)
  n = 1
  ref = N_element
FEATURE [App::DocumentObjectGroupPython] O_element091  label="O_element : 051"  # scripted group (container) (typed FeaturePython)
  n = 3
  ref = O_element
FEATURE [App::DocumentObjectGroupPython] G4_SODIUM_NITRATE  # scripted group (container) (typed FeaturePython)
  Dunit = g/cm3
  Dvalue = 2.261
  Group = -> [Na_element017,N_element040,O_element091]
  conduct = 2
  density = 1
  expand = 3
  formula = G4_SODIUM_NITRATE
  name = G4_SODIUM_NITRATE
  specific = 4
FEATURE [App::DocumentObjectGroupPython] C_element105  label="C_element : 059"  # scripted group (container) (typed FeaturePython)
  n = 14
  ref = C_element
FEATURE [App::DocumentObjectGroupPython] H_element096  label="H_element : 053"  # scripted group (container) (typed FeaturePython)
  n = 12
  ref = H_element
FEATURE [App::DocumentObjectGroupPython] G4_STILBENE  # scripted group (container) (typed FeaturePython)
  Dunit = g/cm3
  Dvalue = 0.9707
  Group = -> [C_element105,H_element096]
  conduct = 2
  density = 1
  expand = 3
  formula = G4_STILBENE
  name = G4_STILBENE
  specific = 4
FEATURE [App::DocumentObjectGroupPython] C_element106  label="C_element : 12"  # scripted group (container) (typed FeaturePython)
  n = 12
  ref = C_element
FEATURE [App::DocumentObjectGroupPython] H_element097  label="H_element : 22"  # scripted group (container) (typed FeaturePython)
  n = 22
  ref = H_element
FEATURE [App::DocumentObjectGroupPython] O_element092  label="O_element : 11"  # scripted group (container) (typed FeaturePython)
  n = 11
  ref = O_element
FEATURE [App::DocumentObjectGroupPython] G4_SUCROSE  # scripted group (container) (typed FeaturePython)
  Dunit = g/cm3
  Dvalue = 1.5805
  Group = -> [C_element106,H_element097,O_element092]
  conduct = 2
  density = 1
  expand = 3
  formula = G4_SUCROSE
  name = G4_SUCROSE
  specific = 4
FEATURE [App::DocumentObjectGroupPython] C_element107  label="C_element : 18"  # scripted group (container) (typed FeaturePython)
  n = 18
  ref = C_element
FEATURE [App::DocumentObjectGroupPython] H_element098  label="H_element : 054"  # scripted group (container) (typed FeaturePython)
  n = 14
  ref = H_element
FEATURE [App::DocumentObjectGroupPython] G4_TERPHENYL  # scripted group (container) (typed FeaturePython)
  Dunit = g/cm3
  Dvalue = 1.24
  Group = -> [C_element107,H_element098]
  conduct = 2
  density = 1
  expand = 3
  formula = G4_TERPHENYL
  name = G4_TERPHENYL
  specific = 4
FEATURE [App::DocumentObjectGroupPython] H_element099  label="H_element : 0.146"  # scripted group (container) (typed FeaturePython)
  n = 0.106
FEATURE [App::DocumentObjectGroupPython] C_element108  label="C_element : 0.883"  # scripted group (container) (typed FeaturePython)
  n = 0.099
FEATURE [App::DocumentObjectGroupPython] N_element041  label="N_element : 0.020"  # scripted group (container) (typed FeaturePython)
  n = 0.02
FEATURE [App::DocumentObjectGroupPython] O_element093  label="O_element : 0.766"  # scripted group (container) (typed FeaturePython)
  n = 0.766
FEATURE [App::DocumentObjectGroupPython] Na_element018  label="Na_element : 0.101"  # scripted group (container) (typed FeaturePython)
  n = 0.002
FEATURE [App::DocumentObjectGroupPython] P_element010  label="P_element : 0.108"  # scripted group (container) (typed FeaturePython)
  n = 0.001
FEATURE [App::DocumentObjectGroupPython] S_element021  label="S_element : 0.022"  # scripted group (container) (typed FeaturePython)
  n = 0.002
FEATURE [App::DocumentObjectGroupPython] Cl_element024  label="Cl_element : 0.002"  # scripted group (container) (typed FeaturePython)
  n = 0.002
FEATURE [App::DocumentObjectGroupPython] K_element011  label="K_element : 0.017"  # scripted group (container) (typed FeaturePython)
  n = 0.002
FEATURE [App::DocumentObjectGroupPython] G4_TESTIS_ICRP  # scripted group (container) (typed FeaturePython)
  Dunit = g/cm3
  Dvalue = 1.04
  Group = -> [H_element099,C_element108,N_element041,O_element093,Na_element018,P_element010,S_element021,Cl_element024,K_element011]
  conduct = 2
  density = 1
  expand = 3
  formula = G4_TESTIS_ICRP
  name = G4_TESTIS_ICRP
  specific = 4
FEATURE [App::DocumentObjectGroupPython] C_element109  label="C_element : 060"  # scripted group (container) (typed FeaturePython)
  n = 2
  ref = C_element
FEATURE [App::DocumentObjectGroupPython] Cl_element025  label="Cl_element : 012"  # scripted group (container) (typed FeaturePython)
  n = 4
  ref = Cl_element
FEATURE [App::DocumentObjectGroupPython] G4_TETRACHLOROETHYLENE  # scripted group (container) (typed FeaturePython)
  Dunit = g/cm3
  Dvalue = 1.625
  Group = -> [C_element109,Cl_element025]
  conduct = 2
  density = 1
  expand = 3
  formula = G4_TETRACHLOROETHYLENE
  name = G4_TETRACHLOROETHYLENE
  specific = 4
FEATURE [App::DocumentObjectGroupPython] Tl_element001  label="Tl_element : 1"  # scripted group (container) (typed FeaturePython)
  n = 1
  ref = Tl_element
FEATURE [App::DocumentObjectGroupPython] Cl_element026  label="Cl_element : 013"  # scripted group (container) (typed FeaturePython)
  n = 1
  ref = Cl_element
FEATURE [App::DocumentObjectGroupPython] G4_THALLIUM_CHLORIDE  # scripted group (container) (typed FeaturePython)
  Dunit = g/cm3
  Dvalue = 7.004
  Group = -> [Tl_element001,Cl_element026]
  conduct = 2
  density = 1
  expand = 3
  formula = G4_THALLIUM_CHLORIDE
  name = G4_THALLIUM_CHLORIDE
  specific = 4
FEATURE [App::DocumentObjectGroupPython] H_element100  label="H_element : 0.147"  # scripted group (container) (typed FeaturePython)
  n = 0.105
FEATURE [App::DocumentObjectGroupPython] C_element110  label="C_element : 0.256"  # scripted group (container) (typed FeaturePython)
  n = 0.256
FEATURE [App::DocumentObjectGroupPython] N_element042  label="N_element : 0.760"  # scripted group (container) (typed FeaturePython)
  n = 0.027
FEATURE [App::DocumentObjectGroupPython] O_element094  label="O_element : 0.602"  # scripted group (container) (typed FeaturePython)
  n = 0.602
FEATURE [App::DocumentObjectGroupPython] Na_element019  label="Na_element : 0.102"  # scripted group (container) (typed FeaturePython)
  n = 0.001
FEATURE [App::DocumentObjectGroupPython] P_element011  label="P_element : 0.109"  # scripted group (container) (typed FeaturePython)
  n = 0.002
FEATURE [App::DocumentObjectGroupPython] S_element022  label="S_element : 0.023"  # scripted group (container) (typed FeaturePython)
  n = 0.003
FEATURE [App::DocumentObjectGroupPython] Cl_element027  label="Cl_element : 0.591"  # scripted group (container) (typed FeaturePython)
  n = 0.002
FEATURE [App::DocumentObjectGroupPython] K_element012  label="K_element : 0.018"  # scripted group (container) (typed FeaturePython)
  n = 0.002
FEATURE [App::DocumentObjectGroupPython] G4_TISSUE_SOFT_ICRP  # scripted group (container) (typed FeaturePython)
  Dunit = g/cm3
  Dvalue = 1.03
  Group = -> [H_element100,C_element110,N_element042,O_element094,Na_element019,P_element011,S_element022,Cl_element027,K_element012]
  conduct = 2
  density = 1
  expand = 3
  formula = G4_TISSUE_SOFT_ICRP
  name = G4_TISSUE_SOFT_ICRP
  specific = 4
FEATURE [App::DocumentObjectGroupPython] H_element101  label="H_element : 0.148"  # scripted group (container) (typed FeaturePython)
  n = 0.101
FEATURE [App::DocumentObjectGroupPython] C_element111  label="C_element : 0.111"  # scripted group (container) (typed FeaturePython)
  n = 0.111
FEATURE [App::DocumentObjectGroupPython] N_element043  label="N_element : 0.026"  # scripted group (container) (typed FeaturePython)
  n = 0.026
FEATURE [App::DocumentObjectGroupPython] O_element095  label="O_element : 0.762"  # scripted group (container) (typed FeaturePython)
  n = 0.762
FEATURE [App::DocumentObjectGroupPython] G4_TISSUE_SOFT_ICRU_4  label="G4_TISSUE_SOFT_ICRU-4"  # scripted group (container) (typed FeaturePython)
  Dunit = g/cm3
  Dvalue = 1
  Group = -> [H_element101,C_element111,N_element043,O_element095]
  conduct = 2
  density = 1
  expand = 3
  formula = G4_TISSUE_SOFT_ICRU-4
  name = G4_TISSUE_SOFT_ICRU-4
  specific = 4
FEATURE [App::DocumentObjectGroupPython] H_element102  label="H_element : 0.149"  # scripted group (container) (typed FeaturePython)
  n = 0.101869
FEATURE [App::DocumentObjectGroupPython] C_element112  label="C_element : 0.456"  # scripted group (container) (typed FeaturePython)
  n = 0.456179
FEATURE [App::DocumentObjectGroupPython] N_element044  label="N_element : 0.761"  # scripted group (container) (typed FeaturePython)
  n = 0.035172
FEATURE [App::DocumentObjectGroupPython] O_element096  label="O_element : 0.407"  # scripted group (container) (typed FeaturePython)
  n = 0.40678
FEATURE [App::DocumentObjectGroupPython] G4_TISSUE_METHANE  label="G4_TISSUE-METHANE"  # scripted group (container) (typed FeaturePython)
  Dunit = g/cm3
  Dvalue = 0.00106409
  Group = -> [H_element102,C_element112,N_element044,O_element096]
  conduct = 2
  density = 1
  expand = 3
  formula = G4_TISSUE-METHANE
  name = G4_TISSUE-METHANE
  specific = 4
FEATURE [App::DocumentObjectGroupPython] H_element103  label="H_element : 0.103"  # scripted group (container) (typed FeaturePython)
  n = 0.102672
FEATURE [App::DocumentObjectGroupPython] C_element113  label="C_element : 0.569"  # scripted group (container) (typed FeaturePython)
  n = 0.56894
FEATURE [App::DocumentObjectGroupPython] N_element045  label="N_element : 0.762"  # scripted group (container) (typed FeaturePython)
  n = 0.035022
FEATURE [App::DocumentObjectGroupPython] O_element097  label="O_element : 0.293"  # scripted group (container) (typed FeaturePython)
  n = 0.293366
FEATURE [App::DocumentObjectGroupPython] G4_TISSUE_PROPANE  label="G4_TISSUE-PROPANE"  # scripted group (container) (typed FeaturePython)
  Dunit = g/cm3
  Dvalue = 0.00182628
  Group = -> [H_element103,C_element113,N_element045,O_element097]
  conduct = 2
  density = 1
  expand = 3
  formula = G4_TISSUE-PROPANE
  name = G4_TISSUE-PROPANE
  specific = 4
FEATURE [App::DocumentObjectGroupPython] Ti_element003  label="Ti_element : 1"  # scripted group (container) (typed FeaturePython)
  n = 1
  ref = Ti_element
FEATURE [App::DocumentObjectGroupPython] O_element098  label="O_element : 052"  # scripted group (container) (typed FeaturePython)
  n = 2
  ref = O_element
FEATURE [App::DocumentObjectGroupPython] G4_TITANIUM_DIOXIDE  # scripted group (container) (typed FeaturePython)
  Dunit = g/cm3
  Dvalue = 4.26
  Group = -> [Ti_element003,O_element098]
  conduct = 2
  density = 1
  expand = 3
  formula = G4_TITANIUM_DIOXIDE
  name = G4_TITANIUM_DIOXIDE
  specific = 4
FEATURE [App::DocumentObjectGroupPython] C_element114  label="C_element : 061"  # scripted group (container) (typed FeaturePython)
  n = 7
  ref = C_element
FEATURE [App::DocumentObjectGroupPython] H_element104  label="H_element : 055"  # scripted group (container) (typed FeaturePython)
  n = 8
  ref = H_element
FEATURE [App::DocumentObjectGroupPython] G4_TOLUENE  # scripted group (container) (typed FeaturePython)
  Dunit = g/cm3
  Dvalue = 0.8669
  Group = -> [C_element114,H_element104]
  conduct = 2
  density = 1
  expand = 3
  formula = G4_TOLUENE
  name = G4_TOLUENE
  specific = 4
FEATURE [App::DocumentObjectGroupPython] C_element115  label="C_element : 062"  # scripted group (container) (typed FeaturePython)
  n = 2
  ref = C_element
FEATURE [App::DocumentObjectGroupPython] H_element105  label="H_element : 056"  # scripted group (container) (typed FeaturePython)
  n = 1
  ref = H_element
FEATURE [App::DocumentObjectGroupPython] Cl_element028  label="Cl_element : 014"  # scripted group (container) (typed FeaturePython)
  n = 3
  ref = Cl_element
FEATURE [App::DocumentObjectGroupPython] G4_TRICHLOROETHYLENE  # scripted group (container) (typed FeaturePython)
  Dunit = g/cm3
  Dvalue = 1.46
  Group = -> [C_element115,H_element105,Cl_element028]
  conduct = 2
  density = 1
  expand = 3
  formula = G4_TRICHLOROETHYLENE
  name = G4_TRICHLOROETHYLENE
  specific = 4
FEATURE [App::DocumentObjectGroupPython] C_element116  label="C_element : 063"  # scripted group (container) (typed FeaturePython)
  n = 6
  ref = C_element
FEATURE [App::DocumentObjectGroupPython] H_element106  label="H_element : 15"  # scripted group (container) (typed FeaturePython)
  n = 15
  ref = H_element
FEATURE [App::DocumentObjectGroupPython] O_element099  label="O_element : 053"  # scripted group (container) (typed FeaturePython)
  n = 4
  ref = O_element
FEATURE [App::DocumentObjectGroupPython] P_element012  label="P_element : 1"  # scripted group (container) (typed FeaturePython)
  n = 1
  ref = P_element
FEATURE [App::DocumentObjectGroupPython] G4_TRIETHYL_PHOSPHATE  # scripted group (container) (typed FeaturePython)
  Dunit = g/cm3
  Dvalue = 1.07
  Group = -> [C_element116,H_element106,O_element099,P_element012]
  conduct = 2
  density = 1
  expand = 3
  formula = G4_TRIETHYL_PHOSPHATE
  name = G4_TRIETHYL_PHOSPHATE
  specific = 4
FEATURE [App::DocumentObjectGroupPython] W_element003  label="W_element : 003"  # scripted group (container) (typed FeaturePython)
  n = 1
  ref = W_element
FEATURE [App::DocumentObjectGroupPython] F_element017  label="F_element : 6"  # scripted group (container) (typed FeaturePython)
  n = 6
  ref = F_element
FEATURE [App::DocumentObjectGroupPython] G4_TUNGSTEN_HEXAFLUORIDE  # scripted group (container) (typed FeaturePython)
  Dunit = g/cm3
  Dvalue = 2.4
  Group = -> [W_element003,F_element017]
  conduct = 2
  density = 1
  expand = 3
  formula = G4_TUNGSTEN_HEXAFLUORIDE
  name = G4_TUNGSTEN_HEXAFLUORIDE
  specific = 4
FEATURE [App::DocumentObjectGroupPython] U_element001  label="U_element : 1"  # scripted group (container) (typed FeaturePython)
  n = 1
  ref = U_element
FEATURE [App::DocumentObjectGroupPython] C_element117  label="C_element : 064"  # scripted group (container) (typed FeaturePython)
  n = 2
  ref = C_element
FEATURE [App::DocumentObjectGroupPython] G4_URANIUM_DICARBIDE  # scripted group (container) (typed FeaturePython)
  Dunit = g/cm3
  Dvalue = 11.28
  Group = -> [U_element001,C_element117]
  conduct = 2
  density = 1
  expand = 3
  formula = G4_URANIUM_DICARBIDE
  name = G4_URANIUM_DICARBIDE
  specific = 4
FEATURE [App::DocumentObjectGroupPython] U_element002  label="U_element : 002"  # scripted group (container) (typed FeaturePython)
  n = 1
  ref = U_element
FEATURE [App::DocumentObjectGroupPython] C_element118  label="C_element : 065"  # scripted group (container) (typed FeaturePython)
  n = 1
  ref = C_element
FEATURE [App::DocumentObjectGroupPython] G4_URANIUM_MONOCARBIDE  # scripted group (container) (typed FeaturePython)
  Dunit = g/cm3
  Dvalue = 13.63
  Group = -> [U_element002,C_element118]
  conduct = 2
  density = 1
  expand = 3
  formula = G4_URANIUM_MONOCARBIDE
  name = G4_URANIUM_MONOCARBIDE
  specific = 4
FEATURE [App::DocumentObjectGroupPython] U_element003  label="U_element : 003"  # scripted group (container) (typed FeaturePython)
  n = 1
  ref = U_element
FEATURE [App::DocumentObjectGroupPython] O_element100  label="O_element : 054"  # scripted group (container) (typed FeaturePython)
  n = 2
  ref = O_element
FEATURE [App::DocumentObjectGroupPython] G4_URANIUM_OXIDE  # scripted group (container) (typed FeaturePython)
  Dunit = g/cm3
  Dvalue = 10.96
  Group = -> [U_element003,O_element100]
  conduct = 2
  density = 1
  expand = 3
  formula = G4_URANIUM_OXIDE
  name = G4_URANIUM_OXIDE
  specific = 4
FEATURE [App::DocumentObjectGroupPython] C_element119  label="C_element : 066"  # scripted group (container) (typed FeaturePython)
  n = 1
  ref = C_element
FEATURE [App::DocumentObjectGroupPython] H_element107  label="H_element : 057"  # scripted group (container) (typed FeaturePython)
  n = 4
  ref = H_element
FEATURE [App::DocumentObjectGroupPython] N_element046  label="N_element : 019"  # scripted group (container) (typed FeaturePython)
  n = 2
  ref = N_element
FEATURE [App::DocumentObjectGroupPython] O_element101  label="O_element : 055"  # scripted group (container) (typed FeaturePython)
  n = 1
  ref = O_element
FEATURE [App::DocumentObjectGroupPython] G4_UREA  # scripted group (container) (typed FeaturePython)
  Dunit = g/cm3
  Dvalue = 1.323
  Group = -> [C_element119,H_element107,N_element046,O_element101]
  conduct = 2
  density = 1
  expand = 3
  formula = G4_UREA
  name = G4_UREA
  specific = 4
FEATURE [App::DocumentObjectGroupPython] C_element120  label="C_element : 067"  # scripted group (container) (typed FeaturePython)
  n = 5
  ref = C_element
FEATURE [App::DocumentObjectGroupPython] H_element108  label="H_element : 058"  # scripted group (container) (typed FeaturePython)
  n = 11
  ref = H_element
FEATURE [App::DocumentObjectGroupPython] N_element047  label="N_element : 020"  # scripted group (container) (typed FeaturePython)
  n = 1
  ref = N_element
FEATURE [App::DocumentObjectGroupPython] O_element102  label="O_element : 056"  # scripted group (container) (typed FeaturePython)
  n = 2
  ref = O_element
FEATURE [App::DocumentObjectGroupPython] G4_VALINE  # scripted group (container) (typed FeaturePython)
  Dunit = g/cm3
  Dvalue = 1.23
  Group = -> [C_element120,H_element108,N_element047,O_element102]
  conduct = 2
  density = 1
  expand = 3
  formula = G4_VALINE
  name = G4_VALINE
  specific = 4
FEATURE [App::DocumentObjectGroupPython] H_element109  label="H_element : 0.009"  # scripted group (container) (typed FeaturePython)
  n = 0.009417
FEATURE [App::DocumentObjectGroupPython] C_element121  label="C_element : 0.281"  # scripted group (container) (typed FeaturePython)
  n = 0.280555
FEATURE [App::DocumentObjectGroupPython] F_element018  label="F_element : 0.710"  # scripted group (container) (typed FeaturePython)
  n = 0.710028
FEATURE [App::DocumentObjectGroupPython] G4_VITON  # scripted group (container) (typed FeaturePython)
  Dunit = g/cm3
  Dvalue = 1.8
  Group = -> [H_element109,C_element121,F_element018]
  conduct = 2
  density = 1
  expand = 3
  formula = G4_VITON
  name = G4_VITON
  specific = 4
FEATURE [App::DocumentObjectGroupPython] H_element110  label="H_element : 059"  # scripted group (container) (typed FeaturePython)
  n = 2
  ref = H_element
FEATURE [App::DocumentObjectGroupPython] O_element103  label="O_element : 057"  # scripted group (container) (typed FeaturePython)
  n = 1
  ref = O_element
FEATURE [App::DocumentObjectGroupPython] G4_WATER  # scripted group (container) (typed FeaturePython)
  Dunit = g/cm3
  Dvalue = 1
  Group = -> [H_element110,O_element103]
  conduct = 2
  density = 1
  expand = 3
  formula = G4_WATER
  name = G4_WATER
  specific = 4
FEATURE [App::DocumentObjectGroupPython] H_element111  label="H_element : 060"  # scripted group (container) (typed FeaturePython)
  n = 2
  ref = H_element
FEATURE [App::DocumentObjectGroupPython] O_element104  label="O_element : 058"  # scripted group (container) (typed FeaturePython)
  n = 1
  ref = O_element
FEATURE [App::DocumentObjectGroupPython] G4_WATER_VAPOR  # scripted group (container) (typed FeaturePython)
  Dunit = g/cm3
  Dvalue = 0.000756182
  Group = -> [H_element111,O_element104]
  conduct = 2
  density = 1
  expand = 3
  formula = G4_WATER_VAPOR
  name = G4_WATER_VAPOR
  specific = 4
FEATURE [App::DocumentObjectGroupPython] C_element122  label="C_element : 068"  # scripted group (container) (typed FeaturePython)
  n = 8
  ref = C_element
FEATURE [App::DocumentObjectGroupPython] H_element112  label="H_element : 061"  # scripted group (container) (typed FeaturePython)
  n = 10
  ref = H_element
FEATURE [App::DocumentObjectGroupPython] G4_XYLENE  # scripted group (container) (typed FeaturePython)
  Dunit = g/cm3
  Dvalue = 0.87
  Group = -> [C_element122,H_element112]
  conduct = 2
  density = 1
  expand = 3
  formula = G4_XYLENE
  name = G4_XYLENE
  specific = 4
FEATURE [App::DocumentObjectGroupPython] C_element123  label="C_element : 069"  # scripted group (container) (typed FeaturePython)
  n = 1
  ref = C_element
FEATURE [App::DocumentObjectGroupPython] G4_GRAPHITE  # scripted group (container) (typed FeaturePython)
  Dunit = g/cm3
  Dvalue = 2.21
  Group = -> [C_element123]
  conduct = 2
  density = 1
  expand = 3
  formula = G4_GRAPHITE
  name = G4_GRAPHITE
  specific = 4
FEATURE [App::DocumentObjectGroupPython] NIST  # scripted group (container) (typed FeaturePython)
  Group = -> [G4_A_150_TISSUE,G4_ACETONE,G4_ACETYLENE,G4_ADENINE,G4_ADIPOSE_TISSUE_ICRP,G4_AIR,G4_ALANINE,G4_ALUMINUM_OXIDE,G4_AMBER,G4_AMMONIA,G4_ANILINE,G4_ANTHRACENE,G4_B_100_BONE,G4_BAKELITE,G4_BARIUM_FLUORIDE,G4_BARIUM_SULFATE,G4_BENZENE,G4_BERYLLIUM_OXIDE,G4_BGO,G4_BLOOD_ICRP,G4_BONE_COMPACT_ICRU,G4_BONE_CORTICAL_ICRP,G4_BORON_CARBIDE,G4_BORON_OXIDE,G4_BRAIN_ICRP,G4_BUTANE,G4_N_BUTYL_ALCOHOL,G4_C_552,+152 more]
FEATURE [App::DocumentObjectGroupPython] H_element113  label="H_element : 062"  # scripted group (container) (typed FeaturePython)
  n = 1
  ref = H_element
FEATURE [App::DocumentObjectGroupPython] G4_H  # scripted group (container) (typed FeaturePython)
  Dunit = g/cm3
  Dvalue = 8.3748e-05
  Group = -> [H_element113]
  conduct = 2
  density = 1
  expand = 3
  formula = H
  name = G4_H
  specific = 4
FEATURE [App::DocumentObjectGroupPython] He_element001  label="He_element : 1"  # scripted group (container) (typed FeaturePython)
  n = 1
  ref = He_element
FEATURE [App::DocumentObjectGroupPython] G4_He  # scripted group (container) (typed FeaturePython)
  Dunit = g/cm3
  Dvalue = 0.000166322
  Group = -> [He_element001]
  conduct = 2
  density = 1
  expand = 3
  formula = He
  name = G4_He
  specific = 4
FEATURE [App::DocumentObjectGroupPython] Li_element008  label="Li_element : 008"  # scripted group (container) (typed FeaturePython)
  n = 1
  ref = Li_element
FEATURE [App::DocumentObjectGroupPython] G4_Li  # scripted group (container) (typed FeaturePython)
  Dunit = g/cm3
  Dvalue = 0.534
  Group = -> [Li_element008]
  conduct = 2
  density = 1
  expand = 3
  formula = Li
  name = G4_Li
  specific = 4
FEATURE [App::DocumentObjectGroupPython] Be_element002  label="Be_element : 002"  # scripted group (container) (typed FeaturePython)
  n = 1
  ref = Be_element
FEATURE [App::DocumentObjectGroupPython] G4_Be  # scripted group (container) (typed FeaturePython)
  Dunit = g/cm3
  Dvalue = 1.848
  Group = -> [Be_element002]
  conduct = 2
  density = 1
  expand = 3
  formula = Be
  name = G4_Be
  specific = 4
FEATURE [App::DocumentObjectGroupPython] B_element007  label="B_element : 007"  # scripted group (container) (typed FeaturePython)
  n = 1
  ref = B_element
FEATURE [App::DocumentObjectGroupPython] G4_B  # scripted group (container) (typed FeaturePython)
  Dunit = g/cm3
  Dvalue = 2.37
  Group = -> [B_element007]
  conduct = 2
  density = 1
  expand = 3
  formula = B
  name = G4_B
  specific = 4
FEATURE [App::DocumentObjectGroupPython] C_element124  label="C_element : 070"  # scripted group (container) (typed FeaturePython)
  n = 1
  ref = C_element
FEATURE [App::DocumentObjectGroupPython] G4_C  # scripted group (container) (typed FeaturePython)
  Dunit = g/cm3
  Dvalue = 2
  Group = -> [C_element124]
  conduct = 2
  density = 1
  expand = 3
  formula = C
  name = G4_C
  specific = 4
FEATURE [App::DocumentObjectGroupPython] N_element048  label="N_element : 021"  # scripted group (container) (typed FeaturePython)
  n = 1
  ref = N_element
FEATURE [App::DocumentObjectGroupPython] G4_N  # scripted group (container) (typed FeaturePython)
  Dunit = g/cm3
  Dvalue = 0.0011652
  Group = -> [N_element048]
  conduct = 2
  density = 1
  expand = 3
  formula = N
  name = G4_N
  specific = 4
FEATURE [App::DocumentObjectGroupPython] O_element105  label="O_element : 059"  # scripted group (container) (typed FeaturePython)
  n = 1
  ref = O_element
FEATURE [App::DocumentObjectGroupPython] G4_O  # scripted group (container) (typed FeaturePython)
  Dunit = g/cm3
  Dvalue = 0.00133151
  Group = -> [O_element105]
  conduct = 2
  density = 1
  expand = 3
  formula = O
  name = G4_O
  specific = 4
FEATURE [App::DocumentObjectGroupPython] F_element019  label="F_element : 008"  # scripted group (container) (typed FeaturePython)
  n = 1
  ref = F_element
FEATURE [App::DocumentObjectGroupPython] G4_F  # scripted group (container) (typed FeaturePython)
  Dunit = g/cm3
  Dvalue = 0.00158029
  Group = -> [F_element019]
  conduct = 2
  density = 1
  expand = 3
  formula = F
  name = G4_F
  specific = 4
FEATURE [App::DocumentObjectGroupPython] Ne_element001  label="Ne_element : 1"  # scripted group (container) (typed FeaturePython)
  n = 1
  ref = Ne_element
FEATURE [App::DocumentObjectGroupPython] G4_Ne  # scripted group (container) (typed FeaturePython)
  Dunit = g/cm3
  Dvalue = 0.000838505
  Group = -> [Ne_element001]
  conduct = 2
  density = 1
  expand = 3
  formula = Ne
  name = G4_Ne
  specific = 4
FEATURE [App::DocumentObjectGroupPython] Na_element020  label="Na_element : 005"  # scripted group (container) (typed FeaturePython)
  n = 1
  ref = Na_element
FEATURE [App::DocumentObjectGroupPython] G4_Na  # scripted group (container) (typed FeaturePython)
  Dunit = g/cm3
  Dvalue = 0.971
  Group = -> [Na_element020]
  conduct = 2
  density = 1
  expand = 3
  formula = Na
  name = G4_Na
  specific = 4
FEATURE [App::DocumentObjectGroupPython] Mg_element011  label="Mg_element : 005"  # scripted group (container) (typed FeaturePython)
  n = 1
  ref = Mg_element
FEATURE [App::DocumentObjectGroupPython] G4_Mg  # scripted group (container) (typed FeaturePython)
  Dunit = g/cm3
  Dvalue = 1.74
  Group = -> [Mg_element011]
  conduct = 2
  density = 1
  expand = 3
  formula = Mg
  name = G4_Mg
  specific = 4
FEATURE [App::DocumentObjectGroupPython] Al_element004  label="Al_element : 1"  # scripted group (container) (typed FeaturePython)
  n = 1
  ref = Al_element
FEATURE [App::DocumentObjectGroupPython] G4_Al  # scripted group (container) (typed FeaturePython)
  Dunit = g/cm3
  Dvalue = 2.699
  Group = -> [Al_element004]
  conduct = 2
  density = 1
  expand = 3
  formula = Al
  name = G4_Al
  specific = 4
FEATURE [App::DocumentObjectGroupPython] Si_element007  label="Si_element : 002"  # scripted group (container) (typed FeaturePython)
  n = 1
  ref = Si_element
FEATURE [App::DocumentObjectGroupPython] G4_Si  # scripted group (container) (typed FeaturePython)
  Dunit = g/cm3
  Dvalue = 2.33
  Group = -> [Si_element007]
  conduct = 2
  density = 1
  expand = 3
  formula = Si
  name = G4_Si
  specific = 4
FEATURE [App::DocumentObjectGroupPython] P_element013  label="P_element : 002"  # scripted group (container) (typed FeaturePython)
  n = 1
  ref = P_element
FEATURE [App::DocumentObjectGroupPython] G4_P  # scripted group (container) (typed FeaturePython)
  Dunit = g/cm3
  Dvalue = 2.2
  Group = -> [P_element013]
  conduct = 2
  density = 1
  expand = 3
  formula = P
  name = G4_P
  specific = 4
FEATURE [App::DocumentObjectGroupPython] S_element023  label="S_element : 007"  # scripted group (container) (typed FeaturePython)
  n = 1
  ref = S_element
FEATURE [App::DocumentObjectGroupPython] G4_S  # scripted group (container) (typed FeaturePython)
  Dunit = g/cm3
  Dvalue = 2
  Group = -> [S_element023]
  conduct = 2
  density = 1
  expand = 3
  formula = S
  name = G4_S
  specific = 4
FEATURE [App::DocumentObjectGroupPython] Cl_element029  label="Cl_element : 015"  # scripted group (container) (typed FeaturePython)
  n = 1
  ref = Cl_element
FEATURE [App::DocumentObjectGroupPython] G4_Cl  # scripted group (container) (typed FeaturePython)
  Dunit = g/cm3
  Dvalue = 0.00299473
  Group = -> [Cl_element029]
  conduct = 2
  density = 1
  expand = 3
  formula = Cl
  name = G4_Cl
  specific = 4
FEATURE [App::DocumentObjectGroupPython] Ar_element002  label="Ar_element : 1"  # scripted group (container) (typed FeaturePython)
  n = 1
  ref = Ar_element
FEATURE [App::DocumentObjectGroupPython] G4_Ar  # scripted group (container) (typed FeaturePython)
  Dunit = g/cm3
  Dvalue = 0.00166201
  Group = -> [Ar_element002]
  conduct = 2
  density = 1
  expand = 3
  formula = Ar
  name = G4_Ar
  specific = 4
FEATURE [App::DocumentObjectGroupPython] K_element013  label="K_element : 003"  # scripted group (container) (typed FeaturePython)
  n = 1
  ref = K_element
FEATURE [App::DocumentObjectGroupPython] G4_K  # scripted group (container) (typed FeaturePython)
  Dunit = g/cm3
  Dvalue = 0.862
  Group = -> [K_element013]
  conduct = 2
  density = 1
  expand = 3
  formula = K
  name = G4_K
  specific = 4
FEATURE [App::DocumentObjectGroupPython] Ca_element014  label="Ca_element : 007"  # scripted group (container) (typed FeaturePython)
  n = 1
  ref = Ca_element
FEATURE [App::DocumentObjectGroupPython] G4_Ca  # scripted group (container) (typed FeaturePython)
  Dunit = g/cm3
  Dvalue = 1.55
  Group = -> [Ca_element014]
  conduct = 2
  density = 1
  expand = 3
  formula = Ca
  name = G4_Ca
  specific = 4
FEATURE [App::DocumentObjectGroupPython] Sc_element001  label="Sc_element : 1"  # scripted group (container) (typed FeaturePython)
  n = 1
  ref = Sc_element
FEATURE [App::DocumentObjectGroupPython] G4_Sc  # scripted group (container) (typed FeaturePython)
  Dunit = g/cm3
  Dvalue = 2.989
  Group = -> [Sc_element001]
  conduct = 2
  density = 1
  expand = 3
  formula = Sc
  name = G4_Sc
  specific = 4
FEATURE [App::DocumentObjectGroupPython] Ti_element004  label="Ti_element : 002"  # scripted group (container) (typed FeaturePython)
  n = 1
  ref = Ti_element
FEATURE [App::DocumentObjectGroupPython] G4_Ti  # scripted group (container) (typed FeaturePython)
  Dunit = g/cm3
  Dvalue = 4.54
  Group = -> [Ti_element004]
  conduct = 2
  density = 1
  expand = 3
  formula = Ti
  name = G4_Ti
  specific = 4
FEATURE [App::DocumentObjectGroupPython] V_element001  label="V_element : 1"  # scripted group (container) (typed FeaturePython)
  n = 1
  ref = V_element
FEATURE [App::DocumentObjectGroupPython] G4_V  # scripted group (container) (typed FeaturePython)
  Dunit = g/cm3
  Dvalue = 6.11
  Group = -> [V_element001]
  conduct = 2
  density = 1
  expand = 3
  formula = V
  name = G4_V
  specific = 4
FEATURE [App::DocumentObjectGroupPython] Cr_element001  label="Cr_element : 1"  # scripted group (container) (typed FeaturePython)
  n = 1
  ref = Cr_element
FEATURE [App::DocumentObjectGroupPython] G4_Cr  # scripted group (container) (typed FeaturePython)
  Dunit = g/cm3
  Dvalue = 7.18
  Group = -> [Cr_element001]
  conduct = 2
  density = 1
  expand = 3
  formula = Cr
  name = G4_Cr
  specific = 4
FEATURE [App::DocumentObjectGroupPython] Mn_element001  label="Mn_element : 1"  # scripted group (container) (typed FeaturePython)
  n = 1
  ref = Mn_element
FEATURE [App::DocumentObjectGroupPython] G4_Mn  # scripted group (container) (typed FeaturePython)
  Dunit = g/cm3
  Dvalue = 7.44
  Group = -> [Mn_element001]
  conduct = 2
  density = 1
  expand = 3
  formula = Mn
  name = G4_Mn
  specific = 4
FEATURE [App::DocumentObjectGroupPython] Fe_element007  label="Fe_element : 004"  # scripted group (container) (typed FeaturePython)
  n = 1
  ref = Fe_element
FEATURE [App::DocumentObjectGroupPython] G4_Fe  # scripted group (container) (typed FeaturePython)
  Dunit = g/cm3
  Dvalue = 7.874
  Group = -> [Fe_element007]
  conduct = 2
  density = 1
  expand = 3
  formula = Fe
  name = G4_Fe
  specific = 4
FEATURE [App::DocumentObjectGroupPython] Co_element001  label="Co_element : 1"  # scripted group (container) (typed FeaturePython)
  n = 1
  ref = Co_element
FEATURE [App::DocumentObjectGroupPython] G4_Co  # scripted group (container) (typed FeaturePython)
  Dunit = g/cm3
  Dvalue = 8.9
  Group = -> [Co_element001]
  conduct = 2
  density = 1
  expand = 3
  formula = Co
  name = G4_Co
  specific = 4
FEATURE [App::DocumentObjectGroupPython] Ni_element001  label="Ni_element : 1"  # scripted group (container) (typed FeaturePython)
  n = 1
  ref = Ni_element
FEATURE [App::DocumentObjectGroupPython] G4_Ni  # scripted group (container) (typed FeaturePython)
  Dunit = g/cm3
  Dvalue = 8.902
  Group = -> [Ni_element001]
  conduct = 2
  density = 1
  expand = 3
  formula = Ni
  name = G4_Ni
  specific = 4
FEATURE [App::DocumentObjectGroupPython] Cu_element001  label="Cu_element : 1"  # scripted group (container) (typed FeaturePython)
  n = 1
  ref = Cu_element
FEATURE [App::DocumentObjectGroupPython] G4_Cu  # scripted group (container) (typed FeaturePython)
  Dunit = g/cm3
  Dvalue = 8.96
  Group = -> [Cu_element001]
  conduct = 2
  density = 1
  expand = 3
  formula = Cu
  name = G4_Cu
  specific = 4
FEATURE [App::DocumentObjectGroupPython] Zn_element001  label="Zn_element : 1"  # scripted group (container) (typed FeaturePython)
  n = 1
  ref = Zn_element
FEATURE [App::DocumentObjectGroupPython] G4_Zn  # scripted group (container) (typed FeaturePython)
  Dunit = g/cm3
  Dvalue = 7.133
  Group = -> [Zn_element001]
  conduct = 2
  density = 1
  expand = 3
  formula = Zn
  name = G4_Zn
  specific = 4
FEATURE [App::DocumentObjectGroupPython] Ga_element002  label="Ga_element : 002"  # scripted group (container) (typed FeaturePython)
  n = 1
  ref = Ga_element
FEATURE [App::DocumentObjectGroupPython] G4_Ga  # scripted group (container) (typed FeaturePython)
  Dunit = g/cm3
  Dvalue = 5.904
  Group = -> [Ga_element002]
  conduct = 2
  density = 1
  expand = 3
  formula = Ga
  name = G4_Ga
  specific = 4
FEATURE [App::DocumentObjectGroupPython] Ge_element002  label="Ge_element : 1"  # scripted group (container) (typed FeaturePython)
  n = 1
  ref = Ge_element
FEATURE [App::DocumentObjectGroupPython] G4_Ge  # scripted group (container) (typed FeaturePython)
  Dunit = g/cm3
  Dvalue = 5.323
  Group = -> [Ge_element002]
  conduct = 2
  density = 1
  expand = 3
  formula = Ge
  name = G4_Ge
  specific = 4
FEATURE [App::DocumentObjectGroupPython] As_element003  label="As_element : 002"  # scripted group (container) (typed FeaturePython)
  n = 1
  ref = As_element
FEATURE [App::DocumentObjectGroupPython] G4_As  # scripted group (container) (typed FeaturePython)
  Dunit = g/cm3
  Dvalue = 5.73
  Group = -> [As_element003]
  conduct = 2
  density = 1
  expand = 3
  formula = As
  name = G4_As
  specific = 4
FEATURE [App::DocumentObjectGroupPython] Se_element001  label="Se_element : 1"  # scripted group (container) (typed FeaturePython)
  n = 1
  ref = Se_element
FEATURE [App::DocumentObjectGroupPython] G4_Se  # scripted group (container) (typed FeaturePython)
  Dunit = g/cm3
  Dvalue = 4.5
  Group = -> [Se_element001]
  conduct = 2
  density = 1
  expand = 3
  formula = Se
  name = G4_Se
  specific = 4
FEATURE [App::DocumentObjectGroupPython] Br_element007  label="Br_element : 004"  # scripted group (container) (typed FeaturePython)
  n = 1
  ref = Br_element
FEATURE [App::DocumentObjectGroupPython] G4_Br  # scripted group (container) (typed FeaturePython)
  Dunit = g/cm3
  Dvalue = 0.0070721
  Group = -> [Br_element007]
  conduct = 2
  density = 1
  expand = 3
  formula = Br
  name = G4_Br
  specific = 4
FEATURE [App::DocumentObjectGroupPython] Kr_element001  label="Kr_element : 1"  # scripted group (container) (typed FeaturePython)
  n = 1
  ref = Kr_element
FEATURE [App::DocumentObjectGroupPython] G4_Kr  # scripted group (container) (typed FeaturePython)
  Dunit = g/cm3
  Dvalue = 0.00347832
  Group = -> [Kr_element001]
  conduct = 2
  density = 1
  expand = 3
  formula = Kr
  name = G4_Kr
  specific = 4
FEATURE [App::DocumentObjectGroupPython] Rb_element001  label="Rb_element : 1"  # scripted group (container) (typed FeaturePython)
  n = 1
  ref = Rb_element
FEATURE [App::DocumentObjectGroupPython] G4_Rb  # scripted group (container) (typed FeaturePython)
  Dunit = g/cm3
  Dvalue = 1.532
  Group = -> [Rb_element001]
  conduct = 2
  density = 1
  expand = 3
  formula = Rb
  name = G4_Rb
  specific = 4
FEATURE [App::DocumentObjectGroupPython] Sr_element001  label="Sr_element : 1"  # scripted group (container) (typed FeaturePython)
  n = 1
  ref = Sr_element
FEATURE [App::DocumentObjectGroupPython] G4_Sr  # scripted group (container) (typed FeaturePython)
  Dunit = g/cm3
  Dvalue = 2.54
  Group = -> [Sr_element001]
  conduct = 2
  density = 1
  expand = 3
  formula = Sr
  name = G4_Sr
  specific = 4
FEATURE [App::DocumentObjectGroupPython] Y_element001  label="Y_element : 1"  # scripted group (container) (typed FeaturePython)
  n = 1
  ref = Y_element
FEATURE [App::DocumentObjectGroupPython] G4_Y  # scripted group (container) (typed FeaturePython)
  Dunit = g/cm3
  Dvalue = 4.469
  Group = -> [Y_element001]
  conduct = 2
  density = 1
  expand = 3
  formula = Y
  name = G4_Y
  specific = 4
FEATURE [App::DocumentObjectGroupPython] Zr_element001  label="Zr_element : 1"  # scripted group (container) (typed FeaturePython)
  n = 1
  ref = Zr_element
FEATURE [App::DocumentObjectGroupPython] G4_Zr  # scripted group (container) (typed FeaturePython)
  Dunit = g/cm3
  Dvalue = 6.506
  Group = -> [Zr_element001]
  conduct = 2
  density = 1
  expand = 3
  formula = Zr
  name = G4_Zr
  specific = 4
FEATURE [App::DocumentObjectGroupPython] Nb_element001  label="Nb_element : 1"  # scripted group (container) (typed FeaturePython)
  n = 1
  ref = Nb_element
FEATURE [App::DocumentObjectGroupPython] G4_Nb  # scripted group (container) (typed FeaturePython)
  Dunit = g/cm3
  Dvalue = 8.57
  Group = -> [Nb_element001]
  conduct = 2
  density = 1
  expand = 3
  formula = Nb
  name = G4_Nb
  specific = 4
FEATURE [App::DocumentObjectGroupPython] Mo_element001  label="Mo_element : 1"  # scripted group (container) (typed FeaturePython)
  n = 1
  ref = Mo_element
FEATURE [App::DocumentObjectGroupPython] G4_Mo  # scripted group (container) (typed FeaturePython)
  Dunit = g/cm3
  Dvalue = 10.22
  Group = -> [Mo_element001]
  conduct = 2
  density = 1
  expand = 3
  formula = Mo
  name = G4_Mo
  specific = 4
FEATURE [App::DocumentObjectGroupPython] Tc_element001  label="Tc_element : 1"  # scripted group (container) (typed FeaturePython)
  n = 1
  ref = Tc_element
FEATURE [App::DocumentObjectGroupPython] G4_Tc  # scripted group (container) (typed FeaturePython)
  Dunit = g/cm3
  Dvalue = 11.5
  Group = -> [Tc_element001]
  conduct = 2
  density = 1
  expand = 3
  formula = Tc
  name = G4_Tc
  specific = 4
FEATURE [App::DocumentObjectGroupPython] Ru_element001  label="Ru_element : 1"  # scripted group (container) (typed FeaturePython)
  n = 1
  ref = Ru_element
FEATURE [App::DocumentObjectGroupPython] G4_Ru  # scripted group (container) (typed FeaturePython)
  Dunit = g/cm3
  Dvalue = 12.41
  Group = -> [Ru_element001]
  conduct = 2
  density = 1
  expand = 3
  formula = Ru
  name = G4_Ru
  specific = 4
FEATURE [App::DocumentObjectGroupPython] Rh_element001  label="Rh_element : 1"  # scripted group (container) (typed FeaturePython)
  n = 1
  ref = Rh_element
FEATURE [App::DocumentObjectGroupPython] G4_Rh  # scripted group (container) (typed FeaturePython)
  Dunit = g/cm3
  Dvalue = 12.41
  Group = -> [Rh_element001]
  conduct = 2
  density = 1
  expand = 3
  formula = Rh
  name = G4_Rh
  specific = 4
FEATURE [App::DocumentObjectGroupPython] Pd_element001  label="Pd_element : 1"  # scripted group (container) (typed FeaturePython)
  n = 1
  ref = Pd_element
FEATURE [App::DocumentObjectGroupPython] G4_Pd  # scripted group (container) (typed FeaturePython)
  Dunit = g/cm3
  Dvalue = 12.02
  Group = -> [Pd_element001]
  conduct = 2
  density = 1
  expand = 3
  formula = Pd
  name = G4_Pd
  specific = 4
FEATURE [App::DocumentObjectGroupPython] Ag_element006  label="Ag_element : 004"  # scripted group (container) (typed FeaturePython)
  n = 1
  ref = Ag_element
FEATURE [App::DocumentObjectGroupPython] G4_Ag  # scripted group (container) (typed FeaturePython)
  Dunit = g/cm3
  Dvalue = 10.5
  Group = -> [Ag_element006]
  conduct = 2
  density = 1
  expand = 3
  formula = Ag
  name = G4_Ag
  specific = 4
FEATURE [App::DocumentObjectGroupPython] Cd_element003  label="Cd_element : 003"  # scripted group (container) (typed FeaturePython)
  n = 1
  ref = Cd_element
FEATURE [App::DocumentObjectGroupPython] G4_Cd  # scripted group (container) (typed FeaturePython)
  Dunit = g/cm3
  Dvalue = 8.65
  Group = -> [Cd_element003]
  conduct = 2
  density = 1
  expand = 3
  formula = Cd
  name = G4_Cd
  specific = 4
FEATURE [App::DocumentObjectGroupPython] In_element001  label="In_element : 1"  # scripted group (container) (typed FeaturePython)
  n = 1
  ref = In_element
FEATURE [App::DocumentObjectGroupPython] G4_In  # scripted group (container) (typed FeaturePython)
  Dunit = g/cm3
  Dvalue = 7.31
  Group = -> [In_element001]
  conduct = 2
  density = 1
  expand = 3
  formula = In
  name = G4_In
  specific = 4
FEATURE [App::DocumentObjectGroupPython] Sn_element001  label="Sn_element : 1"  # scripted group (container) (typed FeaturePython)
  n = 1
  ref = Sn_element
FEATURE [App::DocumentObjectGroupPython] G4_Sn  # scripted group (container) (typed FeaturePython)
  Dunit = g/cm3
  Dvalue = 7.31
  Group = -> [Sn_element001]
  conduct = 2
  density = 1
  expand = 3
  formula = Sn
  name = G4_Sn
  specific = 4
FEATURE [App::DocumentObjectGroupPython] Sb_element001  label="Sb_element : 1"  # scripted group (container) (typed FeaturePython)
  n = 1
  ref = Sb_element
FEATURE [App::DocumentObjectGroupPython] G4_Sb  # scripted group (container) (typed FeaturePython)
  Dunit = g/cm3
  Dvalue = 6.691
  Group = -> [Sb_element001]
  conduct = 2
  density = 1
  expand = 3
  formula = Sb
  name = G4_Sb
  specific = 4
FEATURE [App::DocumentObjectGroupPython] Te_element002  label="Te_element : 002"  # scripted group (container) (typed FeaturePython)
  n = 1
  ref = Te_element
FEATURE [App::DocumentObjectGroupPython] G4_Te  # scripted group (container) (typed FeaturePython)
  Dunit = g/cm3
  Dvalue = 6.24
  Group = -> [Te_element002]
  conduct = 2
  density = 1
  expand = 3
  formula = Te
  name = G4_Te
  specific = 4
FEATURE [App::DocumentObjectGroupPython] I_element010  label="I_element : 006"  # scripted group (container) (typed FeaturePython)
  n = 1
  ref = I_element
FEATURE [App::DocumentObjectGroupPython] G4_I  # scripted group (container) (typed FeaturePython)
  Dunit = g/cm3
  Dvalue = 4.93
  Group = -> [I_element010]
  conduct = 2
  density = 1
  expand = 3
  formula = I
  name = G4_I
  specific = 4
FEATURE [App::DocumentObjectGroupPython] Xe_element001  label="Xe_element : 1"  # scripted group (container) (typed FeaturePython)
  n = 1
  ref = Xe_element
FEATURE [App::DocumentObjectGroupPython] G4_Xe  # scripted group (container) (typed FeaturePython)
  Dunit = g/cm3
  Dvalue = 0.00548536
  Group = -> [Xe_element001]
  conduct = 2
  density = 1
  expand = 3
  formula = Xe
  name = G4_Xe
  specific = 4
FEATURE [App::DocumentObjectGroupPython] Cs_element003  label="Cs_element : 003"  # scripted group (container) (typed FeaturePython)
  n = 1
  ref = Cs_element
FEATURE [App::DocumentObjectGroupPython] G4_Cs  # scripted group (container) (typed FeaturePython)
  Dunit = g/cm3
  Dvalue = 1.873
  Group = -> [Cs_element003]
  conduct = 2
  density = 1
  expand = 3
  formula = Cs
  name = G4_Cs
  specific = 4
FEATURE [App::DocumentObjectGroupPython] Ba_element003  label="Ba_element : 003"  # scripted group (container) (typed FeaturePython)
  n = 1
  ref = Ba_element
FEATURE [App::DocumentObjectGroupPython] G4_Ba  # scripted group (container) (typed FeaturePython)
  Dunit = g/cm3
  Dvalue = 3.5
  Group = -> [Ba_element003]
  conduct = 2
  density = 1
  expand = 3
  formula = Ba
  name = G4_Ba
  specific = 4
FEATURE [App::DocumentObjectGroupPython] La_element003  label="La_element : 003"  # scripted group (container) (typed FeaturePython)
  n = 1
  ref = La_element
FEATURE [App::DocumentObjectGroupPython] G4_La  # scripted group (container) (typed FeaturePython)
  Dunit = g/cm3
  Dvalue = 6.154
  Group = -> [La_element003]
  conduct = 2
  density = 1
  expand = 3
  formula = La
  name = G4_La
  specific = 4
FEATURE [App::DocumentObjectGroupPython] Ce_element002  label="Ce_element : 1"  # scripted group (container) (typed FeaturePython)
  n = 1
  ref = Ce_element
FEATURE [App::DocumentObjectGroupPython] G4_Ce  # scripted group (container) (typed FeaturePython)
  Dunit = g/cm3
  Dvalue = 6.657
  Group = -> [Ce_element002]
  conduct = 2
  density = 1
  expand = 3
  formula = Ce
  name = G4_Ce
  specific = 4
FEATURE [App::DocumentObjectGroupPython] Pr_element001  label="Pr_element : 1"  # scripted group (container) (typed FeaturePython)
  n = 1
  ref = Pr_element
FEATURE [App::DocumentObjectGroupPython] G4_Pr  # scripted group (container) (typed FeaturePython)
  Dunit = g/cm3
  Dvalue = 6.71
  Group = -> [Pr_element001]
  conduct = 2
  density = 1
  expand = 3
  formula = Pr
  name = G4_Pr
  specific = 4
FEATURE [App::DocumentObjectGroupPython] Nd_element001  label="Nd_element : 1"  # scripted group (container) (typed FeaturePython)
  n = 1
  ref = Nd_element
FEATURE [App::DocumentObjectGroupPython] G4_Nd  # scripted group (container) (typed FeaturePython)
  Dunit = g/cm3
  Dvalue = 6.9
  Group = -> [Nd_element001]
  conduct = 2
  density = 1
  expand = 3
  formula = Nd
  name = G4_Nd
  specific = 4
FEATURE [App::DocumentObjectGroupPython] Pm_element001  label="Pm_element : 1"  # scripted group (container) (typed FeaturePython)
  n = 1
  ref = Pm_element
FEATURE [App::DocumentObjectGroupPython] G4_Pm  # scripted group (container) (typed FeaturePython)
  Dunit = g/cm3
  Dvalue = 7.22
  Group = -> [Pm_element001]
  conduct = 2
  density = 1
  expand = 3
  formula = Pm
  name = G4_Pm
  specific = 4
FEATURE [App::DocumentObjectGroupPython] Sm_element001  label="Sm_element : 1"  # scripted group (container) (typed FeaturePython)
  n = 1
  ref = Sm_element
FEATURE [App::DocumentObjectGroupPython] G4_Sm  # scripted group (container) (typed FeaturePython)
  Dunit = g/cm3
  Dvalue = 7.46
  Group = -> [Sm_element001]
  conduct = 2
  density = 1
  expand = 3
  formula = Sm
  name = G4_Sm
  specific = 4
FEATURE [App::DocumentObjectGroupPython] Eu_element001  label="Eu_element : 1"  # scripted group (container) (typed FeaturePython)
  n = 1
  ref = Eu_element
FEATURE [App::DocumentObjectGroupPython] G4_Eu  # scripted group (container) (typed FeaturePython)
  Dunit = g/cm3
  Dvalue = 5.243
  Group = -> [Eu_element001]
  conduct = 2
  density = 1
  expand = 3
  formula = Eu
  name = G4_Eu
  specific = 4
FEATURE [App::DocumentObjectGroupPython] Gd_element002  label="Gd_element : 1"  # scripted group (container) (typed FeaturePython)
  n = 1
  ref = Gd_element
FEATURE [App::DocumentObjectGroupPython] G4_Gd  # scripted group (container) (typed FeaturePython)
  Dunit = g/cm3
  Dvalue = 7.9004
  Group = -> [Gd_element002]
  conduct = 2
  density = 1
  expand = 3
  formula = Gd
  name = G4_Gd
  specific = 4
FEATURE [App::DocumentObjectGroupPython] Tb_element001  label="Tb_element : 1"  # scripted group (container) (typed FeaturePython)
  n = 1
  ref = Tb_element
FEATURE [App::DocumentObjectGroupPython] G4_Tb  # scripted group (container) (typed FeaturePython)
  Dunit = g/cm3
  Dvalue = 8.229
  Group = -> [Tb_element001]
  conduct = 2
  density = 1
  expand = 3
  formula = Tb
  name = G4_Tb
  specific = 4
FEATURE [App::DocumentObjectGroupPython] Dy_element001  label="Dy_element : 1"  # scripted group (container) (typed FeaturePython)
  n = 1
  ref = Dy_element
FEATURE [App::DocumentObjectGroupPython] G4_Dy  # scripted group (container) (typed FeaturePython)
  Dunit = g/cm3
  Dvalue = 8.55
  Group = -> [Dy_element001]
  conduct = 2
  density = 1
  expand = 3
  formula = Dy
  name = G4_Dy
  specific = 4
FEATURE [App::DocumentObjectGroupPython] Ho_element001  label="Ho_element : 1"  # scripted group (container) (typed FeaturePython)
  n = 1
  ref = Ho_element
FEATURE [App::DocumentObjectGroupPython] G4_Ho  # scripted group (container) (typed FeaturePython)
  Dunit = g/cm3
  Dvalue = 8.795
  Group = -> [Ho_element001]
  conduct = 2
  density = 1
  expand = 3
  formula = Ho
  name = G4_Ho
  specific = 4
FEATURE [App::DocumentObjectGroupPython] Er_element001  label="Er_element : 1"  # scripted group (container) (typed FeaturePython)
  n = 1
  ref = Er_element
FEATURE [App::DocumentObjectGroupPython] G4_Er  # scripted group (container) (typed FeaturePython)
  Dunit = g/cm3
  Dvalue = 9.066
  Group = -> [Er_element001]
  conduct = 2
  density = 1
  expand = 3
  formula = Er
  name = G4_Er
  specific = 4
FEATURE [App::DocumentObjectGroupPython] Tm_element001  label="Tm_element : 1"  # scripted group (container) (typed FeaturePython)
  n = 1
  ref = Tm_element
FEATURE [App::DocumentObjectGroupPython] G4_Tm  # scripted group (container) (typed FeaturePython)
  Dunit = g/cm3
  Dvalue = 9.321
  Group = -> [Tm_element001]
  conduct = 2
  density = 1
  expand = 3
  formula = Tm
  name = G4_Tm
  specific = 4
FEATURE [App::DocumentObjectGroupPython] Yb_element001  label="Yb_element : 1"  # scripted group (container) (typed FeaturePython)
  n = 1
  ref = Yb_element
FEATURE [App::DocumentObjectGroupPython] G4_Yb  # scripted group (container) (typed FeaturePython)
  Dunit = g/cm3
  Dvalue = 6.73
  Group = -> [Yb_element001]
  conduct = 2
  density = 1
  expand = 3
  formula = Yb
  name = G4_Yb
  specific = 4
FEATURE [App::DocumentObjectGroupPython] Lu_element001  label="Lu_element : 1"  # scripted group (container) (typed FeaturePython)
  n = 1
  ref = Lu_element
FEATURE [App::DocumentObjectGroupPython] G4_Lu  # scripted group (container) (typed FeaturePython)
  Dunit = g/cm3
  Dvalue = 9.84
  Group = -> [Lu_element001]
  conduct = 2
  density = 1
  expand = 3
  formula = Lu
  name = G4_Lu
  specific = 4
FEATURE [App::DocumentObjectGroupPython] Hf_element001  label="Hf_element : 1"  # scripted group (container) (typed FeaturePython)
  n = 1
  ref = Hf_element
FEATURE [App::DocumentObjectGroupPython] G4_Hf  # scripted group (container) (typed FeaturePython)
  Dunit = g/cm3
  Dvalue = 13.31
  Group = -> [Hf_element001]
  conduct = 2
  density = 1
  expand = 3
  formula = Hf
  name = G4_Hf
  specific = 4
FEATURE [App::DocumentObjectGroupPython] Ta_element001  label="Ta_element : 1"  # scripted group (container) (typed FeaturePython)
  n = 1
  ref = Ta_element
FEATURE [App::DocumentObjectGroupPython] G4_Ta  # scripted group (container) (typed FeaturePython)
  Dunit = g/cm3
  Dvalue = 16.654
  Group = -> [Ta_element001]
  conduct = 2
  density = 1
  expand = 3
  formula = Ta
  name = G4_Ta
  specific = 4
FEATURE [App::DocumentObjectGroupPython] W_element004  label="W_element : 004"  # scripted group (container) (typed FeaturePython)
  n = 1
  ref = W_element
FEATURE [App::DocumentObjectGroupPython] G4_W  # scripted group (container) (typed FeaturePython)
  Dunit = g/cm3
  Dvalue = 19.3
  Group = -> [W_element004]
  conduct = 2
  density = 1
  expand = 3
  formula = W
  name = G4_W
  specific = 4
FEATURE [App::DocumentObjectGroupPython] Re_element001  label="Re_element : 1"  # scripted group (container) (typed FeaturePython)
  n = 1
  ref = Re_element
FEATURE [App::DocumentObjectGroupPython] G4_Re  # scripted group (container) (typed FeaturePython)
  Dunit = g/cm3
  Dvalue = 21.02
  Group = -> [Re_element001]
  conduct = 2
  density = 1
  expand = 3
  formula = Re
  name = G4_Re
  specific = 4
FEATURE [App::DocumentObjectGroupPython] Os_element001  label="Os_element : 1"  # scripted group (container) (typed FeaturePython)
  n = 1
  ref = Os_element
FEATURE [App::DocumentObjectGroupPython] G4_Os  # scripted group (container) (typed FeaturePython)
  Dunit = g/cm3
  Dvalue = 22.57
  Group = -> [Os_element001]
  conduct = 2
  density = 1
  expand = 3
  formula = Os
  name = G4_Os
  specific = 4
FEATURE [App::DocumentObjectGroupPython] Ir_element001  label="Ir_element : 1"  # scripted group (container) (typed FeaturePython)
  n = 1
  ref = Ir_element
FEATURE [App::DocumentObjectGroupPython] G4_Ir  # scripted group (container) (typed FeaturePython)
  Dunit = g/cm3
  Dvalue = 22.42
  Group = -> [Ir_element001]
  conduct = 2
  density = 1
  expand = 3
  formula = Ir
  name = G4_Ir
  specific = 4
FEATURE [App::DocumentObjectGroupPython] Pt_element001  label="Pt_element : 1"  # scripted group (container) (typed FeaturePython)
  n = 1
  ref = Pt_element
FEATURE [App::DocumentObjectGroupPython] G4_Pt  # scripted group (container) (typed FeaturePython)
  Dunit = g/cm3
  Dvalue = 21.45
  Group = -> [Pt_element001]
  conduct = 2
  density = 1
  expand = 3
  formula = Pt
  name = G4_Pt
  specific = 4
FEATURE [App::DocumentObjectGroupPython] Au_element001  label="Au_element : 1"  # scripted group (container) (typed FeaturePython)
  n = 1
  ref = Au_element
FEATURE [App::DocumentObjectGroupPython] G4_Au  # scripted group (container) (typed FeaturePython)
  Dunit = g/cm3
  Dvalue = 19.32
  Group = -> [Au_element001]
  conduct = 2
  density = 1
  expand = 3
  formula = Au
  name = G4_Au
  specific = 4
FEATURE [App::DocumentObjectGroupPython] Hg_element002  label="Hg_element : 002"  # scripted group (container) (typed FeaturePython)
  n = 1
  ref = Hg_element
FEATURE [App::DocumentObjectGroupPython] G4_Hg  # scripted group (container) (typed FeaturePython)
  Dunit = g/cm3
  Dvalue = 13.546
  Group = -> [Hg_element002]
  conduct = 2
  density = 1
  expand = 3
  formula = Hg
  name = G4_Hg
  specific = 4
FEATURE [App::DocumentObjectGroupPython] Tl_element002  label="Tl_element : 002"  # scripted group (container) (typed FeaturePython)
  n = 1
  ref = Tl_element
FEATURE [App::DocumentObjectGroupPython] G4_Tl  # scripted group (container) (typed FeaturePython)
  Dunit = g/cm3
  Dvalue = 11.72
  Group = -> [Tl_element002]
  conduct = 2
  density = 1
  expand = 3
  formula = Tl
  name = G4_Tl
  specific = 4
FEATURE [App::DocumentObjectGroupPython] Pb_element003  label="Pb_element : 1"  # scripted group (container) (typed FeaturePython)
  n = 1
  ref = Pb_element
FEATURE [App::DocumentObjectGroupPython] G4_Pb  # scripted group (container) (typed FeaturePython)
  Dunit = g/cm3
  Dvalue = 11.35
  Group = -> [Pb_element003]
  conduct = 2
  density = 1
  expand = 3
  formula = Pb
  name = G4_Pb
  specific = 4
FEATURE [App::DocumentObjectGroupPython] Bi_element002  label="Bi_element : 1"  # scripted group (container) (typed FeaturePython)
  n = 1
  ref = Bi_element
FEATURE [App::DocumentObjectGroupPython] G4_Bi  # scripted group (container) (typed FeaturePython)
  Dunit = g/cm3
  Dvalue = 9.747
  Group = -> [Bi_element002]
  conduct = 2
  density = 1
  expand = 3
  formula = Bi
  name = G4_Bi
  specific = 4
FEATURE [App::DocumentObjectGroupPython] Po_element001  label="Po_element : 1"  # scripted group (container) (typed FeaturePython)
  n = 1
  ref = Po_element
FEATURE [App::DocumentObjectGroupPython] G4_Po  # scripted group (container) (typed FeaturePython)
  Dunit = g/cm3
  Dvalue = 9.32
  Group = -> [Po_element001]
  conduct = 2
  density = 1
  expand = 3
  formula = Po
  name = G4_Po
  specific = 4
FEATURE [App::DocumentObjectGroupPython] At_element001  label="At_element : 1"  # scripted group (container) (typed FeaturePython)
  n = 1
  ref = At_element
FEATURE [App::DocumentObjectGroupPython] G4_At  # scripted group (container) (typed FeaturePython)
  Dunit = g/cm3
  Dvalue = 9.32
  Group = -> [At_element001]
  conduct = 2
  density = 1
  expand = 3
  formula = At
  name = G4_At
  specific = 4
FEATURE [App::DocumentObjectGroupPython] Rn_element001  label="Rn_element : 1"  # scripted group (container) (typed FeaturePython)
  n = 1
  ref = Rn_element
FEATURE [App::DocumentObjectGroupPython] G4_Rn  # scripted group (container) (typed FeaturePython)
  Dunit = g/cm3
  Dvalue = 0.00900662
  Group = -> [Rn_element001]
  conduct = 2
  density = 1
  expand = 3
  formula = Rn
  name = G4_Rn
  specific = 4
FEATURE [App::DocumentObjectGroupPython] Fr_element001  label="Fr_element : 1"  # scripted group (container) (typed FeaturePython)
  n = 1
  ref = Fr_element
FEATURE [App::DocumentObjectGroupPython] G4_Fr  # scripted group (container) (typed FeaturePython)
  Dunit = g/cm3
  Dvalue = 1
  Group = -> [Fr_element001]
  conduct = 2
  density = 1
  expand = 3
  formula = Fr
  name = G4_Fr
  specific = 4
FEATURE [App::DocumentObjectGroupPython] Ra_element001  label="Ra_element : 1"  # scripted group (container) (typed FeaturePython)
  n = 1
  ref = Ra_element
FEATURE [App::DocumentObjectGroupPython] G4_Ra  # scripted group (container) (typed FeaturePython)
  Dunit = g/cm3
  Dvalue = 5
  Group = -> [Ra_element001]
  conduct = 2
  density = 1
  expand = 3
  formula = Ra
  name = G4_Ra
  specific = 4
FEATURE [App::DocumentObjectGroupPython] Ac_element001  label="Ac_element : 1"  # scripted group (container) (typed FeaturePython)
  n = 1
  ref = Ac_element
FEATURE [App::DocumentObjectGroupPython] G4_Ac  # scripted group (container) (typed FeaturePython)
  Dunit = g/cm3
  Dvalue = 10.07
  Group = -> [Ac_element001]
  conduct = 2
  density = 1
  expand = 3
  formula = Ac
  name = G4_Ac
  specific = 4
FEATURE [App::DocumentObjectGroupPython] Th_element001  label="Th_element : 1"  # scripted group (container) (typed FeaturePython)
  n = 1
  ref = Th_element
FEATURE [App::DocumentObjectGroupPython] G4_Th  # scripted group (container) (typed FeaturePython)
  Dunit = g/cm3
  Dvalue = 11.72
  Group = -> [Th_element001]
  conduct = 2
  density = 1
  expand = 3
  formula = Th
  name = G4_Th
  specific = 4
FEATURE [App::DocumentObjectGroupPython] Pa_element001  label="Pa_element : 1"  # scripted group (container) (typed FeaturePython)
  n = 1
  ref = Pa_element
FEATURE [App::DocumentObjectGroupPython] G4_Pa  # scripted group (container) (typed FeaturePython)
  Dunit = g/cm3
  Dvalue = 15.37
  Group = -> [Pa_element001]
  conduct = 2
  density = 1
  expand = 3
  formula = Pa
  name = G4_Pa
  specific = 4
FEATURE [App::DocumentObjectGroupPython] U_element004  label="U_element : 004"  # scripted group (container) (typed FeaturePython)
  n = 1
  ref = U_element
FEATURE [App::DocumentObjectGroupPython] G4_U  # scripted group (container) (typed FeaturePython)
  Dunit = g/cm3
  Dvalue = 18.95
  Group = -> [U_element004]
  conduct = 2
  density = 1
  expand = 3
  formula = U
  name = G4_U
  specific = 4
FEATURE [App::DocumentObjectGroupPython] Np_element001  label="Np_element : 1"  # scripted group (container) (typed FeaturePython)
  n = 1
  ref = Np_element
FEATURE [App::DocumentObjectGroupPython] G4_Np  # scripted group (container) (typed FeaturePython)
  Dunit = g/cm3
  Dvalue = 20.25
  Group = -> [Np_element001]
  conduct = 2
  density = 1
  expand = 3
  formula = Np
  name = G4_Np
  specific = 4
FEATURE [App::DocumentObjectGroupPython] Pu_element002  label="Pu_element : 002"  # scripted group (container) (typed FeaturePython)
  n = 1
  ref = Pu_element
FEATURE [App::DocumentObjectGroupPython] G4_Pu  # scripted group (container) (typed FeaturePython)
  Dunit = g/cm3
  Dvalue = 19.84
  Group = -> [Pu_element002]
  conduct = 2
  density = 1
  expand = 3
  formula = Pu
  name = G4_Pu
  specific = 4
FEATURE [App::DocumentObjectGroupPython] Am_element001  label="Am_element : 1"  # scripted group (container) (typed FeaturePython)
  n = 1
  ref = Am_element
FEATURE [App::DocumentObjectGroupPython] G4_Am  # scripted group (container) (typed FeaturePython)
  Dunit = g/cm3
  Dvalue = 13.67
  Group = -> [Am_element001]
  conduct = 2
  density = 1
  expand = 3
  formula = Am
  name = G4_Am
  specific = 4
FEATURE [App::DocumentObjectGroupPython] Cm_element001  label="Cm_element : 1"  # scripted group (container) (typed FeaturePython)
  n = 1
  ref = Cm_element
FEATURE [App::DocumentObjectGroupPython] G4_Cm  # scripted group (container) (typed FeaturePython)
  Dunit = g/cm3
  Dvalue = 13.51
  Group = -> [Cm_element001]
  conduct = 2
  density = 1
  expand = 3
  formula = Cm
  name = G4_Cm
  specific = 4
FEATURE [App::DocumentObjectGroupPython] Bk_element001  label="Bk_element : 1"  # scripted group (container) (typed FeaturePython)
  n = 1
  ref = Bk_element
FEATURE [App::DocumentObjectGroupPython] G4_Bk  # scripted group (container) (typed FeaturePython)
  Dunit = g/cm3
  Dvalue = 14
  Group = -> [Bk_element001]
  conduct = 2
  density = 1
  expand = 3
  formula = Bk
  name = G4_Bk
  specific = 4
FEATURE [App::DocumentObjectGroupPython] Cf_element001  label="Cf_element : 1"  # scripted group (container) (typed FeaturePython)
  n = 1
  ref = Cf_element
FEATURE [App::DocumentObjectGroupPython] G4_Cf  # scripted group (container) (typed FeaturePython)
  Dunit = g/cm3
  Dvalue = 10
  Group = -> [Cf_element001]
  conduct = 2
  density = 1
  expand = 3
  formula = Cf
  name = G4_Cf
  specific = 4
FEATURE [App::DocumentObjectGroupPython] Element  # scripted group (container) (typed FeaturePython)
  Group = -> [G4_H,G4_He,G4_Li,G4_Be,G4_B,G4_C,G4_N,G4_O,G4_F,G4_Ne,G4_Na,G4_Mg,G4_Al,G4_Si,G4_P,G4_S,G4_Cl,G4_Ar,G4_K,G4_Ca,G4_Sc,G4_Ti,G4_V,G4_Cr,G4_Mn,G4_Fe,G4_Co,G4_Ni,G4_Cu,G4_Zn,G4_Ga,G4_Ge,G4_As,G4_Se,G4_Br,G4_Kr,G4_Rb,G4_Sr,G4_Y,G4_Zr,G4_Nb,G4_Mo,G4_Tc,G4_Ru,G4_Rh,G4_Pd,G4_Ag,G4_Cd,G4_In,G4_Sn,G4_Sb,G4_Te,G4_I,G4_Xe,G4_Cs,G4_Ba,G4_La,G4_Ce,G4_Pr,G4_Nd,G4_Pm,G4_Sm,G4_Eu,G4_Gd,G4_Tb,G4_Dy,G4_Ho,G4_Er,+30 more]
FEATURE [App::DocumentObjectGroupPython] H_element114  label="H_element : 063"  # scripted group (container) (typed FeaturePython)
  n = 2
  ref = H_element
FEATURE [App::DocumentObjectGroupPython] G4_lH2  # scripted group (container) (typed FeaturePython)
  Dunit = g/cm3
  Dvalue = 0.0708
  Group = -> [H_element114]
  conduct = 2
  density = 1
  expand = 3
  formula = G4_lH2
  name = G4_lH2
  specific = 4
FEATURE [App::DocumentObjectGroupPython] N_element049  label="N_element : 022"  # scripted group (container) (typed FeaturePython)
  n = 2
  ref = N_element
FEATURE [App::DocumentObjectGroupPython] G4_lN2  # scripted group (container) (typed FeaturePython)
  Dunit = g/cm3
  Dvalue = 0.807
  Group = -> [N_element049]
  conduct = 2
  density = 1
  expand = 3
  formula = G4_lN2
  name = G4_lN2
  specific = 4
FEATURE [App::DocumentObjectGroupPython] O_element106  label="O_element : 060"  # scripted group (container) (typed FeaturePython)
  n = 2
  ref = O_element
FEATURE [App::DocumentObjectGroupPython] G4_lO2  # scripted group (container) (typed FeaturePython)
  Dunit = g/cm3
  Dvalue = 1.141
  Group = -> [O_element106]
  conduct = 2
  density = 1
  expand = 3
  formula = G4_lO2
  name = G4_lO2
  specific = 4
FEATURE [App::DocumentObjectGroupPython] Ar_element003  label="Ar_element : 002"  # scripted group (container) (typed FeaturePython)
  n = 1
  ref = Ar_element
FEATURE [App::DocumentObjectGroupPython] G4_lAr  # scripted group (container) (typed FeaturePython)
  Dunit = g/cm3
  Dvalue = 1.396
  Group = -> [Ar_element003]
  conduct = 2
  density = 1
  expand = 3
  formula = G4_lAr
  name = G4_lAr
  specific = 4
FEATURE [App::DocumentObjectGroupPython] Br_element008  label="Br_element : 005"  # scripted group (container) (typed FeaturePython)
  n = 1
  ref = Br_element
FEATURE [App::DocumentObjectGroupPython] G4_lBr  # scripted group (container) (typed FeaturePython)
  Dunit = g/cm3
  Dvalue = 3.1028
  Group = -> [Br_element008]
  conduct = 2
  density = 1
  expand = 3
  formula = G4_lBr
  name = G4_lBr
  specific = 4
FEATURE [App::DocumentObjectGroupPython] Kr_element002  label="Kr_element : 002"  # scripted group (container) (typed FeaturePython)
  n = 1
  ref = Kr_element
FEATURE [App::DocumentObjectGroupPython] G4_lKr  # scripted group (container) (typed FeaturePython)
  Dunit = g/cm3
  Dvalue = 2.418
  Group = -> [Kr_element002]
  conduct = 2
  density = 1
  expand = 3
  formula = G4_lKr
  name = G4_lKr
  specific = 4
FEATURE [App::DocumentObjectGroupPython] Xe_element002  label="Xe_element : 002"  # scripted group (container) (typed FeaturePython)
  n = 1
  ref = Xe_element
FEATURE [App::DocumentObjectGroupPython] G4_lXe  # scripted group (container) (typed FeaturePython)
  Dunit = g/cm3
  Dvalue = 2.953
  Group = -> [Xe_element002]
  conduct = 2
  density = 1
  expand = 3
  formula = G4_lXe
  name = G4_lXe
  specific = 4
FEATURE [App::DocumentObjectGroupPython] O_element107  label="O_element : 061"  # scripted group (container) (typed FeaturePython)
  n = 4
  ref = O_element
FEATURE [App::DocumentObjectGroupPython] Pb_element004  label="Pb_element : 002"  # scripted group (container) (typed FeaturePython)
  n = 1
  ref = Pb_element
FEATURE [App::DocumentObjectGroupPython] W_element005  label="W_element : 005"  # scripted group (container) (typed FeaturePython)
  n = 1
  ref = W_element
FEATURE [App::DocumentObjectGroupPython] G4_PbWO4  # scripted group (container) (typed FeaturePython)
  Dunit = g/cm3
  Dvalue = 8.28
  Group = -> [O_element107,Pb_element004,W_element005]
  conduct = 2
  density = 1
  expand = 3
  formula = G4_PbWO4
  name = G4_PbWO4
  specific = 4
FEATURE [App::DocumentObjectGroupPython] H_element115  label="H_element : 064"  # scripted group (container) (typed FeaturePython)
  n = 1
  ref = H_element
FEATURE [App::DocumentObjectGroupPython] G4_Galactic  # scripted group (container) (typed FeaturePython)
  Dunit = g/cm3
  Dvalue = 0
  Group = -> [H_element115]
  conduct = 2
  density = 1
  expand = 3
  formula = G4_Galactic
  name = G4_Galactic
  specific = 4
FEATURE [App::DocumentObjectGroupPython] C_element125  label="C_element : 071"  # scripted group (container) (typed FeaturePython)
  n = 1
  ref = C_element
FEATURE [App::DocumentObjectGroupPython] G4_GRAPHITE_POROUS  # scripted group (container) (typed FeaturePython)
  Dunit = g/cm3
  Dvalue = 1.7
  Group = -> [C_element125]
  conduct = 2
  density = 1
  expand = 3
  formula = G4_GRAPHITE_POROUS
  name = G4_GRAPHITE_POROUS
  specific = 4
FEATURE [App::DocumentObjectGroupPython] H_element116  label="H_element : 0.150"  # scripted group (container) (typed FeaturePython)
  n = 0.080538
FEATURE [App::DocumentObjectGroupPython] C_element126  label="C_element : 0.600"  # scripted group (container) (typed FeaturePython)
  n = 0.599848
FEATURE [App::DocumentObjectGroupPython] O_element108  label="O_element : 0.320"  # scripted group (container) (typed FeaturePython)
  n = 0.319614
FEATURE [App::DocumentObjectGroupPython] G4_LUCITE  # scripted group (container) (typed FeaturePython)
  Dunit = g/cm3
  Dvalue = 1.19
  Group = -> [H_element116,C_element126,O_element108]
  conduct = 2
  density = 1
  expand = 3
  formula = G4_LUCITE
  name = G4_LUCITE
  specific = 4
FEATURE [App::DocumentObjectGroupPython] Cu_element002  label="Cu_element : 62"  # scripted group (container) (typed FeaturePython)
  n = 62
  ref = Cu_element
FEATURE [App::DocumentObjectGroupPython] Zn_element002  label="Zn_element : 35"  # scripted group (container) (typed FeaturePython)
  n = 35
  ref = Zn_element
FEATURE [App::DocumentObjectGroupPython] Pb_element005  label="Pb_element : 3"  # scripted group (container) (typed FeaturePython)
  n = 3
  ref = Pb_element
FEATURE [App::DocumentObjectGroupPython] G4_BRASS  # scripted group (container) (typed FeaturePython)
  Dunit = g/cm3
  Dvalue = 8.52
  Group = -> [Cu_element002,Zn_element002,Pb_element005]
  conduct = 2
  density = 1
  expand = 3
  formula = G4_BRASS
  name = G4_BRASS
  specific = 4
FEATURE [App::DocumentObjectGroupPython] Cu_element003  label="Cu_element : 89"  # scripted group (container) (typed FeaturePython)
  n = 89
  ref = Cu_element
FEATURE [App::DocumentObjectGroupPython] Zn_element003  label="Zn_element : 9"  # scripted group (container) (typed FeaturePython)
  n = 9
  ref = Zn_element
FEATURE [App::DocumentObjectGroupPython] Pb_element006  label="Pb_element : 2"  # scripted group (container) (typed FeaturePython)
  n = 2
  ref = Pb_element
FEATURE [App::DocumentObjectGroupPython] G4_BRONZE  # scripted group (container) (typed FeaturePython)
  Dunit = g/cm3
  Dvalue = 8.82
  Group = -> [Cu_element003,Zn_element003,Pb_element006]
  conduct = 2
  density = 1
  expand = 3
  formula = G4_BRONZE
  name = G4_BRONZE
  specific = 4
FEATURE [App::DocumentObjectGroupPython] Fe_element008  label="Fe_element : 74"  # scripted group (container) (typed FeaturePython)
  n = 74
  ref = Fe_element
FEATURE [App::DocumentObjectGroupPython] Cr_element002  label="Cr_element : 18"  # scripted group (container) (typed FeaturePython)
  n = 18
  ref = Cr_element
FEATURE [App::DocumentObjectGroupPython] Ni_element002  label="Ni_element : 8"  # scripted group (container) (typed FeaturePython)
  n = 8
  ref = Ni_element
FEATURE [App::DocumentObjectGroupPython] G4_STAINLESS_STEEL  label="G4_STAINLESS-STEEL"  # scripted group (container) (typed FeaturePython)
  Dunit = g/cm3
  Dvalue = 8
  Group = -> [Fe_element008,Cr_element002,Ni_element002]
  conduct = 2
  density = 1
  expand = 3
  formula = G4_STAINLESS-STEEL
  name = G4_STAINLESS-STEEL
  specific = 4
FEATURE [App::DocumentObjectGroupPython] H_element117  label="H_element : 065"  # scripted group (container) (typed FeaturePython)
  n = 18
  ref = H_element
FEATURE [App::DocumentObjectGroupPython] C_element127  label="C_element : 072"  # scripted group (container) (typed FeaturePython)
  n = 12
  ref = C_element
FEATURE [App::DocumentObjectGroupPython] O_element109  label="O_element : 062"  # scripted group (container) (typed FeaturePython)
  n = 7
  ref = O_element
FEATURE [App::DocumentObjectGroupPython] G4_CR39  # scripted group (container) (typed FeaturePython)
  Dunit = g/cm3
  Dvalue = 1.32
  Group = -> [H_element117,C_element127,O_element109]
  conduct = 2
  density = 1
  expand = 3
  formula = G4_CR39
  name = G4_CR39
  specific = 4
FEATURE [App::DocumentObjectGroupPython] H_element118  label="H_element : 38"  # scripted group (container) (typed FeaturePython)
  n = 38
  ref = H_element
FEATURE [App::DocumentObjectGroupPython] C_element128  label="C_element : 073"  # scripted group (container) (typed FeaturePython)
  n = 18
  ref = C_element
FEATURE [App::DocumentObjectGroupPython] O_element110  label="O_element : 063"  # scripted group (container) (typed FeaturePython)
  n = 1
  ref = O_element
FEATURE [App::DocumentObjectGroupPython] G4_OCTADECANOL  # scripted group (container) (typed FeaturePython)
  Dunit = g/cm3
  Dvalue = 0.812
  Group = -> [H_element118,C_element128,O_element110]
  conduct = 2
  density = 1
  expand = 3
  formula = G4_OCTADECANOL
  name = G4_OCTADECANOL
  specific = 4
FEATURE [App::DocumentObjectGroupPython] HEP  # scripted group (container) (typed FeaturePython)
  Group = -> [G4_lH2,G4_lN2,G4_lO2,G4_lAr,G4_lBr,G4_lKr,G4_lXe,G4_PbWO4,G4_Galactic,G4_GRAPHITE_POROUS,G4_LUCITE,G4_BRASS,G4_BRONZE,G4_STAINLESS_STEEL,G4_CR39,G4_OCTADECANOL]
FEATURE [App::DocumentObjectGroupPython] C_element129  label="C_element : 074"  # scripted group (container) (typed FeaturePython)
  n = 14
  ref = C_element
FEATURE [App::DocumentObjectGroupPython] H_element119  label="H_element : 066"  # scripted group (container) (typed FeaturePython)
  n = 10
  ref = H_element
FEATURE [App::DocumentObjectGroupPython] O_element111  label="O_element : 064"  # scripted group (container) (typed FeaturePython)
  n = 2
  ref = O_element
FEATURE [App::DocumentObjectGroupPython] N_element050  label="N_element : 023"  # scripted group (container) (typed FeaturePython)
  n = 2
  ref = N_element
FEATURE [App::DocumentObjectGroupPython] G4_KEVLAR  # scripted group (container) (typed FeaturePython)
  Dunit = g/cm3
  Dvalue = 1.44
  Group = -> [C_element129,H_element119,O_element111,N_element050]
  conduct = 2
  density = 1
  expand = 3
  formula = G4_KEVLAR
  name = G4_KEVLAR
  specific = 4
FEATURE [App::DocumentObjectGroupPython] C_element130  label="C_element : 075"  # scripted group (container) (typed FeaturePython)
  n = 10
  ref = C_element
FEATURE [App::DocumentObjectGroupPython] H_element120  label="H_element : 067"  # scripted group (container) (typed FeaturePython)
  n = 8
  ref = H_element
FEATURE [App::DocumentObjectGroupPython] O_element112  label="O_element : 065"  # scripted group (container) (typed FeaturePython)
  n = 4
  ref = O_element
FEATURE [App::DocumentObjectGroupPython] G4_DACRON  # scripted group (container) (typed FeaturePython)
  Dunit = g/cm3
  Dvalue = 1.4
  Group = -> [C_element130,H_element120,O_element112]
  conduct = 2
  density = 1
  expand = 3
  formula = G4_DACRON
  name = G4_DACRON
  specific = 4
FEATURE [App::DocumentObjectGroupPython] C_element131  label="C_element : 076"  # scripted group (container) (typed FeaturePython)
  n = 4
  ref = C_element
FEATURE [App::DocumentObjectGroupPython] H_element121  label="H_element : 068"  # scripted group (container) (typed FeaturePython)
  n = 5
  ref = H_element
FEATURE [App::DocumentObjectGroupPython] Cl_element030  label="Cl_element : 016"  # scripted group (container) (typed FeaturePython)
  n = 1
  ref = Cl_element
FEATURE [App::DocumentObjectGroupPython] G4_NEOPRENE  # scripted group (container) (typed FeaturePython)
  Dunit = g/cm3
  Dvalue = 1.23
  Group = -> [C_element131,H_element121,Cl_element030]
  conduct = 2
  density = 1
  expand = 3
  formula = G4_NEOPRENE
  name = G4_NEOPRENE
  specific = 4
FEATURE [App::DocumentObjectGroupPython] Space  # scripted group (container) (typed FeaturePython)
  Group = -> [G4_KEVLAR,G4_DACRON,G4_NEOPRENE]
FEATURE [App::DocumentObjectGroupPython] H_element122  label="H_element : 069"  # scripted group (container) (typed FeaturePython)
  n = 5
  ref = H_element
FEATURE [App::DocumentObjectGroupPython] C_element132  label="C_element : 077"  # scripted group (container) (typed FeaturePython)
  n = 4
  ref = C_element
FEATURE [App::DocumentObjectGroupPython] N_element051  label="N_element : 3"  # scripted group (container) (typed FeaturePython)
  n = 3
  ref = N_element
FEATURE [App::DocumentObjectGroupPython] O_element113  label="O_element : 066"  # scripted group (container) (typed FeaturePython)
  n = 1
  ref = O_element
FEATURE [App::DocumentObjectGroupPython] G4_CYTOSINE  # scripted group (container) (typed FeaturePython)
  Dunit = g/cm3
  Dvalue = 1.55
  Group = -> [H_element122,C_element132,N_element051,O_element113]
  conduct = 2
  density = 1
  expand = 3
  formula = G4_CYTOSINE
  name = G4_CYTOSINE
  specific = 4
FEATURE [App::DocumentObjectGroupPython] H_element123  label="H_element : 070"  # scripted group (container) (typed FeaturePython)
  n = 6
  ref = H_element
FEATURE [App::DocumentObjectGroupPython] C_element133  label="C_element : 078"  # scripted group (container) (typed FeaturePython)
  n = 5
  ref = C_element
FEATURE [App::DocumentObjectGroupPython] N_element052  label="N_element : 024"  # scripted group (container) (typed FeaturePython)
  n = 2
  ref = N_element
FEATURE [App::DocumentObjectGroupPython] O_element114  label="O_element : 067"  # scripted group (container) (typed FeaturePython)
  n = 2
  ref = O_element
FEATURE [App::DocumentObjectGroupPython] G4_THYMINE  # scripted group (container) (typed FeaturePython)
  Dunit = g/cm3
  Dvalue = 1.23
  Group = -> [H_element123,C_element133,N_element052,O_element114]
  conduct = 2
  density = 1
  expand = 3
  formula = G4_THYMINE
  name = G4_THYMINE
  specific = 4
FEATURE [App::DocumentObjectGroupPython] H_element124  label="H_element : 071"  # scripted group (container) (typed FeaturePython)
  n = 4
  ref = H_element
FEATURE [App::DocumentObjectGroupPython] C_element134  label="C_element : 079"  # scripted group (container) (typed FeaturePython)
  n = 4
  ref = C_element
FEATURE [App::DocumentObjectGroupPython] N_element053  label="N_element : 025"  # scripted group (container) (typed FeaturePython)
  n = 2
  ref = N_element
FEATURE [App::DocumentObjectGroupPython] O_element115  label="O_element : 068"  # scripted group (container) (typed FeaturePython)
  n = 2
  ref = O_element
FEATURE [App::DocumentObjectGroupPython] G4_URACIL  # scripted group (container) (typed FeaturePython)
  Dunit = g/cm3
  Dvalue = 1.32
  Group = -> [H_element124,C_element134,N_element053,O_element115]
  conduct = 2
  density = 1
  expand = 3
  formula = G4_URACIL
  name = G4_URACIL
  specific = 4
FEATURE [App::DocumentObjectGroupPython] H_element125  label="H_element : 072"  # scripted group (container) (typed FeaturePython)
  n = 4
  ref = H_element
FEATURE [App::DocumentObjectGroupPython] C_element135  label="C_element : 080"  # scripted group (container) (typed FeaturePython)
  n = 5
  ref = C_element
FEATURE [App::DocumentObjectGroupPython] N_element054  label="N_element : 026"  # scripted group (container) (typed FeaturePython)
  n = 5
  ref = N_element
FEATURE [App::DocumentObjectGroupPython] G4_DNA_ADENINE  # scripted group (container) (typed FeaturePython)
  Dunit = g/cm3
  Dvalue = 1
  Group = -> [H_element125,C_element135,N_element054]
  conduct = 2
  density = 1
  expand = 3
  formula = G4_DNA_ADENINE
  name = G4_DNA_ADENINE
  specific = 4
FEATURE [App::DocumentObjectGroupPython] H_element126  label="H_element : 073"  # scripted group (container) (typed FeaturePython)
  n = 4
  ref = H_element
FEATURE [App::DocumentObjectGroupPython] C_element136  label="C_element : 081"  # scripted group (container) (typed FeaturePython)
  n = 5
  ref = C_element
FEATURE [App::DocumentObjectGroupPython] N_element055  label="N_element : 027"  # scripted group (container) (typed FeaturePython)
  n = 5
  ref = N_element
FEATURE [App::DocumentObjectGroupPython] O_element116  label="O_element : 069"  # scripted group (container) (typed FeaturePython)
  n = 1
  ref = O_element
FEATURE [App::DocumentObjectGroupPython] G4_DNA_GUANINE  # scripted group (container) (typed FeaturePython)
  Dunit = g/cm3
  Dvalue = 1
  Group = -> [H_element126,C_element136,N_element055,O_element116]
  conduct = 2
  density = 1
  expand = 3
  formula = G4_DNA_GUANINE
  name = G4_DNA_GUANINE
  specific = 4
FEATURE [App::DocumentObjectGroupPython] H_element127  label="H_element : 074"  # scripted group (container) (typed FeaturePython)
  n = 4
  ref = H_element
FEATURE [App::DocumentObjectGroupPython] C_element137  label="C_element : 082"  # scripted group (container) (typed FeaturePython)
  n = 4
  ref = C_element
FEATURE [App::DocumentObjectGroupPython] N_element056  label="N_element : 028"  # scripted group (container) (typed FeaturePython)
  n = 3
  ref = N_element
FEATURE [App::DocumentObjectGroupPython] O_element117  label="O_element : 070"  # scripted group (container) (typed FeaturePython)
  n = 1
  ref = O_element
FEATURE [App::DocumentObjectGroupPython] G4_DNA_CYTOSINE  # scripted group (container) (typed FeaturePython)
  Dunit = g/cm3
  Dvalue = 1
  Group = -> [H_element127,C_element137,N_element056,O_element117]
  conduct = 2
  density = 1
  expand = 3
  formula = G4_DNA_CYTOSINE
  name = G4_DNA_CYTOSINE
  specific = 4
FEATURE [App::DocumentObjectGroupPython] H_element128  label="H_element : 075"  # scripted group (container) (typed FeaturePython)
  n = 5
  ref = H_element
FEATURE [App::DocumentObjectGroupPython] C_element138  label="C_element : 083"  # scripted group (container) (typed FeaturePython)
  n = 5
  ref = C_element
FEATURE [App::DocumentObjectGroupPython] N_element057  label="N_element : 029"  # scripted group (container) (typed FeaturePython)
  n = 2
  ref = N_element
FEATURE [App::DocumentObjectGroupPython] O_element118  label="O_element : 071"  # scripted group (container) (typed FeaturePython)
  n = 2
  ref = O_element
FEATURE [App::DocumentObjectGroupPython] G4_DNA_THYMINE  # scripted group (container) (typed FeaturePython)
  Dunit = g/cm3
  Dvalue = 1
  Group = -> [H_element128,C_element138,N_element057,O_element118]
  conduct = 2
  density = 1
  expand = 3
  formula = G4_DNA_THYMINE
  name = G4_DNA_THYMINE
  specific = 4
FEATURE [App::DocumentObjectGroupPython] H_element129  label="H_element : 076"  # scripted group (container) (typed FeaturePython)
  n = 3
  ref = H_element
FEATURE [App::DocumentObjectGroupPython] C_element139  label="C_element : 084"  # scripted group (container) (typed FeaturePython)
  n = 4
  ref = C_element
FEATURE [App::DocumentObjectGroupPython] N_element058  label="N_element : 030"  # scripted group (container) (typed FeaturePython)
  n = 2
  ref = N_element
FEATURE [App::DocumentObjectGroupPython] O_element119  label="O_element : 072"  # scripted group (container) (typed FeaturePython)
  n = 2
  ref = O_element
FEATURE [App::DocumentObjectGroupPython] G4_DNA_URACIL  # scripted group (container) (typed FeaturePython)
  Dunit = g/cm3
  Dvalue = 1
  Group = -> [H_element129,C_element139,N_element058,O_element119]
  conduct = 2
  density = 1
  expand = 3
  formula = G4_DNA_URACIL
  name = G4_DNA_URACIL
  specific = 4
FEATURE [App::DocumentObjectGroupPython] H_element130  label="H_element : 077"  # scripted group (container) (typed FeaturePython)
  n = 10
  ref = H_element
FEATURE [App::DocumentObjectGroupPython] C_element140  label="C_element : 085"  # scripted group (container) (typed FeaturePython)
  n = 10
  ref = C_element
FEATURE [App::DocumentObjectGroupPython] N_element059  label="N_element : 031"  # scripted group (container) (typed FeaturePython)
  n = 5
  ref = N_element
FEATURE [App::DocumentObjectGroupPython] O_element120  label="O_element : 073"  # scripted group (container) (typed FeaturePython)
  n = 4
  ref = O_element
FEATURE [App::DocumentObjectGroupPython] G4_DNA_ADENOSINE  # scripted group (container) (typed FeaturePython)
  Dunit = g/cm3
  Dvalue = 1
  Group = -> [H_element130,C_element140,N_element059,O_element120]
  conduct = 2
  density = 1
  expand = 3
  formula = G4_DNA_ADENOSINE
  name = G4_DNA_ADENOSINE
  specific = 4
FEATURE [App::DocumentObjectGroupPython] H_element131  label="H_element : 078"  # scripted group (container) (typed FeaturePython)
  n = 10
  ref = H_element
FEATURE [App::DocumentObjectGroupPython] C_element141  label="C_element : 086"  # scripted group (container) (typed FeaturePython)
  n = 10
  ref = C_element
FEATURE [App::DocumentObjectGroupPython] N_element060  label="N_element : 032"  # scripted group (container) (typed FeaturePython)
  n = 5
  ref = N_element
FEATURE [App::DocumentObjectGroupPython] O_element121  label="O_element : 074"  # scripted group (container) (typed FeaturePython)
  n = 5
  ref = O_element
FEATURE [App::DocumentObjectGroupPython] G4_DNA_GUANOSINE  # scripted group (container) (typed FeaturePython)
  Dunit = g/cm3
  Dvalue = 1
  Group = -> [H_element131,C_element141,N_element060,O_element121]
  conduct = 2
  density = 1
  expand = 3
  formula = G4_DNA_GUANOSINE
  name = G4_DNA_GUANOSINE
  specific = 4
FEATURE [App::DocumentObjectGroupPython] H_element132  label="H_element : 079"  # scripted group (container) (typed FeaturePython)
  n = 10
  ref = H_element
FEATURE [App::DocumentObjectGroupPython] C_element142  label="C_element : 087"  # scripted group (container) (typed FeaturePython)
  n = 9
  ref = C_element
FEATURE [App::DocumentObjectGroupPython] N_element061  label="N_element : 033"  # scripted group (container) (typed FeaturePython)
  n = 3
  ref = N_element
FEATURE [App::DocumentObjectGroupPython] O_element122  label="O_element : 075"  # scripted group (container) (typed FeaturePython)
  n = 5
  ref = O_element
FEATURE [App::DocumentObjectGroupPython] G4_DNA_CYTIDINE  # scripted group (container) (typed FeaturePython)
  Dunit = g/cm3
  Dvalue = 1
  Group = -> [H_element132,C_element142,N_element061,O_element122]
  conduct = 2
  density = 1
  expand = 3
  formula = G4_DNA_CYTIDINE
  name = G4_DNA_CYTIDINE
  specific = 4
FEATURE [App::DocumentObjectGroupPython] H_element133  label="H_element : 080"  # scripted group (container) (typed FeaturePython)
  n = 9
  ref = H_element
FEATURE [App::DocumentObjectGroupPython] C_element143  label="C_element : 088"  # scripted group (container) (typed FeaturePython)
  n = 9
  ref = C_element
FEATURE [App::DocumentObjectGroupPython] N_element062  label="N_element : 034"  # scripted group (container) (typed FeaturePython)
  n = 2
  ref = N_element
FEATURE [App::DocumentObjectGroupPython] O_element123  label="O_element : 076"  # scripted group (container) (typed FeaturePython)
  n = 6
  ref = O_element
FEATURE [App::DocumentObjectGroupPython] G4_DNA_URIDINE  # scripted group (container) (typed FeaturePython)
  Dunit = g/cm3
  Dvalue = 1
  Group = -> [H_element133,C_element143,N_element062,O_element123]
  conduct = 2
  density = 1
  expand = 3
  formula = G4_DNA_URIDINE
  name = G4_DNA_URIDINE
  specific = 4
FEATURE [App::DocumentObjectGroupPython] H_element134  label="H_element : 081"  # scripted group (container) (typed FeaturePython)
  n = 11
  ref = H_element
FEATURE [App::DocumentObjectGroupPython] C_element144  label="C_element : 089"  # scripted group (container) (typed FeaturePython)
  n = 10
  ref = C_element
FEATURE [App::DocumentObjectGroupPython] N_element063  label="N_element : 035"  # scripted group (container) (typed FeaturePython)
  n = 2
  ref = N_element
FEATURE [App::DocumentObjectGroupPython] O_element124  label="O_element : 077"  # scripted group (container) (typed FeaturePython)
  n = 6
  ref = O_element
FEATURE [App::DocumentObjectGroupPython] G4_DNA_METHYLURIDINE  # scripted group (container) (typed FeaturePython)
  Dunit = g/cm3
  Dvalue = 1
  Group = -> [H_element134,C_element144,N_element063,O_element124]
  conduct = 2
  density = 1
  expand = 3
  formula = G4_DNA_METHYLURIDINE
  name = G4_DNA_METHYLURIDINE
  specific = 4
FEATURE [App::DocumentObjectGroupPython] P_element014  label="P_element : 003"  # scripted group (container) (typed FeaturePython)
  n = 1
  ref = P_element
FEATURE [App::DocumentObjectGroupPython] O_element125  label="O_element : 078"  # scripted group (container) (typed FeaturePython)
  n = 3
  ref = O_element
FEATURE [App::DocumentObjectGroupPython] G4_DNA_MONOPHOSPHATE  # scripted group (container) (typed FeaturePython)
  Dunit = g/cm3
  Dvalue = 1
  Group = -> [P_element014,O_element125]
  conduct = 2
  density = 1
  expand = 3
  formula = G4_DNA_MONOPHOSPHATE
  name = G4_DNA_MONOPHOSPHATE
  specific = 4
FEATURE [App::DocumentObjectGroupPython] H_element135  label="H_element : 082"  # scripted group (container) (typed FeaturePython)
  n = 10
  ref = H_element
FEATURE [App::DocumentObjectGroupPython] C_element145  label="C_element : 090"  # scripted group (container) (typed FeaturePython)
  n = 10
  ref = C_element
FEATURE [App::DocumentObjectGroupPython] N_element064  label="N_element : 036"  # scripted group (container) (typed FeaturePython)
  n = 5
  ref = N_element
FEATURE [App::DocumentObjectGroupPython] O_element126  label="O_element : 079"  # scripted group (container) (typed FeaturePython)
  n = 7
  ref = O_element
FEATURE [App::DocumentObjectGroupPython] P_element015  label="P_element : 004"  # scripted group (container) (typed FeaturePython)
  n = 1
  ref = P_element
FEATURE [App::DocumentObjectGroupPython] G4_DNA_A  # scripted group (container) (typed FeaturePython)
  Dunit = g/cm3
  Dvalue = 1
  Group = -> [H_element135,C_element145,N_element064,O_element126,P_element015]
  conduct = 2
  density = 1
  expand = 3
  formula = G4_DNA_A
  name = G4_DNA_A
  specific = 4
FEATURE [App::DocumentObjectGroupPython] H_element136  label="H_element : 083"  # scripted group (container) (typed FeaturePython)
  n = 10
  ref = H_element
FEATURE [App::DocumentObjectGroupPython] C_element146  label="C_element : 091"  # scripted group (container) (typed FeaturePython)
  n = 10
  ref = C_element
FEATURE [App::DocumentObjectGroupPython] N_element065  label="N_element : 037"  # scripted group (container) (typed FeaturePython)
  n = 5
  ref = N_element
FEATURE [App::DocumentObjectGroupPython] O_element127  label="O_element : 8"  # scripted group (container) (typed FeaturePython)
  n = 8
  ref = O_element
FEATURE [App::DocumentObjectGroupPython] P_element016  label="P_element : 005"  # scripted group (container) (typed FeaturePython)
  n = 1
  ref = P_element
FEATURE [App::DocumentObjectGroupPython] G4_DNA_G  # scripted group (container) (typed FeaturePython)
  Dunit = g/cm3
  Dvalue = 1
  Group = -> [H_element136,C_element146,N_element065,O_element127,P_element016]
  conduct = 2
  density = 1
  expand = 3
  formula = G4_DNA_G
  name = G4_DNA_G
  specific = 4
FEATURE [App::DocumentObjectGroupPython] H_element137  label="H_element : 084"  # scripted group (container) (typed FeaturePython)
  n = 10
  ref = H_element
FEATURE [App::DocumentObjectGroupPython] C_element147  label="C_element : 092"  # scripted group (container) (typed FeaturePython)
  n = 9
  ref = C_element
FEATURE [App::DocumentObjectGroupPython] N_element066  label="N_element : 038"  # scripted group (container) (typed FeaturePython)
  n = 3
  ref = N_element
FEATURE [App::DocumentObjectGroupPython] O_element128  label="O_element : 080"  # scripted group (container) (typed FeaturePython)
  n = 8
  ref = O_element
FEATURE [App::DocumentObjectGroupPython] P_element017  label="P_element : 006"  # scripted group (container) (typed FeaturePython)
  n = 1
  ref = P_element
FEATURE [App::DocumentObjectGroupPython] G4_DNA_C  # scripted group (container) (typed FeaturePython)
  Dunit = g/cm3
  Dvalue = 1
  Group = -> [H_element137,C_element147,N_element066,O_element128,P_element017]
  conduct = 2
  density = 1
  expand = 3
  formula = G4_DNA_C
  name = G4_DNA_C
  specific = 4
FEATURE [App::DocumentObjectGroupPython] H_element138  label="H_element : 085"  # scripted group (container) (typed FeaturePython)
  n = 9
  ref = H_element
FEATURE [App::DocumentObjectGroupPython] C_element148  label="C_element : 093"  # scripted group (container) (typed FeaturePython)
  n = 9
  ref = C_element
FEATURE [App::DocumentObjectGroupPython] N_element067  label="N_element : 039"  # scripted group (container) (typed FeaturePython)
  n = 2
  ref = N_element
FEATURE [App::DocumentObjectGroupPython] O_element129  label="O_element : 9"  # scripted group (container) (typed FeaturePython)
  n = 9
  ref = O_element
FEATURE [App::DocumentObjectGroupPython] P_element018  label="P_element : 007"  # scripted group (container) (typed FeaturePython)
  n = 1
  ref = P_element
FEATURE [App::DocumentObjectGroupPython] G4_DNA_U  # scripted group (container) (typed FeaturePython)
  Dunit = g/cm3
  Dvalue = 1
  Group = -> [H_element138,C_element148,N_element067,O_element129,P_element018]
  conduct = 2
  density = 1
  expand = 3
  formula = G4_DNA_U
  name = G4_DNA_U
  specific = 4
FEATURE [App::DocumentObjectGroupPython] H_element139  label="H_element : 086"  # scripted group (container) (typed FeaturePython)
  n = 11
  ref = H_element
FEATURE [App::DocumentObjectGroupPython] C_element149  label="C_element : 094"  # scripted group (container) (typed FeaturePython)
  n = 10
  ref = C_element
FEATURE [App::DocumentObjectGroupPython] N_element068  label="N_element : 040"  # scripted group (container) (typed FeaturePython)
  n = 2
  ref = N_element
FEATURE [App::DocumentObjectGroupPython] O_element130  label="O_element : 081"  # scripted group (container) (typed FeaturePython)
  n = 9
  ref = O_element
FEATURE [App::DocumentObjectGroupPython] P_element019  label="P_element : 008"  # scripted group (container) (typed FeaturePython)
  n = 1
  ref = P_element
FEATURE [App::DocumentObjectGroupPython] G4_DNA_MU  # scripted group (container) (typed FeaturePython)
  Dunit = g/cm3
  Dvalue = 1
  Group = -> [H_element139,C_element149,N_element068,O_element130,P_element019]
  conduct = 2
  density = 1
  expand = 3
  formula = G4_DNA_MU
  name = G4_DNA_MU
  specific = 4
FEATURE [App::DocumentObjectGroupPython] BioChemical  # scripted group (container) (typed FeaturePython)
  Group = -> [G4_CYTOSINE,G4_THYMINE,G4_URACIL,G4_DNA_ADENINE,G4_DNA_GUANINE,G4_DNA_CYTOSINE,G4_DNA_THYMINE,G4_DNA_URACIL,G4_DNA_ADENOSINE,G4_DNA_GUANOSINE,G4_DNA_CYTIDINE,G4_DNA_URIDINE,G4_DNA_METHYLURIDINE,G4_DNA_MONOPHOSPHATE,G4_DNA_A,G4_DNA_G,G4_DNA_C,G4_DNA_U,G4_DNA_MU]
FEATURE [App::DocumentObjectGroupPython] G4Materials  # scripted group (container) (typed FeaturePython)
  Group = -> [NIST,Element,HEP,Space,BioChemical]
  version = 1
FEATURE [App::DocumentObjectGroupPython] Geant4  # scripted group (container) (typed FeaturePython)
  Group = -> [G4Isotopes,G4Elements,G4Materials]
FEATURE [App::DocumentObjectGroupPython] Materials  # scripted group (container) (typed FeaturePython)
  Group = -> [Geant4]
FEATURE [Part::FeaturePython] GDMLBox_WorldBox  # WARN: FeaturePython — macro-defined, semantics opaque (R4)
  lunit = 2
  material = 5
  x = 100
  y = 100
  z = 100
FEATURE [Part::Box] Box  label="Cube"
  AttacherType = Attacher::AttachEngine3D
  Height = 10
  Length = 10
  Placement = pos=(5,0,0) rot=(0,0,1;0rad)
  Width = 10
FEATURE [Part::Chamfer] Chamfer
  Base = -> Box
  EdgeLinks = -> Box [Edge1,Edge2,Edge3,Edge4,Edge5,Edge6,Edge7,Edge8,Edge9,Edge10,Edge11,Edge12]
  Edges = 12 edges r=1: [Edge1,Edge2,Edge3,Edge4,Edge5,Edge6,Edge7,Edge8,Edge9,Edge10,Edge11,Edge12]
  Placement = pos=(0,0,0) rot=(0,0,1;0.523599rad)
FEATURE [Part::Box] Box001  label="Cube001"
  AttacherType = Attacher::AttachEngine3D
  Height = 10
  Length = 10
  Placement = pos=(0,0,0) rot=(1,0,0;0.698132rad)
  Width = 10
FEATURE [Part::Fillet] Fillet
  Base = -> Box001
  EdgeLinks = -> Box001 [Edge1,Edge2,Edge3,Edge4,Edge5,Edge6,Edge7,Edge8,Edge9,Edge10,Edge11,Edge12]
  Edges = 12 edges r=1: [Edge1,Edge2,Edge3,Edge4,Edge5,Edge6,Edge7,Edge8,Edge9,Edge10,Edge11,Edge12]
  Placement = pos=(0,0,-7) rot=(0,0,1;0rad)
FEATURE [App::Part] Part  label="Part_fillet"
  Group = -> [Box001,Fillet]
  Origin = -> Origin001
  Placement = pos=(-14,0,15) rot=(0,0,1;0rad)
FEATURE [App::Part] Part001  label="Part_chamfer"
  Group = -> [Box,Chamfer]
  Origin = -> Origin002
  Placement = pos=(4,0,15) rot=(0,0,1;0rad)
FEATURE [App::Part] worldVOL
  Group = -> [GDMLBox_WorldBox,Part,Part001]
  Origin = -> Origin
